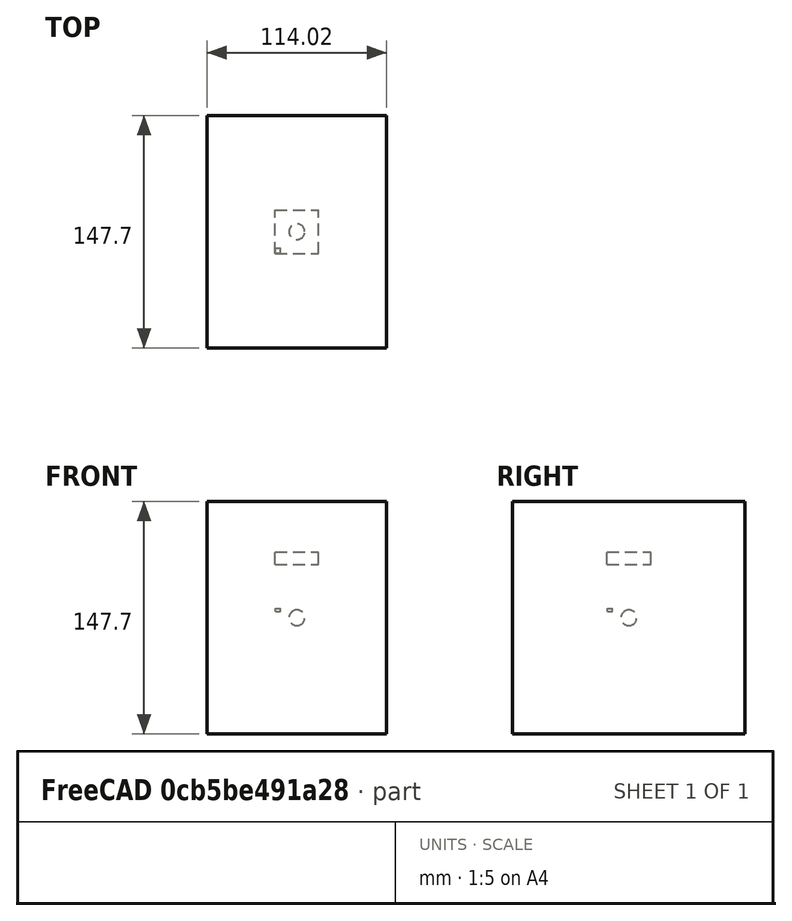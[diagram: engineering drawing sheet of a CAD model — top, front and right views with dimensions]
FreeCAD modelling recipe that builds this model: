
FCSTD DOCUMENT  (FreeCAD 1.0R39109 (Git))
Label: NoArray-borderTest-1
License: All rights reserved
objects: App::DocumentObjectGroupPython×1272, App::Link×77, App::Part×7, Part::FeaturePython×4, App::FeaturePython×1
note: 4 computed .brp shape members not serialized (recipe doc carries the construction recipe); baked Part::Feature solids carry a one-line shape summary decoded from their .brp

FEATURE [App::DocumentObjectGroupPython] HALFPI  # scripted group (container) (typed FeaturePython)
  name = HALFPI
  value = pi/2.
FEATURE [App::DocumentObjectGroupPython] PI  # scripted group (container) (typed FeaturePython)
  name = PI
  value = 1.*pi
FEATURE [App::DocumentObjectGroupPython] TWOPI  # scripted group (container) (typed FeaturePython)
  name = TWOPI
  value = 2.*pi
FEATURE [App::DocumentObjectGroupPython] Constants  # scripted group (container) (typed FeaturePython)
  Group = -> [HALFPI,PI,TWOPI]
FEATURE [App::DocumentObjectGroupPython] Variables  # scripted group (container) (typed FeaturePython)
FEATURE [App::DocumentObjectGroupPython] Quantities  # scripted group (container) (typed FeaturePython)
FEATURE [App::DocumentObjectGroupPython] Isotopes  # scripted group (container) (typed FeaturePython)
FEATURE [App::DocumentObjectGroupPython] Elements  # scripted group (container) (typed FeaturePython)
FEATURE [App::DocumentObjectGroupPython] G4_AIR  label="G4_AIR : 1.000"  # scripted group (container) (typed FeaturePython)
  n = 1
FEATURE [App::DocumentObjectGroupPython] Air  # scripted group (container) (typed FeaturePython)
  Dunit = mg/cm3
  Dvalue = 1.29
  Group = -> [G4_AIR]
  RINDEX = AirRINDEX
  conduct = 2
  density = 1
  expand = 3
  name = Air
  specific = 4
FEATURE [App::DocumentObjectGroupPython] SY  # scripted group (container) (typed FeaturePython)
  coldim = 1
  values = 100000/MeV
FEATURE [App::DocumentObjectGroupPython] RS  # scripted group (container) (typed FeaturePython)
  coldim = 1
  values = 1
FEATURE [App::DocumentObjectGroupPython] FTC  # scripted group (container) (typed FeaturePython)
  coldim = 1
  values = 21.5*ns
FEATURE [App::DocumentObjectGroupPython] STC  # scripted group (container) (typed FeaturePython)
  coldim = 1
  values = 43.8*ns
FEATURE [App::DocumentObjectGroupPython] RY1  # scripted group (container) (typed FeaturePython)
  coldim = 1
  values = 95
FEATURE [App::DocumentObjectGroupPython] RY2  # scripted group (container) (typed FeaturePython)
  coldim = 1
  values = 5
FEATURE [App::DocumentObjectGroupPython] YR  # scripted group (container) (typed FeaturePython)
  coldim = 1
  values = 0.8
FEATURE [App::DocumentObjectGroupPython] SCINTLAR  # scripted group (container) (typed FeaturePython)
  coldim = 2
  values = <blob: 2358 chars omitted>
FEATURE [App::DocumentObjectGroupPython] RINDEXLAR  # scripted group (container) (typed FeaturePython)
  coldim = 2
  values = <blob: 9384 chars omitted>
FEATURE [App::DocumentObjectGroupPython] ABSLENGTHLAR  # scripted group (container) (typed FeaturePython)
  coldim = 2
  values = 7.74901*eV 10.0*m 7.77525*eV 10.0*m 7.80167*eV 10.0*m 7.82827*eV 10.0*m 7.85506*eV 10.0*m 7.88202*eV 10.0*m 7.90917*eV 10.0*m 7.93651*eV 10.0*m 7.96404*eV 10.0*m 7.99176*eV 10.0*m 8.01968*eV 10.0*m 8.04779*eV 10.0*m 8.07609*eV 10.0*m 8.1046*eV 10.0*m 8.13331*eV 10.0*m 8.16222*eV 10.0*m 8.19134*eV 10.0*m 8.22067*eV 10.0*m 8.25021*eV 10.0*m 8.27996*eV 10.0*m 8.30993*eV 10.0*m 8.34012*eV 10.0*m 8.37052*eV 10.0*m 8.40115*eV 10.0*m 8.432*eV 10.0*m 8.46308*eV 10.0*m 8.4944*eV 10.0*m 8.52594*eV 10.0*m 8.55772*eV 10.0*m 8.58973*eV 10.0*m 8.62199*eV 10.0*m 8.65449*eV 10.0*m 8.68723*eV 10.0*m 8.72023*eV 10.0*m 8.75347*eV 10.0*m 8.78697*eV 10.0*m 8.82073*eV 10.0*m 8.85475*eV 10.0*m 8.88903*eV 10.0*m 8.92358*eV 10.0*m 8.9584*eV 10.0*m 8.99349*eV 10.0*m 9.02885*eV 10.0*m 9.0645*eV 10.0*m 9.10043*eV 10.0*m 9.13664*eV 10.0*m 9.17314*eV 10.0*m 9.20994*eV 10.0*m 9.24703*eV 10.0*m 9.28442*eV 10.0*m 9.32212*eV 10.0*m 9.36012*eV 10.0*m 9.39844*eV 10.0*m 9.43707*eV 10.0*m 9.47602*eV 10.0*m 9.51529*eV 10.0*m 9.55489*eV 10.0*m 9.59481*eV 10.0*m 9.63508*eV 10.0*m 9.67568*eV 10.0*m 9.71663*eV 10.0*m 9.75792*eV 10.0*m 9.79957*eV 10.0*m 9.84158*eV 10.0*m 9.88394*eV 10.0*m 9.92668*eV 10.0*m 9.96978*eV 10.0*m 10.0133*eV 10.0*m 10.0571*eV 10.0*m 10.1014*eV 10.0*m 10.146*eV 10.0*m 10.191*eV 10.0*m 10.2365*eV 10.0*m 10.2823*eV 10.0*m 10.3286*eV 10.0*m 10.3752*eV 10.0*m 10.4223*eV 10.0*m 10.4699*eV 10.0*m 10.5178*eV 10.0*m 10.5662*eV 10.0*m 10.6151*eV 10.0*m 10.6644*eV 10.0*m 10.7142*eV 10.0*m 10.7644*eV 10.0*m 10.8151*eV 10.0*m 10.8663*eV 10.0*m 10.9179*eV 10.0*m 10.9701*eV 10.0*m 11.0228*eV 10.0*m 11.076*eV 10.0*m 11.1296*eV 10.0*m 11.1839*eV 10.0*m 11.2386*eV 10.0*m 11.2939*eV 10.0*m 11.3497*eV 10.0*m 11.4061*eV 10.0*m 11.463*eV 10.0*m 11.5206*eV 10.0*m 11.5787*eV 10.0*m 11.6373*eV 10.0*m
FEATURE [App::DocumentObjectGroupPython] RAYLEIGHLAR  # scripted group (container) (typed FeaturePython)
  coldim = 2
  values = 7.74901*eV 90.0*cm 7.77525*eV 90.0*cm 7.80167*eV 90.0*cm 7.82827*eV 90.0*cm 7.85506*eV 90.0*cm 7.88202*eV 90.0*cm 7.90917*eV 90.0*cm 7.93651*eV 90.0*cm 7.96404*eV 90.0*cm 7.99176*eV 90.0*cm 8.01968*eV 90.0*cm 8.04779*eV 90.0*cm 8.07609*eV 90.0*cm 8.1046*eV 90.0*cm 8.13331*eV 90.0*cm 8.16222*eV 90.0*cm 8.19134*eV 90.0*cm 8.22067*eV 90.0*cm 8.25021*eV 90.0*cm 8.27996*eV 90.0*cm 8.30993*eV 90.0*cm 8.34012*eV 90.0*cm 8.37052*eV 90.0*cm 8.40115*eV 90.0*cm 8.432*eV 90.0*cm 8.46308*eV 90.0*cm 8.4944*eV 90.0*cm 8.52594*eV 90.0*cm 8.55772*eV 90.0*cm 8.58973*eV 90.0*cm 8.62199*eV 90.0*cm 8.65449*eV 90.0*cm 8.68723*eV 90.0*cm 8.72023*eV 90.0*cm 8.75347*eV 90.0*cm 8.78697*eV 90.0*cm 8.82073*eV 90.0*cm 8.85475*eV 90.0*cm 8.88903*eV 90.0*cm 8.92358*eV 90.0*cm 8.9584*eV 90.0*cm 8.99349*eV 90.0*cm 9.02885*eV 90.0*cm 9.0645*eV 90.0*cm 9.10043*eV 90.0*cm 9.13664*eV 90.0*cm 9.17314*eV 90.0*cm 9.20994*eV 90.0*cm 9.24703*eV 90.0*cm 9.28442*eV 90.0*cm 9.32212*eV 90.0*cm 9.36012*eV 90.0*cm 9.39844*eV 90.0*cm 9.43707*eV 90.0*cm 9.47602*eV 90.0*cm 9.51529*eV 90.0*cm 9.55489*eV 90.0*cm 9.59481*eV 90.0*cm 9.63508*eV 90.0*cm 9.67568*eV 90.0*cm 9.71663*eV 90.0*cm 9.75792*eV 90.0*cm 9.79957*eV 90.0*cm 9.84158*eV 90.0*cm 9.88394*eV 90.0*cm 9.92668*eV 90.0*cm 9.96978*eV 90.0*cm 10.0133*eV 90.0*cm 10.0571*eV 90.0*cm 10.1014*eV 90.0*cm 10.146*eV 90.0*cm 10.191*eV 90.0*cm 10.2365*eV 90.0*cm 10.2823*eV 90.0*cm 10.3286*eV 90.0*cm 10.3752*eV 90.0*cm 10.4223*eV 90.0*cm 10.4699*eV 90.0*cm 10.5178*eV 90.0*cm 10.5662*eV 90.0*cm 10.6151*eV 90.0*cm 10.6644*eV 90.0*cm 10.7142*eV 90.0*cm 10.7644*eV 90.0*cm 10.8151*eV 90.0*cm 10.8663*eV 90.0*cm 10.9179*eV 90.0*cm 10.9701*eV 90.0*cm 11.0228*eV 90.0*cm 11.076*eV 90.0*cm 11.1296*eV 90.0*cm 11.1839*eV 90.0*cm 11.2386*eV 90.0*cm 11.2939*eV 90.0*cm 11.3497*eV 90.0*cm 11.4061*eV 90.0*cm 11.463*eV 90.0*cm 11.5206*eV 90.0*cm 11.5787*eV 90.0*cm 11.6373*eV 90.0*cm
FEATURE [App::DocumentObjectGroupPython] REFLECTIVITY  # scripted group (container) (typed FeaturePython)
  coldim = 2
  values = 2.034*eV 0.98 2.068*eV 0.98 2.103*eV 0.98 2.139*eV 0.98 2.177*eV 0.98 2.216*eV 0.98 2.256*eV 0.98 2.298*eV 0.98 2.341*eV 0.98 2.386*eV 0.98 2.433*eV 0.98 2.481*eV 0.98 2.532*eV 0.98 2.585*eV 0.98 2.64*eV 0.98 2.697*eV 0.98 2.757*eV 0.98 2.82*eV 0.98 2.885*eV 0.98 2.954*eV 0.98 3.026*eV 0.98 3.102*eV 0.98 3.181*eV 0.98 3.265*eV 0.98 3.353*eV 0.98 3.446*eV 0.98 3.545*eV 0.98 3.649*eV 0.98 3.76*eV 0.98 3.877*eV 0.98 4.002*eV 0.98 4.136*eV 0.98 5.0*eV 0.98 6.0*eV 0.98 7.0*eV 0.98 8.0*eV 0.98 9.0*eV 0.98 9.0*eV 0.98 10.0*eV 0.98 11.0*eV 0.98 11.6*eV 0.98
FEATURE [App::DocumentObjectGroupPython] EFFICIENCY  # scripted group (container) (typed FeaturePython)
  coldim = 2
  values = 2.034*eV 1 2.068*eV 1 2.103*eV 1 2.139*eV 1 2.177*eV 1 2.216*eV 1 2.256*eV 1 2.298*eV 1 2.341*eV 1 2.386*eV 1 2.433*eV 1 2.481*eV 1 2.532*eV 1 2.585*eV 1 2.64*eV 1 2.697*eV 1 2.757*eV 1 2.82*eV 1 2.885*eV 1 2.954*eV 1 3.026*eV 1 3.102*eV 1 3.181*eV  1 3.265*eV 1 3.353*eV 1 3.446*eV 1 3.545*eV 1 3.649*eV 1 3.76*eV 1 3.877*eV 1 4.002*eV 1 4.136*eV 1 5.0*eV 1 6.0*eV 1 7.0*eV 1 8.0*eV 1 9.0*eV 1 9.0*eV 1 10.0*eV 1 11.0*eV 1 11.6*eV 1
FEATURE [App::DocumentObjectGroupPython] AirRINDEX  # scripted group (container) (typed FeaturePython)
  coldim = 2
  values = 2.034*eV 1 2.068*eV 1 2.103*eV 1 2.139*eV 1 2.177*eV 1 2.216*eV 1 2.256*eV 1 2.298*eV 1 2.341*eV 1 2.386*eV 1 2.433*eV 1 2.481*eV 1 2.532*eV 1 2.585*eV 1 2.64*eV 1 2.697*eV 1 2.757*eV 1 2.82*eV 1 2.885*eV 1 2.954*eV 1 3.026*eV 1 3.102*eV 1 3.181*eV 1 3.265*eV 1 3.353*eV 1 3.446*eV 1 3.545*eV 1 3.649*eV 1 3.76*eV 1 3.877*eV 1 4.002*eV 1 4.136*eV 1 5.0*eV 1 6.0*eV 1 7.0*eV 1 8.0*eV 1 9.0*eV 1 10.0*eV 1 11.0*eV 1 11.6*eV 1
FEATURE [App::DocumentObjectGroupPython] Matrix  # scripted group (container) (typed FeaturePython)
  Group = -> [SY,RS,FTC,STC,RY1,RY2,YR,SCINTLAR,RINDEXLAR,ABSLENGTHLAR,RAYLEIGHLAR,REFLECTIVITY,EFFICIENCY,AirRINDEX]
FEATURE [App::DocumentObjectGroupPython] ScintWrap  # scripted group (container) (typed FeaturePython)
  EFFICIENCY = EFFICIENCY
  REFLECTIVITY = REFLECTIVITY
  finish = 39
  model = 0
  type = 2
  value = 1
FEATURE [App::DocumentObjectGroupPython] Surfaces  # scripted group (container) (typed FeaturePython)
  Group = -> [ScintWrap]
FEATURE [App::DocumentObjectGroupPython] Opticals  # scripted group (container) (typed FeaturePython)
  Group = -> [Matrix,Surfaces]
FEATURE [App::DocumentObjectGroupPython] G4Isotopes  # scripted group (container) (typed FeaturePython)
FEATURE [App::DocumentObjectGroupPython] H_element  # scripted group (container) (typed FeaturePython)
  Z = 1
  atom_value = 1.008
  formula = H
  name = H_element
FEATURE [App::DocumentObjectGroupPython] He_element  # scripted group (container) (typed FeaturePython)
  Z = 2
  atom_value = 4.0026
  formula = He
  name = He_element
FEATURE [App::DocumentObjectGroupPython] Li_element  # scripted group (container) (typed FeaturePython)
  Z = 3
  atom_value = 6.94
  formula = Li
  name = Li_element
FEATURE [App::DocumentObjectGroupPython] Be_element  # scripted group (container) (typed FeaturePython)
  Z = 4
  atom_value = 9.01218
  formula = Be
  name = Be_element
FEATURE [App::DocumentObjectGroupPython] B_element  # scripted group (container) (typed FeaturePython)
  Z = 5
  atom_value = 10.81
  formula = B
  name = B_element
FEATURE [App::DocumentObjectGroupPython] C_element  # scripted group (container) (typed FeaturePython)
  Z = 6
  atom_value = 12.011
  formula = C
  name = C_element
FEATURE [App::DocumentObjectGroupPython] N_element  # scripted group (container) (typed FeaturePython)
  Z = 7
  atom_value = 14.007
  formula = N
  name = N_element
FEATURE [App::DocumentObjectGroupPython] O_element  # scripted group (container) (typed FeaturePython)
  Z = 8
  atom_value = 15.999
  formula = O
  name = O_element
FEATURE [App::DocumentObjectGroupPython] F_element  # scripted group (container) (typed FeaturePython)
  Z = 9
  atom_value = 18.9984
  formula = F
  name = F_element
FEATURE [App::DocumentObjectGroupPython] Ne_element  # scripted group (container) (typed FeaturePython)
  Z = 10
  atom_value = 20.1797
  formula = Ne
  name = Ne_element
FEATURE [App::DocumentObjectGroupPython] Na_element  # scripted group (container) (typed FeaturePython)
  Z = 11
  atom_value = 22.9898
  formula = Na
  name = Na_element
FEATURE [App::DocumentObjectGroupPython] Mg_element  # scripted group (container) (typed FeaturePython)
  Z = 12
  atom_value = 24.305
  formula = Mg
  name = Mg_element
FEATURE [App::DocumentObjectGroupPython] Al_element  # scripted group (container) (typed FeaturePython)
  Z = 13
  atom_value = 26.9815
  formula = Al
  name = Al_element
FEATURE [App::DocumentObjectGroupPython] Si_element  # scripted group (container) (typed FeaturePython)
  Z = 14
  atom_value = 28.085
  formula = Si
  name = Si_element
FEATURE [App::DocumentObjectGroupPython] P_element  # scripted group (container) (typed FeaturePython)
  Z = 15
  atom_value = 30.9738
  formula = P
  name = P_element
FEATURE [App::DocumentObjectGroupPython] S_element  # scripted group (container) (typed FeaturePython)
  Z = 16
  atom_value = 32.06
  formula = S
  name = S_element
FEATURE [App::DocumentObjectGroupPython] Cl_element  # scripted group (container) (typed FeaturePython)
  Z = 17
  atom_value = 35.45
  formula = Cl
  name = Cl_element
FEATURE [App::DocumentObjectGroupPython] Ar_element  # scripted group (container) (typed FeaturePython)
  Z = 18
  atom_value = 39.95
  formula = Ar
  name = Ar_element
FEATURE [App::DocumentObjectGroupPython] K_element  # scripted group (container) (typed FeaturePython)
  Z = 19
  atom_value = 39.0983
  formula = K
  name = K_element
FEATURE [App::DocumentObjectGroupPython] Ca_element  # scripted group (container) (typed FeaturePython)
  Z = 20
  atom_value = 40.078
  formula = Ca
  name = Ca_element
FEATURE [App::DocumentObjectGroupPython] Sc_element  # scripted group (container) (typed FeaturePython)
  Z = 21
  atom_value = 44.9559
  formula = Sc
  name = Sc_element
FEATURE [App::DocumentObjectGroupPython] Ti_element  # scripted group (container) (typed FeaturePython)
  Z = 22
  atom_value = 47.867
  formula = Ti
  name = Ti_element
FEATURE [App::DocumentObjectGroupPython] V_element  # scripted group (container) (typed FeaturePython)
  Z = 23
  atom_value = 50.9415
  formula = V
  name = V_element
FEATURE [App::DocumentObjectGroupPython] Cr_element  # scripted group (container) (typed FeaturePython)
  Z = 24
  atom_value = 51.9961
  formula = Cr
  name = Cr_element
FEATURE [App::DocumentObjectGroupPython] Mn_element  # scripted group (container) (typed FeaturePython)
  Z = 25
  atom_value = 54.938
  formula = Mn
  name = Mn_element
FEATURE [App::DocumentObjectGroupPython] Fe_element  # scripted group (container) (typed FeaturePython)
  Z = 26
  atom_value = 55.845
  formula = Fe
  name = Fe_element
FEATURE [App::DocumentObjectGroupPython] Co_element  # scripted group (container) (typed FeaturePython)
  Z = 27
  atom_value = 58.9332
  formula = Co
  name = Co_element
FEATURE [App::DocumentObjectGroupPython] Ni_element  # scripted group (container) (typed FeaturePython)
  Z = 28
  atom_value = 58.6934
  formula = Ni
  name = Ni_element
FEATURE [App::DocumentObjectGroupPython] Cu_element  # scripted group (container) (typed FeaturePython)
  Z = 29
  atom_value = 63.546
  formula = Cu
  name = Cu_element
FEATURE [App::DocumentObjectGroupPython] Zn_element  # scripted group (container) (typed FeaturePython)
  Z = 30
  atom_value = 65.38
  formula = Zn
  name = Zn_element
FEATURE [App::DocumentObjectGroupPython] Ga_element  # scripted group (container) (typed FeaturePython)
  Z = 31
  atom_value = 69.723
  formula = Ga
  name = Ga_element
FEATURE [App::DocumentObjectGroupPython] Ge_element  # scripted group (container) (typed FeaturePython)
  Z = 32
  atom_value = 72.63
  formula = Ge
  name = Ge_element
FEATURE [App::DocumentObjectGroupPython] As_element  # scripted group (container) (typed FeaturePython)
  Z = 33
  atom_value = 74.9216
  formula = As
  name = As_element
FEATURE [App::DocumentObjectGroupPython] Se_element  # scripted group (container) (typed FeaturePython)
  Z = 34
  atom_value = 78.971
  formula = Se
  name = Se_element
FEATURE [App::DocumentObjectGroupPython] Br_element  # scripted group (container) (typed FeaturePython)
  Z = 35
  atom_value = 79.904
  formula = Br
  name = Br_element
FEATURE [App::DocumentObjectGroupPython] Kr_element  # scripted group (container) (typed FeaturePython)
  Z = 36
  atom_value = 83.798
  formula = Kr
  name = Kr_element
FEATURE [App::DocumentObjectGroupPython] Rb_element  # scripted group (container) (typed FeaturePython)
  Z = 37
  atom_value = 85.4678
  formula = Rb
  name = Rb_element
FEATURE [App::DocumentObjectGroupPython] Sr_element  # scripted group (container) (typed FeaturePython)
  Z = 38
  atom_value = 87.62
  formula = Sr
  name = Sr_element
FEATURE [App::DocumentObjectGroupPython] Y_element  # scripted group (container) (typed FeaturePython)
  Z = 39
  atom_value = 88.9058
  formula = Y
  name = Y_element
FEATURE [App::DocumentObjectGroupPython] Zr_element  # scripted group (container) (typed FeaturePython)
  Z = 40
  atom_value = 91.224
  formula = Zr
  name = Zr_element
FEATURE [App::DocumentObjectGroupPython] Nb_element  # scripted group (container) (typed FeaturePython)
  Z = 41
  atom_value = 92.9064
  formula = Nb
  name = Nb_element
FEATURE [App::DocumentObjectGroupPython] Mo_element  # scripted group (container) (typed FeaturePython)
  Z = 42
  atom_value = 95.95
  formula = Mo
  name = Mo_element
FEATURE [App::DocumentObjectGroupPython] Tc_element  # scripted group (container) (typed FeaturePython)
  Z = 43
  atom_value = 97
  formula = Tc
  name = Tc_element
FEATURE [App::DocumentObjectGroupPython] Ru_element  # scripted group (container) (typed FeaturePython)
  Z = 44
  atom_value = 101.07
  formula = Ru
  name = Ru_element
FEATURE [App::DocumentObjectGroupPython] Rh_element  # scripted group (container) (typed FeaturePython)
  Z = 45
  atom_value = 102.905
  formula = Rh
  name = Rh_element
FEATURE [App::DocumentObjectGroupPython] Pd_element  # scripted group (container) (typed FeaturePython)
  Z = 46
  atom_value = 106.42
  formula = Pd
  name = Pd_element
FEATURE [App::DocumentObjectGroupPython] Ag_element  # scripted group (container) (typed FeaturePython)
  Z = 47
  atom_value = 107.868
  formula = Ag
  name = Ag_element
FEATURE [App::DocumentObjectGroupPython] Cd_element  # scripted group (container) (typed FeaturePython)
  Z = 48
  atom_value = 112.414
  formula = Cd
  name = Cd_element
FEATURE [App::DocumentObjectGroupPython] In_element  # scripted group (container) (typed FeaturePython)
  Z = 49
  atom_value = 114.818
  formula = In
  name = In_element
FEATURE [App::DocumentObjectGroupPython] Sn_element  # scripted group (container) (typed FeaturePython)
  Z = 50
  atom_value = 118.71
  formula = Sn
  name = Sn_element
FEATURE [App::DocumentObjectGroupPython] Sb_element  # scripted group (container) (typed FeaturePython)
  Z = 51
  atom_value = 121.76
  formula = Sb
  name = Sb_element
FEATURE [App::DocumentObjectGroupPython] Te_element  # scripted group (container) (typed FeaturePython)
  Z = 52
  atom_value = 127.6
  formula = Te
  name = Te_element
FEATURE [App::DocumentObjectGroupPython] I_element  # scripted group (container) (typed FeaturePython)
  Z = 53
  atom_value = 126.904
  formula = I
  name = I_element
FEATURE [App::DocumentObjectGroupPython] Xe_element  # scripted group (container) (typed FeaturePython)
  Z = 54
  atom_value = 131.293
  formula = Xe
  name = Xe_element
FEATURE [App::DocumentObjectGroupPython] Cs_element  # scripted group (container) (typed FeaturePython)
  Z = 55
  atom_value = 132.905
  formula = Cs
  name = Cs_element
FEATURE [App::DocumentObjectGroupPython] Ba_element  # scripted group (container) (typed FeaturePython)
  Z = 56
  atom_value = 137.327
  formula = Ba
  name = Ba_element
FEATURE [App::DocumentObjectGroupPython] La_element  # scripted group (container) (typed FeaturePython)
  Z = 57
  atom_value = 138.905
  formula = La
  name = La_element
FEATURE [App::DocumentObjectGroupPython] Ce_element  # scripted group (container) (typed FeaturePython)
  Z = 58
  atom_value = 140.116
  formula = Ce
  name = Ce_element
FEATURE [App::DocumentObjectGroupPython] Pr_element  # scripted group (container) (typed FeaturePython)
  Z = 59
  atom_value = 140.908
  formula = Pr
  name = Pr_element
FEATURE [App::DocumentObjectGroupPython] Nd_element  # scripted group (container) (typed FeaturePython)
  Z = 60
  atom_value = 144.242
  formula = Nd
  name = Nd_element
FEATURE [App::DocumentObjectGroupPython] Pm_element  # scripted group (container) (typed FeaturePython)
  Z = 61
  atom_value = 145
  formula = Pm
  name = Pm_element
FEATURE [App::DocumentObjectGroupPython] Sm_element  # scripted group (container) (typed FeaturePython)
  Z = 62
  atom_value = 150.36
  formula = Sm
  name = Sm_element
FEATURE [App::DocumentObjectGroupPython] Eu_element  # scripted group (container) (typed FeaturePython)
  Z = 63
  atom_value = 151.964
  formula = Eu
  name = Eu_element
FEATURE [App::DocumentObjectGroupPython] Gd_element  # scripted group (container) (typed FeaturePython)
  Z = 64
  atom_value = 157.25
  formula = Gd
  name = Gd_element
FEATURE [App::DocumentObjectGroupPython] Tb_element  # scripted group (container) (typed FeaturePython)
  Z = 65
  atom_value = 158.925
  formula = Tb
  name = Tb_element
FEATURE [App::DocumentObjectGroupPython] Dy_element  # scripted group (container) (typed FeaturePython)
  Z = 66
  atom_value = 162.5
  formula = Dy
  name = Dy_element
FEATURE [App::DocumentObjectGroupPython] Ho_element  # scripted group (container) (typed FeaturePython)
  Z = 67
  atom_value = 164.93
  formula = Ho
  name = Ho_element
FEATURE [App::DocumentObjectGroupPython] Er_element  # scripted group (container) (typed FeaturePython)
  Z = 68
  atom_value = 167.259
  formula = Er
  name = Er_element
FEATURE [App::DocumentObjectGroupPython] Tm_element  # scripted group (container) (typed FeaturePython)
  Z = 69
  atom_value = 168.934
  formula = Tm
  name = Tm_element
FEATURE [App::DocumentObjectGroupPython] Yb_element  # scripted group (container) (typed FeaturePython)
  Z = 70
  atom_value = 173.045
  formula = Yb
  name = Yb_element
FEATURE [App::DocumentObjectGroupPython] Lu_element  # scripted group (container) (typed FeaturePython)
  Z = 71
  atom_value = 174.967
  formula = Lu
  name = Lu_element
FEATURE [App::DocumentObjectGroupPython] Hf_element  # scripted group (container) (typed FeaturePython)
  Z = 72
  atom_value = 178.49
  formula = Hf
  name = Hf_element
FEATURE [App::DocumentObjectGroupPython] Ta_element  # scripted group (container) (typed FeaturePython)
  Z = 73
  atom_value = 180.948
  formula = Ta
  name = Ta_element
FEATURE [App::DocumentObjectGroupPython] W_element  # scripted group (container) (typed FeaturePython)
  Z = 74
  atom_value = 183.84
  formula = W
  name = W_element
FEATURE [App::DocumentObjectGroupPython] Re_element  # scripted group (container) (typed FeaturePython)
  Z = 75
  atom_value = 186.207
  formula = Re
  name = Re_element
FEATURE [App::DocumentObjectGroupPython] Os_element  # scripted group (container) (typed FeaturePython)
  Z = 76
  atom_value = 190.23
  formula = Os
  name = Os_element
FEATURE [App::DocumentObjectGroupPython] Ir_element  # scripted group (container) (typed FeaturePython)
  Z = 77
  atom_value = 192.217
  formula = Ir
  name = Ir_element
FEATURE [App::DocumentObjectGroupPython] Pt_element  # scripted group (container) (typed FeaturePython)
  Z = 78
  atom_value = 195.084
  formula = Pt
  name = Pt_element
FEATURE [App::DocumentObjectGroupPython] Au_element  # scripted group (container) (typed FeaturePython)
  Z = 79
  atom_value = 196.967
  formula = Au
  name = Au_element
FEATURE [App::DocumentObjectGroupPython] Hg_element  # scripted group (container) (typed FeaturePython)
  Z = 80
  atom_value = 200.592
  formula = Hg
  name = Hg_element
FEATURE [App::DocumentObjectGroupPython] Tl_element  # scripted group (container) (typed FeaturePython)
  Z = 81
  atom_value = 204.38
  formula = Tl
  name = Tl_element
FEATURE [App::DocumentObjectGroupPython] Pb_element  # scripted group (container) (typed FeaturePython)
  Z = 82
  atom_value = 207.2
  formula = Pb
  name = Pb_element
FEATURE [App::DocumentObjectGroupPython] Bi_element  # scripted group (container) (typed FeaturePython)
  Z = 83
  atom_value = 208.98
  formula = Bi
  name = Bi_element
FEATURE [App::DocumentObjectGroupPython] Po_element  # scripted group (container) (typed FeaturePython)
  Z = 84
  atom_value = 209
  formula = Po
  name = Po_element
FEATURE [App::DocumentObjectGroupPython] At_element  # scripted group (container) (typed FeaturePython)
  Z = 85
  atom_value = 210
  formula = At
  name = At_element
FEATURE [App::DocumentObjectGroupPython] Rn_element  # scripted group (container) (typed FeaturePython)
  Z = 86
  atom_value = 222
  formula = Rn
  name = Rn_element
FEATURE [App::DocumentObjectGroupPython] Fr_element  # scripted group (container) (typed FeaturePython)
  Z = 87
  atom_value = 223
  formula = Fr
  name = Fr_element
FEATURE [App::DocumentObjectGroupPython] Ra_element  # scripted group (container) (typed FeaturePython)
  Z = 88
  atom_value = 226
  formula = Ra
  name = Ra_element
FEATURE [App::DocumentObjectGroupPython] Ac_element  # scripted group (container) (typed FeaturePython)
  Z = 89
  atom_value = 227
  formula = Ac
  name = Ac_element
FEATURE [App::DocumentObjectGroupPython] Th_element  # scripted group (container) (typed FeaturePython)
  Z = 90
  atom_value = 232.038
  formula = Th
  name = Th_element
FEATURE [App::DocumentObjectGroupPython] Pa_element  # scripted group (container) (typed FeaturePython)
  Z = 91
  atom_value = 231.036
  formula = Pa
  name = Pa_element
FEATURE [App::DocumentObjectGroupPython] U_element  # scripted group (container) (typed FeaturePython)
  Z = 92
  atom_value = 238.029
  formula = U
  name = U_element
FEATURE [App::DocumentObjectGroupPython] Np_element  # scripted group (container) (typed FeaturePython)
  Z = 93
  atom_value = 237
  formula = Np
  name = Np_element
FEATURE [App::DocumentObjectGroupPython] Pu_element  # scripted group (container) (typed FeaturePython)
  Z = 94
  atom_value = 244
  formula = Pu
  name = Pu_element
FEATURE [App::DocumentObjectGroupPython] Am_element  # scripted group (container) (typed FeaturePython)
  Z = 95
  atom_value = 243
  formula = Am
  name = Am_element
FEATURE [App::DocumentObjectGroupPython] Cm_element  # scripted group (container) (typed FeaturePython)
  Z = 96
  atom_value = 247
  formula = Cm
  name = Cm_element
FEATURE [App::DocumentObjectGroupPython] Bk_element  # scripted group (container) (typed FeaturePython)
  Z = 97
  atom_value = 247
  formula = Bk
  name = Bk_element
FEATURE [App::DocumentObjectGroupPython] Cf_element  # scripted group (container) (typed FeaturePython)
  Z = 98
  atom_value = 251
  formula = Cf
  name = Cf_element
FEATURE [App::DocumentObjectGroupPython] G4Elements  # scripted group (container) (typed FeaturePython)
  Group = -> [H_element,He_element,Li_element,Be_element,B_element,C_element,N_element,O_element,F_element,Ne_element,Na_element,Mg_element,Al_element,Si_element,P_element,S_element,Cl_element,Ar_element,K_element,Ca_element,Sc_element,Ti_element,V_element,Cr_element,Mn_element,Fe_element,Co_element,Ni_element,Cu_element,Zn_element,Ga_element,Ge_element,As_element,Se_element,Br_element,Kr_element,Rb_element,+61 more]
FEATURE [App::DocumentObjectGroupPython] H_element001  label="H_element : 0.101"  # scripted group (container) (typed FeaturePython)
  n = 0.101327
FEATURE [App::DocumentObjectGroupPython] C_element001  label="C_element : 0.775"  # scripted group (container) (typed FeaturePython)
  n = 0.7755
FEATURE [App::DocumentObjectGroupPython] N_element001  label="N_element : 0.035"  # scripted group (container) (typed FeaturePython)
  n = 0.035057
FEATURE [App::DocumentObjectGroupPython] O_element001  label="O_element : 0.052"  # scripted group (container) (typed FeaturePython)
  n = 0.0523159
FEATURE [App::DocumentObjectGroupPython] F_element001  label="F_element : 0.017"  # scripted group (container) (typed FeaturePython)
  n = 0.017422
FEATURE [App::DocumentObjectGroupPython] Ca_element001  label="Ca_element : 0.018"  # scripted group (container) (typed FeaturePython)
  n = 0.018378
FEATURE [App::DocumentObjectGroupPython] G4_A_150_TISSUE  label="G4_A-150_TISSUE"  # scripted group (container) (typed FeaturePython)
  Dunit = g/cm3
  Dvalue = 1.127
  Group = -> [H_element001,C_element001,N_element001,O_element001,F_element001,Ca_element001]
  conduct = 2
  density = 1
  expand = 3
  formula = G4_A-150_TISSUE
  name = G4_A-150_TISSUE
  specific = 4
FEATURE [App::DocumentObjectGroupPython] C_element002  label="C_element : 3"  # scripted group (container) (typed FeaturePython)
  n = 3
  ref = C_element
FEATURE [App::DocumentObjectGroupPython] H_element002  label="H_element : 6"  # scripted group (container) (typed FeaturePython)
  n = 6
  ref = H_element
FEATURE [App::DocumentObjectGroupPython] O_element002  label="O_element : 1"  # scripted group (container) (typed FeaturePython)
  n = 1
  ref = O_element
FEATURE [App::DocumentObjectGroupPython] G4_ACETONE  # scripted group (container) (typed FeaturePython)
  Dunit = g/cm3
  Dvalue = 0.7899
  Group = -> [C_element002,H_element002,O_element002]
  conduct = 2
  density = 1
  expand = 3
  formula = G4_ACETONE
  name = G4_ACETONE
  specific = 4
FEATURE [App::DocumentObjectGroupPython] C_element003  label="C_element : 2"  # scripted group (container) (typed FeaturePython)
  n = 2
  ref = C_element
FEATURE [App::DocumentObjectGroupPython] H_element003  label="H_element : 2"  # scripted group (container) (typed FeaturePython)
  n = 2
  ref = H_element
FEATURE [App::DocumentObjectGroupPython] G4_ACETYLENE  # scripted group (container) (typed FeaturePython)
  Dunit = g/cm3
  Dvalue = 0.0010967
  Group = -> [C_element003,H_element003]
  conduct = 2
  density = 1
  expand = 3
  formula = G4_ACETYLENE
  name = G4_ACETYLENE
  specific = 4
FEATURE [App::DocumentObjectGroupPython] C_element004  label="C_element : 5"  # scripted group (container) (typed FeaturePython)
  n = 5
  ref = C_element
FEATURE [App::DocumentObjectGroupPython] H_element004  label="H_element : 5"  # scripted group (container) (typed FeaturePython)
  n = 5
  ref = H_element
FEATURE [App::DocumentObjectGroupPython] N_element002  label="N_element : 5"  # scripted group (container) (typed FeaturePython)
  n = 5
  ref = N_element
FEATURE [App::DocumentObjectGroupPython] G4_ADENINE  # scripted group (container) (typed FeaturePython)
  Dunit = g/cm3
  Dvalue = 1.6
  Group = -> [C_element004,H_element004,N_element002]
  conduct = 2
  density = 1
  expand = 3
  formula = G4_ADENINE
  name = G4_ADENINE
  specific = 4
FEATURE [App::DocumentObjectGroupPython] H_element005  label="H_element : 0.114"  # scripted group (container) (typed FeaturePython)
  n = 0.114
FEATURE [App::DocumentObjectGroupPython] C_element005  label="C_element : 0.598"  # scripted group (container) (typed FeaturePython)
  n = 0.598
FEATURE [App::DocumentObjectGroupPython] N_element003  label="N_element : 0.007"  # scripted group (container) (typed FeaturePython)
  n = 0.007
FEATURE [App::DocumentObjectGroupPython] O_element003  label="O_element : 0.278"  # scripted group (container) (typed FeaturePython)
  n = 0.278
FEATURE [App::DocumentObjectGroupPython] Na_element001  label="Na_element : 0.001"  # scripted group (container) (typed FeaturePython)
  n = 0.001
FEATURE [App::DocumentObjectGroupPython] S_element001  label="S_element : 0.001"  # scripted group (container) (typed FeaturePython)
  n = 0.001
FEATURE [App::DocumentObjectGroupPython] Cl_element001  label="Cl_element : 0.001"  # scripted group (container) (typed FeaturePython)
  n = 0.001
FEATURE [App::DocumentObjectGroupPython] G4_ADIPOSE_TISSUE_ICRP  # scripted group (container) (typed FeaturePython)
  Dunit = g/cm3
  Dvalue = 0.95
  Group = -> [H_element005,C_element005,N_element003,O_element003,Na_element001,S_element001,Cl_element001]
  conduct = 2
  density = 1
  expand = 3
  formula = G4_ADIPOSE_TISSUE_ICRP
  name = G4_ADIPOSE_TISSUE_ICRP
  specific = 4
FEATURE [App::DocumentObjectGroupPython] C_element006  label="C_element : 0.000"  # scripted group (container) (typed FeaturePython)
  n = 0.000124
FEATURE [App::DocumentObjectGroupPython] N_element004  label="N_element : 0.755"  # scripted group (container) (typed FeaturePython)
  n = 0.755268
FEATURE [App::DocumentObjectGroupPython] O_element004  label="O_element : 0.232"  # scripted group (container) (typed FeaturePython)
  n = 0.231781
FEATURE [App::DocumentObjectGroupPython] Ar_element001  label="Ar_element : 0.013"  # scripted group (container) (typed FeaturePython)
  n = 0.012827
FEATURE [App::DocumentObjectGroupPython] G4_AIR001  label="G4_AIR"  # scripted group (container) (typed FeaturePython)
  Dunit = g/cm3
  Dvalue = 0.00120479
  Group = -> [C_element006,N_element004,O_element004,Ar_element001]
  conduct = 2
  density = 1
  expand = 3
  formula = G4_AIR
  name = G4_AIR
  specific = 4
FEATURE [App::DocumentObjectGroupPython] C_element007  label="C_element : 006"  # scripted group (container) (typed FeaturePython)
  n = 3
  ref = C_element
FEATURE [App::DocumentObjectGroupPython] H_element006  label="H_element : 7"  # scripted group (container) (typed FeaturePython)
  n = 7
  ref = H_element
FEATURE [App::DocumentObjectGroupPython] N_element005  label="N_element : 1"  # scripted group (container) (typed FeaturePython)
  n = 1
  ref = N_element
FEATURE [App::DocumentObjectGroupPython] O_element005  label="O_element : 2"  # scripted group (container) (typed FeaturePython)
  n = 2
  ref = O_element
FEATURE [App::DocumentObjectGroupPython] G4_ALANINE  # scripted group (container) (typed FeaturePython)
  Dunit = g/cm3
  Dvalue = 1.42
  Group = -> [C_element007,H_element006,N_element005,O_element005]
  conduct = 2
  density = 1
  expand = 3
  formula = G4_ALANINE
  name = G4_ALANINE
  specific = 4
FEATURE [App::DocumentObjectGroupPython] Al_element001  label="Al_element : 2"  # scripted group (container) (typed FeaturePython)
  n = 2
  ref = Al_element
FEATURE [App::DocumentObjectGroupPython] O_element006  label="O_element : 3"  # scripted group (container) (typed FeaturePython)
  n = 3
  ref = O_element
FEATURE [App::DocumentObjectGroupPython] G4_ALUMINUM_OXIDE  # scripted group (container) (typed FeaturePython)
  Dunit = g/cm3
  Dvalue = 3.97
  Group = -> [Al_element001,O_element006]
  conduct = 2
  density = 1
  expand = 3
  formula = G4_ALUMINUM_OXIDE
  name = G4_ALUMINUM_OXIDE
  specific = 4
FEATURE [App::DocumentObjectGroupPython] H_element007  label="H_element : 0.106"  # scripted group (container) (typed FeaturePython)
  n = 0.10593
FEATURE [App::DocumentObjectGroupPython] C_element008  label="C_element : 0.789"  # scripted group (container) (typed FeaturePython)
  n = 0.788974
FEATURE [App::DocumentObjectGroupPython] O_element007  label="O_element : 0.105"  # scripted group (container) (typed FeaturePython)
  n = 0.105096
FEATURE [App::DocumentObjectGroupPython] G4_AMBER  # scripted group (container) (typed FeaturePython)
  Dunit = g/cm3
  Dvalue = 1.1
  Group = -> [H_element007,C_element008,O_element007]
  conduct = 2
  density = 1
  expand = 3
  formula = G4_AMBER
  name = G4_AMBER
  specific = 4
FEATURE [App::DocumentObjectGroupPython] N_element006  label="N_element : 006"  # scripted group (container) (typed FeaturePython)
  n = 1
  ref = N_element
FEATURE [App::DocumentObjectGroupPython] H_element008  label="H_element : 3"  # scripted group (container) (typed FeaturePython)
  n = 3
  ref = H_element
FEATURE [App::DocumentObjectGroupPython] G4_AMMONIA  # scripted group (container) (typed FeaturePython)
  Dunit = g/cm3
  Dvalue = 0.000826019
  Group = -> [N_element006,H_element008]
  conduct = 2
  density = 1
  expand = 3
  formula = G4_AMMONIA
  name = G4_AMMONIA
  specific = 4
FEATURE [App::DocumentObjectGroupPython] C_element009  label="C_element : 6"  # scripted group (container) (typed FeaturePython)
  n = 6
  ref = C_element
FEATURE [App::DocumentObjectGroupPython] H_element009  label="H_element : 008"  # scripted group (container) (typed FeaturePython)
  n = 7
  ref = H_element
FEATURE [App::DocumentObjectGroupPython] N_element007  label="N_element : 007"  # scripted group (container) (typed FeaturePython)
  n = 1
  ref = N_element
FEATURE [App::DocumentObjectGroupPython] G4_ANILINE  # scripted group (container) (typed FeaturePython)
  Dunit = g/cm3
  Dvalue = 1.0235
  Group = -> [C_element009,H_element009,N_element007]
  conduct = 2
  density = 1
  expand = 3
  formula = G4_ANILINE
  name = G4_ANILINE
  specific = 4
FEATURE [App::DocumentObjectGroupPython] C_element010  label="C_element : 14"  # scripted group (container) (typed FeaturePython)
  n = 14
  ref = C_element
FEATURE [App::DocumentObjectGroupPython] H_element010  label="H_element : 10"  # scripted group (container) (typed FeaturePython)
  n = 10
  ref = H_element
FEATURE [App::DocumentObjectGroupPython] G4_ANTHRACENE  # scripted group (container) (typed FeaturePython)
  Dunit = g/cm3
  Dvalue = 1.283
  Group = -> [C_element010,H_element010]
  conduct = 2
  density = 1
  expand = 3
  formula = G4_ANTHRACENE
  name = G4_ANTHRACENE
  specific = 4
FEATURE [App::DocumentObjectGroupPython] H_element011  label="H_element : 0.065"  # scripted group (container) (typed FeaturePython)
  n = 0.0654709
FEATURE [App::DocumentObjectGroupPython] C_element011  label="C_element : 0.537"  # scripted group (container) (typed FeaturePython)
  n = 0.536944
FEATURE [App::DocumentObjectGroupPython] N_element008  label="N_element : 0.021"  # scripted group (container) (typed FeaturePython)
  n = 0.0215
FEATURE [App::DocumentObjectGroupPython] O_element008  label="O_element : 0.032"  # scripted group (container) (typed FeaturePython)
  n = 0.032085
FEATURE [App::DocumentObjectGroupPython] F_element002  label="F_element : 0.167"  # scripted group (container) (typed FeaturePython)
  n = 0.167411
FEATURE [App::DocumentObjectGroupPython] Ca_element002  label="Ca_element : 0.177"  # scripted group (container) (typed FeaturePython)
  n = 0.176589
FEATURE [App::DocumentObjectGroupPython] G4_B_100_BONE  label="G4_B-100_BONE"  # scripted group (container) (typed FeaturePython)
  Dunit = g/cm3
  Dvalue = 1.45
  Group = -> [H_element011,C_element011,N_element008,O_element008,F_element002,Ca_element002]
  conduct = 2
  density = 1
  expand = 3
  formula = G4_B-100_BONE
  name = G4_B-100_BONE
  specific = 4
FEATURE [App::DocumentObjectGroupPython] H_element012  label="H_element : 0.057"  # scripted group (container) (typed FeaturePython)
  n = 0.057441
FEATURE [App::DocumentObjectGroupPython] C_element012  label="C_element : 0.790"  # scripted group (container) (typed FeaturePython)
  n = 0.774591
FEATURE [App::DocumentObjectGroupPython] O_element009  label="O_element : 0.168"  # scripted group (container) (typed FeaturePython)
  n = 0.167968
FEATURE [App::DocumentObjectGroupPython] G4_BAKELITE  # scripted group (container) (typed FeaturePython)
  Dunit = g/cm3
  Dvalue = 1.25
  Group = -> [H_element012,C_element012,O_element009]
  conduct = 2
  density = 1
  expand = 3
  formula = G4_BAKELITE
  name = G4_BAKELITE
  specific = 4
FEATURE [App::DocumentObjectGroupPython] Ba_element001  label="Ba_element : 1"  # scripted group (container) (typed FeaturePython)
  n = 1
  ref = Ba_element
FEATURE [App::DocumentObjectGroupPython] F_element003  label="F_element : 2"  # scripted group (container) (typed FeaturePython)
  n = 2
  ref = F_element
FEATURE [App::DocumentObjectGroupPython] G4_BARIUM_FLUORIDE  # scripted group (container) (typed FeaturePython)
  Dunit = g/cm3
  Dvalue = 4.89
  Group = -> [Ba_element001,F_element003]
  conduct = 2
  density = 1
  expand = 3
  formula = G4_BARIUM_FLUORIDE
  name = G4_BARIUM_FLUORIDE
  specific = 4
FEATURE [App::DocumentObjectGroupPython] Ba_element002  label="Ba_element : 002"  # scripted group (container) (typed FeaturePython)
  n = 1
  ref = Ba_element
FEATURE [App::DocumentObjectGroupPython] S_element002  label="S_element : 1"  # scripted group (container) (typed FeaturePython)
  n = 1
  ref = S_element
FEATURE [App::DocumentObjectGroupPython] O_element010  label="O_element : 4"  # scripted group (container) (typed FeaturePython)
  n = 4
  ref = O_element
FEATURE [App::DocumentObjectGroupPython] G4_BARIUM_SULFATE  # scripted group (container) (typed FeaturePython)
  Dunit = g/cm3
  Dvalue = 4.5
  Group = -> [Ba_element002,S_element002,O_element010]
  conduct = 2
  density = 1
  expand = 3
  formula = G4_BARIUM_SULFATE
  name = G4_BARIUM_SULFATE
  specific = 4
FEATURE [App::DocumentObjectGroupPython] C_element013  label="C_element : 007"  # scripted group (container) (typed FeaturePython)
  n = 6
  ref = C_element
FEATURE [App::DocumentObjectGroupPython] H_element013  label="H_element : 009"  # scripted group (container) (typed FeaturePython)
  n = 6
  ref = H_element
FEATURE [App::DocumentObjectGroupPython] G4_BENZENE  # scripted group (container) (typed FeaturePython)
  Dunit = g/cm3
  Dvalue = 0.87865
  Group = -> [C_element013,H_element013]
  conduct = 2
  density = 1
  expand = 3
  formula = G4_BENZENE
  name = G4_BENZENE
  specific = 4
FEATURE [App::DocumentObjectGroupPython] Be_element001  label="Be_element : 1"  # scripted group (container) (typed FeaturePython)
  n = 1
  ref = Be_element
FEATURE [App::DocumentObjectGroupPython] O_element011  label="O_element : 005"  # scripted group (container) (typed FeaturePython)
  n = 1
  ref = O_element
FEATURE [App::DocumentObjectGroupPython] G4_BERYLLIUM_OXIDE  # scripted group (container) (typed FeaturePython)
  Dunit = g/cm3
  Dvalue = 3.01
  Group = -> [Be_element001,O_element011]
  conduct = 2
  density = 1
  expand = 3
  formula = G4_BERYLLIUM_OXIDE
  name = G4_BERYLLIUM_OXIDE
  specific = 4
FEATURE [App::DocumentObjectGroupPython] Bi_element001  label="Bi_element : 4"  # scripted group (container) (typed FeaturePython)
  n = 4
  ref = Bi_element
FEATURE [App::DocumentObjectGroupPython] Ge_element001  label="Ge_element : 3"  # scripted group (container) (typed FeaturePython)
  n = 3
  ref = Ge_element
FEATURE [App::DocumentObjectGroupPython] O_element012  label="O_element : 12"  # scripted group (container) (typed FeaturePython)
  n = 12
  ref = O_element
FEATURE [App::DocumentObjectGroupPython] G4_BGO  # scripted group (container) (typed FeaturePython)
  Dunit = g/cm3
  Dvalue = 7.13
  Group = -> [Bi_element001,Ge_element001,O_element012]
  conduct = 2
  density = 1
  expand = 3
  formula = G4_BGO
  name = G4_BGO
  specific = 4
FEATURE [App::DocumentObjectGroupPython] H_element014  label="H_element : 0.102"  # scripted group (container) (typed FeaturePython)
  n = 0.102
FEATURE [App::DocumentObjectGroupPython] C_element014  label="C_element : 0.110"  # scripted group (container) (typed FeaturePython)
  n = 0.11
FEATURE [App::DocumentObjectGroupPython] N_element009  label="N_element : 0.033"  # scripted group (container) (typed FeaturePython)
  n = 0.033
FEATURE [App::DocumentObjectGroupPython] O_element013  label="O_element : 0.745"  # scripted group (container) (typed FeaturePython)
  n = 0.745
FEATURE [App::DocumentObjectGroupPython] Na_element002  label="Na_element : 0.002"  # scripted group (container) (typed FeaturePython)
  n = 0.001
FEATURE [App::DocumentObjectGroupPython] P_element001  label="P_element : 0.001"  # scripted group (container) (typed FeaturePython)
  n = 0.001
FEATURE [App::DocumentObjectGroupPython] S_element003  label="S_element : 0.002"  # scripted group (container) (typed FeaturePython)
  n = 0.002
FEATURE [App::DocumentObjectGroupPython] Cl_element002  label="Cl_element : 0.003"  # scripted group (container) (typed FeaturePython)
  n = 0.003
FEATURE [App::DocumentObjectGroupPython] K_element001  label="K_element : 0.002"  # scripted group (container) (typed FeaturePython)
  n = 0.002
FEATURE [App::DocumentObjectGroupPython] Fe_element001  label="Fe_element : 0.001"  # scripted group (container) (typed FeaturePython)
  n = 0.001
FEATURE [App::DocumentObjectGroupPython] G4_BLOOD_ICRP  # scripted group (container) (typed FeaturePython)
  Dunit = g/cm3
  Dvalue = 1.06
  Group = -> [H_element014,C_element014,N_element009,O_element013,Na_element002,P_element001,S_element003,Cl_element002,K_element001,Fe_element001]
  conduct = 2
  density = 1
  expand = 3
  formula = G4_BLOOD_ICRP
  name = G4_BLOOD_ICRP
  specific = 4
FEATURE [App::DocumentObjectGroupPython] H_element015  label="H_element : 0.064"  # scripted group (container) (typed FeaturePython)
  n = 0.064
FEATURE [App::DocumentObjectGroupPython] C_element015  label="C_element : 0.278"  # scripted group (container) (typed FeaturePython)
  n = 0.278
FEATURE [App::DocumentObjectGroupPython] N_element010  label="N_element : 0.027"  # scripted group (container) (typed FeaturePython)
  n = 0.027
FEATURE [App::DocumentObjectGroupPython] O_element014  label="O_element : 0.410"  # scripted group (container) (typed FeaturePython)
  n = 0.41
FEATURE [App::DocumentObjectGroupPython] Mg_element001  label="Mg_element : 0.002"  # scripted group (container) (typed FeaturePython)
  n = 0.002
FEATURE [App::DocumentObjectGroupPython] P_element002  label="P_element : 0.070"  # scripted group (container) (typed FeaturePython)
  n = 0.07
FEATURE [App::DocumentObjectGroupPython] S_element004  label="S_element : 0.003"  # scripted group (container) (typed FeaturePython)
  n = 0.002
FEATURE [App::DocumentObjectGroupPython] Ca_element003  label="Ca_element : 0.147"  # scripted group (container) (typed FeaturePython)
  n = 0.147
FEATURE [App::DocumentObjectGroupPython] G4_BONE_COMPACT_ICRU  # scripted group (container) (typed FeaturePython)
  Dunit = g/cm3
  Dvalue = 1.85
  Group = -> [H_element015,C_element015,N_element010,O_element014,Mg_element001,P_element002,S_element004,Ca_element003]
  conduct = 2
  density = 1
  expand = 3
  formula = G4_BONE_COMPACT_ICRU
  name = G4_BONE_COMPACT_ICRU
  specific = 4
FEATURE [App::DocumentObjectGroupPython] H_element016  label="H_element : 0.034"  # scripted group (container) (typed FeaturePython)
  n = 0.034
FEATURE [App::DocumentObjectGroupPython] C_element016  label="C_element : 0.155"  # scripted group (container) (typed FeaturePython)
  n = 0.155
FEATURE [App::DocumentObjectGroupPython] N_element011  label="N_element : 0.042"  # scripted group (container) (typed FeaturePython)
  n = 0.042
FEATURE [App::DocumentObjectGroupPython] O_element015  label="O_element : 0.435"  # scripted group (container) (typed FeaturePython)
  n = 0.435
FEATURE [App::DocumentObjectGroupPython] Na_element003  label="Na_element : 0.003"  # scripted group (container) (typed FeaturePython)
  n = 0.001
FEATURE [App::DocumentObjectGroupPython] Mg_element002  label="Mg_element : 0.003"  # scripted group (container) (typed FeaturePython)
  n = 0.002
FEATURE [App::DocumentObjectGroupPython] P_element003  label="P_element : 0.103"  # scripted group (container) (typed FeaturePython)
  n = 0.103
FEATURE [App::DocumentObjectGroupPython] S_element005  label="S_element : 0.004"  # scripted group (container) (typed FeaturePython)
  n = 0.003
FEATURE [App::DocumentObjectGroupPython] Ca_element004  label="Ca_element : 0.225"  # scripted group (container) (typed FeaturePython)
  n = 0.225
FEATURE [App::DocumentObjectGroupPython] G4_BONE_CORTICAL_ICRP  # scripted group (container) (typed FeaturePython)
  Dunit = g/cm3
  Dvalue = 1.92
  Group = -> [H_element016,C_element016,N_element011,O_element015,Na_element003,Mg_element002,P_element003,S_element005,Ca_element004]
  conduct = 2
  density = 1
  expand = 3
  formula = G4_BONE_CORTICAL_ICRP
  name = G4_BONE_CORTICAL_ICRP
  specific = 4
FEATURE [App::DocumentObjectGroupPython] B_element001  label="B_element : 4"  # scripted group (container) (typed FeaturePython)
  n = 4
  ref = B_element
FEATURE [App::DocumentObjectGroupPython] C_element017  label="C_element : 1"  # scripted group (container) (typed FeaturePython)
  n = 1
  ref = C_element
FEATURE [App::DocumentObjectGroupPython] G4_BORON_CARBIDE  # scripted group (container) (typed FeaturePython)
  Dunit = g/cm3
  Dvalue = 2.52
  Group = -> [B_element001,C_element017]
  conduct = 2
  density = 1
  expand = 3
  formula = G4_BORON_CARBIDE
  name = G4_BORON_CARBIDE
  specific = 4
FEATURE [App::DocumentObjectGroupPython] B_element002  label="B_element : 2"  # scripted group (container) (typed FeaturePython)
  n = 2
  ref = B_element
FEATURE [App::DocumentObjectGroupPython] O_element016  label="O_element : 006"  # scripted group (container) (typed FeaturePython)
  n = 3
  ref = O_element
FEATURE [App::DocumentObjectGroupPython] G4_BORON_OXIDE  # scripted group (container) (typed FeaturePython)
  Dunit = g/cm3
  Dvalue = 1.812
  Group = -> [B_element002,O_element016]
  conduct = 2
  density = 1
  expand = 3
  formula = G4_BORON_OXIDE
  name = G4_BORON_OXIDE
  specific = 4
FEATURE [App::DocumentObjectGroupPython] H_element017  label="H_element : 0.107"  # scripted group (container) (typed FeaturePython)
  n = 0.107
FEATURE [App::DocumentObjectGroupPython] C_element018  label="C_element : 0.145"  # scripted group (container) (typed FeaturePython)
  n = 0.145
FEATURE [App::DocumentObjectGroupPython] N_element012  label="N_element : 0.022"  # scripted group (container) (typed FeaturePython)
  n = 0.022
FEATURE [App::DocumentObjectGroupPython] O_element017  label="O_element : 0.712"  # scripted group (container) (typed FeaturePython)
  n = 0.712
FEATURE [App::DocumentObjectGroupPython] Na_element004  label="Na_element : 0.004"  # scripted group (container) (typed FeaturePython)
  n = 0.002
FEATURE [App::DocumentObjectGroupPython] P_element004  label="P_element : 0.004"  # scripted group (container) (typed FeaturePython)
  n = 0.004
FEATURE [App::DocumentObjectGroupPython] S_element006  label="S_element : 0.005"  # scripted group (container) (typed FeaturePython)
  n = 0.002
FEATURE [App::DocumentObjectGroupPython] Cl_element003  label="Cl_element : 0.004"  # scripted group (container) (typed FeaturePython)
  n = 0.003
FEATURE [App::DocumentObjectGroupPython] K_element002  label="K_element : 0.003"  # scripted group (container) (typed FeaturePython)
  n = 0.003
FEATURE [App::DocumentObjectGroupPython] G4_BRAIN_ICRP  # scripted group (container) (typed FeaturePython)
  Dunit = g/cm3
  Dvalue = 1.04
  Group = -> [H_element017,C_element018,N_element012,O_element017,Na_element004,P_element004,S_element006,Cl_element003,K_element002]
  conduct = 2
  density = 1
  expand = 3
  formula = G4_BRAIN_ICRP
  name = G4_BRAIN_ICRP
  specific = 4
FEATURE [App::DocumentObjectGroupPython] C_element019  label="C_element : 4"  # scripted group (container) (typed FeaturePython)
  n = 4
  ref = C_element
FEATURE [App::DocumentObjectGroupPython] H_element018  label="H_element : 010"  # scripted group (container) (typed FeaturePython)
  n = 10
  ref = H_element
FEATURE [App::DocumentObjectGroupPython] G4_BUTANE  # scripted group (container) (typed FeaturePython)
  Dunit = g/cm3
  Dvalue = 0.00249343
  Group = -> [C_element019,H_element018]
  conduct = 2
  density = 1
  expand = 3
  formula = G4_BUTANE
  name = G4_BUTANE
  specific = 4
FEATURE [App::DocumentObjectGroupPython] C_element020  label="C_element : 008"  # scripted group (container) (typed FeaturePython)
  n = 4
  ref = C_element
FEATURE [App::DocumentObjectGroupPython] H_element019  label="H_element : 011"  # scripted group (container) (typed FeaturePython)
  n = 10
  ref = H_element
FEATURE [App::DocumentObjectGroupPython] O_element018  label="O_element : 007"  # scripted group (container) (typed FeaturePython)
  n = 1
  ref = O_element
FEATURE [App::DocumentObjectGroupPython] G4_N_BUTYL_ALCOHOL  label="G4_N-BUTYL_ALCOHOL"  # scripted group (container) (typed FeaturePython)
  Dunit = g/cm3
  Dvalue = 0.8098
  Group = -> [C_element020,H_element019,O_element018]
  conduct = 2
  density = 1
  expand = 3
  formula = G4_N-BUTYL_ALCOHOL
  name = G4_N-BUTYL_ALCOHOL
  specific = 4
FEATURE [App::DocumentObjectGroupPython] H_element020  label="H_element : 0.025"  # scripted group (container) (typed FeaturePython)
  n = 0.02468
FEATURE [App::DocumentObjectGroupPython] C_element021  label="C_element : 0.502"  # scripted group (container) (typed FeaturePython)
  n = 0.501611
FEATURE [App::DocumentObjectGroupPython] O_element019  label="O_element : 0.005"  # scripted group (container) (typed FeaturePython)
  n = 0.004527
FEATURE [App::DocumentObjectGroupPython] F_element004  label="F_element : 0.465"  # scripted group (container) (typed FeaturePython)
  n = 0.465209
FEATURE [App::DocumentObjectGroupPython] Si_element001  label="Si_element : 0.004"  # scripted group (container) (typed FeaturePython)
  n = 0.003973
FEATURE [App::DocumentObjectGroupPython] G4_C_552  label="G4_C-552"  # scripted group (container) (typed FeaturePython)
  Dunit = g/cm3
  Dvalue = 1.76
  Group = -> [H_element020,C_element021,O_element019,F_element004,Si_element001]
  conduct = 2
  density = 1
  expand = 3
  formula = G4_C-552
  name = G4_C-552
  specific = 4
FEATURE [App::DocumentObjectGroupPython] Cd_element001  label="Cd_element : 1"  # scripted group (container) (typed FeaturePython)
  n = 1
  ref = Cd_element
FEATURE [App::DocumentObjectGroupPython] Te_element001  label="Te_element : 1"  # scripted group (container) (typed FeaturePython)
  n = 1
  ref = Te_element
FEATURE [App::DocumentObjectGroupPython] G4_CADMIUM_TELLURIDE  # scripted group (container) (typed FeaturePython)
  Dunit = g/cm3
  Dvalue = 6.2
  Group = -> [Cd_element001,Te_element001]
  conduct = 2
  density = 1
  expand = 3
  formula = G4_CADMIUM_TELLURIDE
  name = G4_CADMIUM_TELLURIDE
  specific = 4
FEATURE [App::DocumentObjectGroupPython] Cd_element002  label="Cd_element : 002"  # scripted group (container) (typed FeaturePython)
  n = 1
  ref = Cd_element
FEATURE [App::DocumentObjectGroupPython] W_element001  label="W_element : 1"  # scripted group (container) (typed FeaturePython)
  n = 1
  ref = W_element
FEATURE [App::DocumentObjectGroupPython] O_element020  label="O_element : 008"  # scripted group (container) (typed FeaturePython)
  n = 4
  ref = O_element
FEATURE [App::DocumentObjectGroupPython] G4_CADMIUM_TUNGSTATE  # scripted group (container) (typed FeaturePython)
  Dunit = g/cm3
  Dvalue = 7.9
  Group = -> [Cd_element002,W_element001,O_element020]
  conduct = 2
  density = 1
  expand = 3
  formula = G4_CADMIUM_TUNGSTATE
  name = G4_CADMIUM_TUNGSTATE
  specific = 4
FEATURE [App::DocumentObjectGroupPython] Ca_element005  label="Ca_element : 1"  # scripted group (container) (typed FeaturePython)
  n = 1
  ref = Ca_element
FEATURE [App::DocumentObjectGroupPython] C_element022  label="C_element : 009"  # scripted group (container) (typed FeaturePython)
  n = 1
  ref = C_element
FEATURE [App::DocumentObjectGroupPython] O_element021  label="O_element : 009"  # scripted group (container) (typed FeaturePython)
  n = 3
  ref = O_element
FEATURE [App::DocumentObjectGroupPython] G4_CALCIUM_CARBONATE  # scripted group (container) (typed FeaturePython)
  Dunit = g/cm3
  Dvalue = 2.8
  Group = -> [Ca_element005,C_element022,O_element021]
  conduct = 2
  density = 1
  expand = 3
  formula = G4_CALCIUM_CARBONATE
  name = G4_CALCIUM_CARBONATE
  specific = 4
FEATURE [App::DocumentObjectGroupPython] Ca_element006  label="Ca_element : 002"  # scripted group (container) (typed FeaturePython)
  n = 1
  ref = Ca_element
FEATURE [App::DocumentObjectGroupPython] F_element005  label="F_element : 003"  # scripted group (container) (typed FeaturePython)
  n = 2
  ref = F_element
FEATURE [App::DocumentObjectGroupPython] G4_CALCIUM_FLUORIDE  # scripted group (container) (typed FeaturePython)
  Dunit = g/cm3
  Dvalue = 3.18
  Group = -> [Ca_element006,F_element005]
  conduct = 2
  density = 1
  expand = 3
  formula = G4_CALCIUM_FLUORIDE
  name = G4_CALCIUM_FLUORIDE
  specific = 4
FEATURE [App::DocumentObjectGroupPython] Ca_element007  label="Ca_element : 003"  # scripted group (container) (typed FeaturePython)
  n = 1
  ref = Ca_element
FEATURE [App::DocumentObjectGroupPython] O_element022  label="O_element : 010"  # scripted group (container) (typed FeaturePython)
  n = 1
  ref = O_element
FEATURE [App::DocumentObjectGroupPython] G4_CALCIUM_OXIDE  # scripted group (container) (typed FeaturePython)
  Dunit = g/cm3
  Dvalue = 3.3
  Group = -> [Ca_element007,O_element022]
  conduct = 2
  density = 1
  expand = 3
  formula = G4_CALCIUM_OXIDE
  name = G4_CALCIUM_OXIDE
  specific = 4
FEATURE [App::DocumentObjectGroupPython] Ca_element008  label="Ca_element : 004"  # scripted group (container) (typed FeaturePython)
  n = 1
  ref = Ca_element
FEATURE [App::DocumentObjectGroupPython] S_element007  label="S_element : 002"  # scripted group (container) (typed FeaturePython)
  n = 1
  ref = S_element
FEATURE [App::DocumentObjectGroupPython] O_element023  label="O_element : 011"  # scripted group (container) (typed FeaturePython)
  n = 4
  ref = O_element
FEATURE [App::DocumentObjectGroupPython] G4_CALCIUM_SULFATE  # scripted group (container) (typed FeaturePython)
  Dunit = g/cm3
  Dvalue = 2.96
  Group = -> [Ca_element008,S_element007,O_element023]
  conduct = 2
  density = 1
  expand = 3
  formula = G4_CALCIUM_SULFATE
  name = G4_CALCIUM_SULFATE
  specific = 4
FEATURE [App::DocumentObjectGroupPython] Ca_element009  label="Ca_element : 005"  # scripted group (container) (typed FeaturePython)
  n = 1
  ref = Ca_element
FEATURE [App::DocumentObjectGroupPython] W_element002  label="W_element : 002"  # scripted group (container) (typed FeaturePython)
  n = 1
  ref = W_element
FEATURE [App::DocumentObjectGroupPython] O_element024  label="O_element : 012"  # scripted group (container) (typed FeaturePython)
  n = 4
  ref = O_element
FEATURE [App::DocumentObjectGroupPython] G4_CALCIUM_TUNGSTATE  # scripted group (container) (typed FeaturePython)
  Dunit = g/cm3
  Dvalue = 6.062
  Group = -> [Ca_element009,W_element002,O_element024]
  conduct = 2
  density = 1
  expand = 3
  formula = G4_CALCIUM_TUNGSTATE
  name = G4_CALCIUM_TUNGSTATE
  specific = 4
FEATURE [App::DocumentObjectGroupPython] C_element023  label="C_element : 010"  # scripted group (container) (typed FeaturePython)
  n = 1
  ref = C_element
FEATURE [App::DocumentObjectGroupPython] O_element025  label="O_element : 013"  # scripted group (container) (typed FeaturePython)
  n = 2
  ref = O_element
FEATURE [App::DocumentObjectGroupPython] G4_CARBON_DIOXIDE  # scripted group (container) (typed FeaturePython)
  Dunit = g/cm3
  Dvalue = 0.00184212
  Group = -> [C_element023,O_element025]
  conduct = 2
  density = 1
  expand = 3
  formula = G4_CARBON_DIOXIDE
  name = G4_CARBON_DIOXIDE
  specific = 4
FEATURE [App::DocumentObjectGroupPython] C_element024  label="C_element : 011"  # scripted group (container) (typed FeaturePython)
  n = 1
  ref = C_element
FEATURE [App::DocumentObjectGroupPython] Cl_element004  label="Cl_element : 4"  # scripted group (container) (typed FeaturePython)
  n = 4
  ref = Cl_element
FEATURE [App::DocumentObjectGroupPython] G4_CARBON_TETRACHLORIDE  # scripted group (container) (typed FeaturePython)
  Dunit = g/cm3
  Dvalue = 1.594
  Group = -> [C_element024,Cl_element004]
  conduct = 2
  density = 1
  expand = 3
  formula = G4_CARBON_TETRACHLORIDE
  name = G4_CARBON_TETRACHLORIDE
  specific = 4
FEATURE [App::DocumentObjectGroupPython] C_element025  label="C_element : 012"  # scripted group (container) (typed FeaturePython)
  n = 6
  ref = C_element
FEATURE [App::DocumentObjectGroupPython] H_element021  label="H_element : 012"  # scripted group (container) (typed FeaturePython)
  n = 10
  ref = H_element
FEATURE [App::DocumentObjectGroupPython] O_element026  label="O_element : 5"  # scripted group (container) (typed FeaturePython)
  n = 5
  ref = O_element
FEATURE [App::DocumentObjectGroupPython] G4_CELLULOSE_CELLOPHANE  # scripted group (container) (typed FeaturePython)
  Dunit = g/cm3
  Dvalue = 1.42
  Group = -> [C_element025,H_element021,O_element026]
  conduct = 2
  density = 1
  expand = 3
  formula = G4_CELLULOSE_CELLOPHANE
  name = G4_CELLULOSE_CELLOPHANE
  specific = 4
FEATURE [App::DocumentObjectGroupPython] H_element022  label="H_element : 0.067"  # scripted group (container) (typed FeaturePython)
  n = 0.067125
FEATURE [App::DocumentObjectGroupPython] C_element026  label="C_element : 0.545"  # scripted group (container) (typed FeaturePython)
  n = 0.545403
FEATURE [App::DocumentObjectGroupPython] O_element027  label="O_element : 0.387"  # scripted group (container) (typed FeaturePython)
  n = 0.387472
FEATURE [App::DocumentObjectGroupPython] G4_CELLULOSE_BUTYRATE  # scripted group (container) (typed FeaturePython)
  Dunit = g/cm3
  Dvalue = 1.2
  Group = -> [H_element022,C_element026,O_element027]
  conduct = 2
  density = 1
  expand = 3
  formula = G4_CELLULOSE_BUTYRATE
  name = G4_CELLULOSE_BUTYRATE
  specific = 4
FEATURE [App::DocumentObjectGroupPython] H_element023  label="H_element : 0.029"  # scripted group (container) (typed FeaturePython)
  n = 0.029216
FEATURE [App::DocumentObjectGroupPython] C_element027  label="C_element : 0.271"  # scripted group (container) (typed FeaturePython)
  n = 0.271296
FEATURE [App::DocumentObjectGroupPython] N_element013  label="N_element : 0.121"  # scripted group (container) (typed FeaturePython)
  n = 0.121276
FEATURE [App::DocumentObjectGroupPython] O_element028  label="O_element : 0.578"  # scripted group (container) (typed FeaturePython)
  n = 0.578212
FEATURE [App::DocumentObjectGroupPython] G4_CELLULOSE_NITRATE  # scripted group (container) (typed FeaturePython)
  Dunit = g/cm3
  Dvalue = 1.49
  Group = -> [H_element023,C_element027,N_element013,O_element028]
  conduct = 2
  density = 1
  expand = 3
  formula = G4_CELLULOSE_NITRATE
  name = G4_CELLULOSE_NITRATE
  specific = 4
FEATURE [App::DocumentObjectGroupPython] H_element024  label="H_element : 0.108"  # scripted group (container) (typed FeaturePython)
  n = 0.107596
FEATURE [App::DocumentObjectGroupPython] N_element014  label="N_element : 0.001"  # scripted group (container) (typed FeaturePython)
  n = 0.0008
FEATURE [App::DocumentObjectGroupPython] O_element029  label="O_element : 0.875"  # scripted group (container) (typed FeaturePython)
  n = 0.874976
FEATURE [App::DocumentObjectGroupPython] S_element008  label="S_element : 0.015"  # scripted group (container) (typed FeaturePython)
  n = 0.014627
FEATURE [App::DocumentObjectGroupPython] Ce_element001  label="Ce_element : 0.002"  # scripted group (container) (typed FeaturePython)
  n = 0.002001
FEATURE [App::DocumentObjectGroupPython] G4_CERIC_SULFATE  # scripted group (container) (typed FeaturePython)
  Dunit = g/cm3
  Dvalue = 1.03
  Group = -> [H_element024,N_element014,O_element029,S_element008,Ce_element001]
  conduct = 2
  density = 1
  expand = 3
  formula = G4_CERIC_SULFATE
  name = G4_CERIC_SULFATE
  specific = 4
FEATURE [App::DocumentObjectGroupPython] Cs_element001  label="Cs_element : 1"  # scripted group (container) (typed FeaturePython)
  n = 1
  ref = Cs_element
FEATURE [App::DocumentObjectGroupPython] F_element006  label="F_element : 1"  # scripted group (container) (typed FeaturePython)
  n = 1
  ref = F_element
FEATURE [App::DocumentObjectGroupPython] G4_CESIUM_FLUORIDE  # scripted group (container) (typed FeaturePython)
  Dunit = g/cm3
  Dvalue = 4.115
  Group = -> [Cs_element001,F_element006]
  conduct = 2
  density = 1
  expand = 3
  formula = G4_CESIUM_FLUORIDE
  name = G4_CESIUM_FLUORIDE
  specific = 4
FEATURE [App::DocumentObjectGroupPython] Cs_element002  label="Cs_element : 002"  # scripted group (container) (typed FeaturePython)
  n = 1
  ref = Cs_element
FEATURE [App::DocumentObjectGroupPython] I_element001  label="I_element : 1"  # scripted group (container) (typed FeaturePython)
  n = 1
  ref = I_element
FEATURE [App::DocumentObjectGroupPython] G4_CESIUM_IODIDE001  label="G4_CESIUM_IODIDE"  # scripted group (container) (typed FeaturePython)
  Dunit = g/cm3
  Dvalue = 4.51
  Group = -> [Cs_element002,I_element001]
  conduct = 2
  density = 1
  expand = 3
  formula = G4_CESIUM_IODIDE
  name = G4_CESIUM_IODIDE
  specific = 4
FEATURE [App::DocumentObjectGroupPython] C_element028  label="C_element : 013"  # scripted group (container) (typed FeaturePython)
  n = 6
  ref = C_element
FEATURE [App::DocumentObjectGroupPython] H_element025  label="H_element : 013"  # scripted group (container) (typed FeaturePython)
  n = 5
  ref = H_element
FEATURE [App::DocumentObjectGroupPython] Cl_element005  label="Cl_element : 1"  # scripted group (container) (typed FeaturePython)
  n = 1
  ref = Cl_element
FEATURE [App::DocumentObjectGroupPython] G4_CHLOROBENZENE  # scripted group (container) (typed FeaturePython)
  Dunit = g/cm3
  Dvalue = 1.1058
  Group = -> [C_element028,H_element025,Cl_element005]
  conduct = 2
  density = 1
  expand = 3
  formula = G4_CHLOROBENZENE
  name = G4_CHLOROBENZENE
  specific = 4
FEATURE [App::DocumentObjectGroupPython] C_element029  label="C_element : 014"  # scripted group (container) (typed FeaturePython)
  n = 1
  ref = C_element
FEATURE [App::DocumentObjectGroupPython] H_element026  label="H_element : 1"  # scripted group (container) (typed FeaturePython)
  n = 1
  ref = H_element
FEATURE [App::DocumentObjectGroupPython] Cl_element006  label="Cl_element : 3"  # scripted group (container) (typed FeaturePython)
  n = 3
  ref = Cl_element
FEATURE [App::DocumentObjectGroupPython] G4_CHLOROFORM  # scripted group (container) (typed FeaturePython)
  Dunit = g/cm3
  Dvalue = 1.4832
  Group = -> [C_element029,H_element026,Cl_element006]
  conduct = 2
  density = 1
  expand = 3
  formula = G4_CHLOROFORM
  name = G4_CHLOROFORM
  specific = 4
FEATURE [App::DocumentObjectGroupPython] H_element027  label="H_element : 0.010"  # scripted group (container) (typed FeaturePython)
  n = 0.01
FEATURE [App::DocumentObjectGroupPython] C_element030  label="C_element : 0.001"  # scripted group (container) (typed FeaturePython)
  n = 0.001
FEATURE [App::DocumentObjectGroupPython] O_element030  label="O_element : 0.529"  # scripted group (container) (typed FeaturePython)
  n = 0.529107
FEATURE [App::DocumentObjectGroupPython] Na_element005  label="Na_element : 0.016"  # scripted group (container) (typed FeaturePython)
  n = 0.016
FEATURE [App::DocumentObjectGroupPython] Mg_element003  label="Mg_element : 0.004"  # scripted group (container) (typed FeaturePython)
  n = 0.002
FEATURE [App::DocumentObjectGroupPython] Al_element002  label="Al_element : 0.034"  # scripted group (container) (typed FeaturePython)
  n = 0.033872
FEATURE [App::DocumentObjectGroupPython] Si_element002  label="Si_element : 0.337"  # scripted group (container) (typed FeaturePython)
  n = 0.337021
FEATURE [App::DocumentObjectGroupPython] K_element003  label="K_element : 0.013"  # scripted group (container) (typed FeaturePython)
  n = 0.013
FEATURE [App::DocumentObjectGroupPython] Ca_element010  label="Ca_element : 0.044"  # scripted group (container) (typed FeaturePython)
  n = 0.044
FEATURE [App::DocumentObjectGroupPython] Fe_element002  label="Fe_element : 0.014"  # scripted group (container) (typed FeaturePython)
  n = 0.014
FEATURE [App::DocumentObjectGroupPython] G4_CONCRETE  # scripted group (container) (typed FeaturePython)
  Dunit = g/cm3
  Dvalue = 2.3
  Group = -> [H_element027,C_element030,O_element030,Na_element005,Mg_element003,Al_element002,Si_element002,K_element003,Ca_element010,Fe_element002]
  conduct = 2
  density = 1
  expand = 3
  formula = G4_CONCRETE
  name = G4_CONCRETE
  specific = 4
FEATURE [App::DocumentObjectGroupPython] C_element031  label="C_element : 015"  # scripted group (container) (typed FeaturePython)
  n = 6
  ref = C_element
FEATURE [App::DocumentObjectGroupPython] H_element028  label="H_element : 12"  # scripted group (container) (typed FeaturePython)
  n = 12
  ref = H_element
FEATURE [App::DocumentObjectGroupPython] G4_CYCLOHEXANE  # scripted group (container) (typed FeaturePython)
  Dunit = g/cm3
  Dvalue = 0.779
  Group = -> [C_element031,H_element028]
  conduct = 2
  density = 1
  expand = 3
  formula = G4_CYCLOHEXANE
  name = G4_CYCLOHEXANE
  specific = 4
FEATURE [App::DocumentObjectGroupPython] C_element032  label="C_element : 016"  # scripted group (container) (typed FeaturePython)
  n = 6
  ref = C_element
FEATURE [App::DocumentObjectGroupPython] H_element029  label="H_element : 4"  # scripted group (container) (typed FeaturePython)
  n = 4
  ref = H_element
FEATURE [App::DocumentObjectGroupPython] Cl_element007  label="Cl_element : 2"  # scripted group (container) (typed FeaturePython)
  n = 2
  ref = Cl_element
FEATURE [App::DocumentObjectGroupPython] G4_1_2_DICHLOROBENZENE  label="G4_1.2-DICHLOROBENZENE"  # scripted group (container) (typed FeaturePython)
  Dunit = g/cm3
  Dvalue = 1.3048
  Group = -> [C_element032,H_element029,Cl_element007]
  conduct = 2
  density = 1
  expand = 3
  formula = G4_1.2-DICHLOROBENZENE
  name = G4_1.2-DICHLOROBENZENE
  specific = 4
FEATURE [App::DocumentObjectGroupPython] C_element033  label="C_element : 017"  # scripted group (container) (typed FeaturePython)
  n = 4
  ref = C_element
FEATURE [App::DocumentObjectGroupPython] H_element030  label="H_element : 8"  # scripted group (container) (typed FeaturePython)
  n = 8
  ref = H_element
FEATURE [App::DocumentObjectGroupPython] O_element031  label="O_element : 014"  # scripted group (container) (typed FeaturePython)
  n = 1
  ref = O_element
FEATURE [App::DocumentObjectGroupPython] Cl_element008  label="Cl_element : 005"  # scripted group (container) (typed FeaturePython)
  n = 2
  ref = Cl_element
FEATURE [App::DocumentObjectGroupPython] G4_DICHLORODIETHYL_ETHER  # scripted group (container) (typed FeaturePython)
  Dunit = g/cm3
  Dvalue = 1.2199
  Group = -> [C_element033,H_element030,O_element031,Cl_element008]
  conduct = 2
  density = 1
  expand = 3
  formula = G4_DICHLORODIETHYL_ETHER
  name = G4_DICHLORODIETHYL_ETHER
  specific = 4
FEATURE [App::DocumentObjectGroupPython] C_element034  label="C_element : 018"  # scripted group (container) (typed FeaturePython)
  n = 2
  ref = C_element
FEATURE [App::DocumentObjectGroupPython] H_element031  label="H_element : 014"  # scripted group (container) (typed FeaturePython)
  n = 4
  ref = H_element
FEATURE [App::DocumentObjectGroupPython] Cl_element009  label="Cl_element : 006"  # scripted group (container) (typed FeaturePython)
  n = 2
  ref = Cl_element
FEATURE [App::DocumentObjectGroupPython] G4_1_2_DICHLOROETHANE  label="G4_1.2-DICHLOROETHANE"  # scripted group (container) (typed FeaturePython)
  Dunit = g/cm3
  Dvalue = 1.2351
  Group = -> [C_element034,H_element031,Cl_element009]
  conduct = 2
  density = 1
  expand = 3
  formula = G4_1.2-DICHLOROETHANE
  name = G4_1.2-DICHLOROETHANE
  specific = 4
FEATURE [App::DocumentObjectGroupPython] C_element035  label="C_element : 019"  # scripted group (container) (typed FeaturePython)
  n = 4
  ref = C_element
FEATURE [App::DocumentObjectGroupPython] H_element032  label="H_element : 015"  # scripted group (container) (typed FeaturePython)
  n = 10
  ref = H_element
FEATURE [App::DocumentObjectGroupPython] O_element032  label="O_element : 015"  # scripted group (container) (typed FeaturePython)
  n = 1
  ref = O_element
FEATURE [App::DocumentObjectGroupPython] G4_DIETHYL_ETHER  # scripted group (container) (typed FeaturePython)
  Dunit = g/cm3
  Dvalue = 0.71378
  Group = -> [C_element035,H_element032,O_element032]
  conduct = 2
  density = 1
  expand = 3
  formula = G4_DIETHYL_ETHER
  name = G4_DIETHYL_ETHER
  specific = 4
FEATURE [App::DocumentObjectGroupPython] C_element036  label="C_element : 020"  # scripted group (container) (typed FeaturePython)
  n = 3
  ref = C_element
FEATURE [App::DocumentObjectGroupPython] H_element033  label="H_element : 016"  # scripted group (container) (typed FeaturePython)
  n = 7
  ref = H_element
FEATURE [App::DocumentObjectGroupPython] N_element015  label="N_element : 008"  # scripted group (container) (typed FeaturePython)
  n = 1
  ref = N_element
FEATURE [App::DocumentObjectGroupPython] O_element033  label="O_element : 016"  # scripted group (container) (typed FeaturePython)
  n = 1
  ref = O_element
FEATURE [App::DocumentObjectGroupPython] G4_N_N_DIMETHYL_FORMAMIDE  label="G4_N.N-DIMETHYL_FORMAMIDE"  # scripted group (container) (typed FeaturePython)
  Dunit = g/cm3
  Dvalue = 0.9487
  Group = -> [C_element036,H_element033,N_element015,O_element033]
  conduct = 2
  density = 1
  expand = 3
  formula = G4_N.N-DIMETHYL_FORMAMIDE
  name = G4_N.N-DIMETHYL_FORMAMIDE
  specific = 4
FEATURE [App::DocumentObjectGroupPython] C_element037  label="C_element : 021"  # scripted group (container) (typed FeaturePython)
  n = 2
  ref = C_element
FEATURE [App::DocumentObjectGroupPython] H_element034  label="H_element : 017"  # scripted group (container) (typed FeaturePython)
  n = 6
  ref = H_element
FEATURE [App::DocumentObjectGroupPython] O_element034  label="O_element : 017"  # scripted group (container) (typed FeaturePython)
  n = 1
  ref = O_element
FEATURE [App::DocumentObjectGroupPython] S_element009  label="S_element : 003"  # scripted group (container) (typed FeaturePython)
  n = 1
  ref = S_element
FEATURE [App::DocumentObjectGroupPython] G4_DIMETHYL_SULFOXIDE  # scripted group (container) (typed FeaturePython)
  Dunit = g/cm3
  Dvalue = 1.1014
  Group = -> [C_element037,H_element034,O_element034,S_element009]
  conduct = 2
  density = 1
  expand = 3
  formula = G4_DIMETHYL_SULFOXIDE
  name = G4_DIMETHYL_SULFOXIDE
  specific = 4
FEATURE [App::DocumentObjectGroupPython] C_element038  label="C_element : 022"  # scripted group (container) (typed FeaturePython)
  n = 2
  ref = C_element
FEATURE [App::DocumentObjectGroupPython] H_element035  label="H_element : 018"  # scripted group (container) (typed FeaturePython)
  n = 6
  ref = H_element
FEATURE [App::DocumentObjectGroupPython] G4_ETHANE  # scripted group (container) (typed FeaturePython)
  Dunit = g/cm3
  Dvalue = 0.00125324
  Group = -> [C_element038,H_element035]
  conduct = 2
  density = 1
  expand = 3
  formula = G4_ETHANE
  name = G4_ETHANE
  specific = 4
FEATURE [App::DocumentObjectGroupPython] C_element039  label="C_element : 023"  # scripted group (container) (typed FeaturePython)
  n = 2
  ref = C_element
FEATURE [App::DocumentObjectGroupPython] H_element036  label="H_element : 019"  # scripted group (container) (typed FeaturePython)
  n = 6
  ref = H_element
FEATURE [App::DocumentObjectGroupPython] O_element035  label="O_element : 018"  # scripted group (container) (typed FeaturePython)
  n = 1
  ref = O_element
FEATURE [App::DocumentObjectGroupPython] G4_ETHYL_ALCOHOL  # scripted group (container) (typed FeaturePython)
  Dunit = g/cm3
  Dvalue = 0.7893
  Group = -> [C_element039,H_element036,O_element035]
  conduct = 2
  density = 1
  expand = 3
  formula = G4_ETHYL_ALCOHOL
  name = G4_ETHYL_ALCOHOL
  specific = 4
FEATURE [App::DocumentObjectGroupPython] H_element037  label="H_element : 0.090"  # scripted group (container) (typed FeaturePython)
  n = 0.090027
FEATURE [App::DocumentObjectGroupPython] C_element040  label="C_element : 0.585"  # scripted group (container) (typed FeaturePython)
  n = 0.585182
FEATURE [App::DocumentObjectGroupPython] O_element036  label="O_element : 0.325"  # scripted group (container) (typed FeaturePython)
  n = 0.324791
FEATURE [App::DocumentObjectGroupPython] G4_ETHYL_CELLULOSE  # scripted group (container) (typed FeaturePython)
  Dunit = g/cm3
  Dvalue = 1.13
  Group = -> [H_element037,C_element040,O_element036]
  conduct = 2
  density = 1
  expand = 3
  formula = G4_ETHYL_CELLULOSE
  name = G4_ETHYL_CELLULOSE
  specific = 4
FEATURE [App::DocumentObjectGroupPython] C_element041  label="C_element : 024"  # scripted group (container) (typed FeaturePython)
  n = 2
  ref = C_element
FEATURE [App::DocumentObjectGroupPython] H_element038  label="H_element : 020"  # scripted group (container) (typed FeaturePython)
  n = 4
  ref = H_element
FEATURE [App::DocumentObjectGroupPython] G4_ETHYLENE  # scripted group (container) (typed FeaturePython)
  Dunit = g/cm3
  Dvalue = 0.00117497
  Group = -> [C_element041,H_element038]
  conduct = 2
  density = 1
  expand = 3
  formula = G4_ETHYLENE
  name = G4_ETHYLENE
  specific = 4
FEATURE [App::DocumentObjectGroupPython] H_element039  label="H_element : 0.096"  # scripted group (container) (typed FeaturePython)
  n = 0.096
FEATURE [App::DocumentObjectGroupPython] C_element042  label="C_element : 0.195"  # scripted group (container) (typed FeaturePython)
  n = 0.195
FEATURE [App::DocumentObjectGroupPython] N_element016  label="N_element : 0.057"  # scripted group (container) (typed FeaturePython)
  n = 0.057
FEATURE [App::DocumentObjectGroupPython] O_element037  label="O_element : 0.646"  # scripted group (container) (typed FeaturePython)
  n = 0.646
FEATURE [App::DocumentObjectGroupPython] Na_element006  label="Na_element : 0.017"  # scripted group (container) (typed FeaturePython)
  n = 0.001
FEATURE [App::DocumentObjectGroupPython] P_element005  label="P_element : 0.104"  # scripted group (container) (typed FeaturePython)
  n = 0.001
FEATURE [App::DocumentObjectGroupPython] S_element010  label="S_element : 0.016"  # scripted group (container) (typed FeaturePython)
  n = 0.003
FEATURE [App::DocumentObjectGroupPython] Cl_element010  label="Cl_element : 0.005"  # scripted group (container) (typed FeaturePython)
  n = 0.001
FEATURE [App::DocumentObjectGroupPython] G4_EYE_LENS_ICRP  # scripted group (container) (typed FeaturePython)
  Dunit = g/cm3
  Dvalue = 1.07
  Group = -> [H_element039,C_element042,N_element016,O_element037,Na_element006,P_element005,S_element010,Cl_element010]
  conduct = 2
  density = 1
  expand = 3
  formula = G4_EYE_LENS_ICRP
  name = G4_EYE_LENS_ICRP
  specific = 4
FEATURE [App::DocumentObjectGroupPython] Fe_element003  label="Fe_element : 2"  # scripted group (container) (typed FeaturePython)
  n = 2
  ref = Fe_element
FEATURE [App::DocumentObjectGroupPython] O_element038  label="O_element : 019"  # scripted group (container) (typed FeaturePython)
  n = 3
  ref = O_element
FEATURE [App::DocumentObjectGroupPython] G4_FERRIC_OXIDE  # scripted group (container) (typed FeaturePython)
  Dunit = g/cm3
  Dvalue = 5.2
  Group = -> [Fe_element003,O_element038]
  conduct = 2
  density = 1
  expand = 3
  formula = G4_FERRIC_OXIDE
  name = G4_FERRIC_OXIDE
  specific = 4
FEATURE [App::DocumentObjectGroupPython] Fe_element004  label="Fe_element : 1"  # scripted group (container) (typed FeaturePython)
  n = 1
  ref = Fe_element
FEATURE [App::DocumentObjectGroupPython] B_element003  label="B_element : 1"  # scripted group (container) (typed FeaturePython)
  n = 1
  ref = B_element
FEATURE [App::DocumentObjectGroupPython] G4_FERROBORIDE  # scripted group (container) (typed FeaturePython)
  Dunit = g/cm3
  Dvalue = 7.15
  Group = -> [Fe_element004,B_element003]
  conduct = 2
  density = 1
  expand = 3
  formula = G4_FERROBORIDE
  name = G4_FERROBORIDE
  specific = 4
FEATURE [App::DocumentObjectGroupPython] Fe_element005  label="Fe_element : 003"  # scripted group (container) (typed FeaturePython)
  n = 1
  ref = Fe_element
FEATURE [App::DocumentObjectGroupPython] O_element039  label="O_element : 020"  # scripted group (container) (typed FeaturePython)
  n = 1
  ref = O_element
FEATURE [App::DocumentObjectGroupPython] G4_FERROUS_OXIDE  # scripted group (container) (typed FeaturePython)
  Dunit = g/cm3
  Dvalue = 5.7
  Group = -> [Fe_element005,O_element039]
  conduct = 2
  density = 1
  expand = 3
  formula = G4_FERROUS_OXIDE
  name = G4_FERROUS_OXIDE
  specific = 4
FEATURE [App::DocumentObjectGroupPython] H_element040  label="H_element : 0.115"  # scripted group (container) (typed FeaturePython)
  n = 0.108259
FEATURE [App::DocumentObjectGroupPython] N_element017  label="N_element : 0.000"  # scripted group (container) (typed FeaturePython)
  n = 2.7e-05
FEATURE [App::DocumentObjectGroupPython] O_element040  label="O_element : 0.879"  # scripted group (container) (typed FeaturePython)
  n = 0.878636
FEATURE [App::DocumentObjectGroupPython] Na_element007  label="Na_element : 0.000"  # scripted group (container) (typed FeaturePython)
  n = 2.2e-05
FEATURE [App::DocumentObjectGroupPython] S_element011  label="S_element : 0.013"  # scripted group (container) (typed FeaturePython)
  n = 0.012968
FEATURE [App::DocumentObjectGroupPython] Cl_element011  label="Cl_element : 0.000"  # scripted group (container) (typed FeaturePython)
  n = 3.4e-05
FEATURE [App::DocumentObjectGroupPython] Fe_element006  label="Fe_element : 0.000"  # scripted group (container) (typed FeaturePython)
  n = 5.4e-05
FEATURE [App::DocumentObjectGroupPython] G4_FERROUS_SULFATE  # scripted group (container) (typed FeaturePython)
  Dunit = g/cm3
  Dvalue = 1.024
  Group = -> [H_element040,N_element017,O_element040,Na_element007,S_element011,Cl_element011,Fe_element006]
  conduct = 2
  density = 1
  expand = 3
  formula = G4_FERROUS_SULFATE
  name = G4_FERROUS_SULFATE
  specific = 4
FEATURE [App::DocumentObjectGroupPython] C_element043  label="C_element : 0.099"  # scripted group (container) (typed FeaturePython)
  n = 0.099335
FEATURE [App::DocumentObjectGroupPython] F_element007  label="F_element : 0.314"  # scripted group (container) (typed FeaturePython)
  n = 0.314247
FEATURE [App::DocumentObjectGroupPython] Cl_element012  label="Cl_element : 0.586"  # scripted group (container) (typed FeaturePython)
  n = 0.586418
FEATURE [App::DocumentObjectGroupPython] G4_FREON_12  label="G4_FREON-12"  # scripted group (container) (typed FeaturePython)
  Dunit = g/cm3
  Dvalue = 1.12
  Group = -> [C_element043,F_element007,Cl_element012]
  conduct = 2
  density = 1
  expand = 3
  formula = G4_FREON-12
  name = G4_FREON-12
  specific = 4
FEATURE [App::DocumentObjectGroupPython] C_element044  label="C_element : 0.057"  # scripted group (container) (typed FeaturePython)
  n = 0.057245
FEATURE [App::DocumentObjectGroupPython] F_element008  label="F_element : 0.181"  # scripted group (container) (typed FeaturePython)
  n = 0.181096
FEATURE [App::DocumentObjectGroupPython] Br_element001  label="Br_element : 0.762"  # scripted group (container) (typed FeaturePython)
  n = 0.761659
FEATURE [App::DocumentObjectGroupPython] G4_FREON_12B2  label="G4_FREON-12B2"  # scripted group (container) (typed FeaturePython)
  Dunit = g/cm3
  Dvalue = 1.8
  Group = -> [C_element044,F_element008,Br_element001]
  conduct = 2
  density = 1
  expand = 3
  formula = G4_FREON-12B2
  name = G4_FREON-12B2
  specific = 4
FEATURE [App::DocumentObjectGroupPython] C_element045  label="C_element : 0.115"  # scripted group (container) (typed FeaturePython)
  n = 0.114983
FEATURE [App::DocumentObjectGroupPython] F_element009  label="F_element : 0.546"  # scripted group (container) (typed FeaturePython)
  n = 0.545621
FEATURE [App::DocumentObjectGroupPython] Cl_element013  label="Cl_element : 0.339"  # scripted group (container) (typed FeaturePython)
  n = 0.339396
FEATURE [App::DocumentObjectGroupPython] G4_FREON_13  label="G4_FREON-13"  # scripted group (container) (typed FeaturePython)
  Dunit = g/cm3
  Dvalue = 0.95
  Group = -> [C_element045,F_element009,Cl_element013]
  conduct = 2
  density = 1
  expand = 3
  formula = G4_FREON-13
  name = G4_FREON-13
  specific = 4
FEATURE [App::DocumentObjectGroupPython] C_element046  label="C_element : 025"  # scripted group (container) (typed FeaturePython)
  n = 1
  ref = C_element
FEATURE [App::DocumentObjectGroupPython] F_element010  label="F_element : 3"  # scripted group (container) (typed FeaturePython)
  n = 3
  ref = F_element
FEATURE [App::DocumentObjectGroupPython] Br_element002  label="Br_element : 1"  # scripted group (container) (typed FeaturePython)
  n = 1
  ref = Br_element
FEATURE [App::DocumentObjectGroupPython] G4_FREON_13B1  label="G4_FREON-13B1"  # scripted group (container) (typed FeaturePython)
  Dunit = g/cm3
  Dvalue = 1.5
  Group = -> [C_element046,F_element010,Br_element002]
  conduct = 2
  density = 1
  expand = 3
  formula = G4_FREON-13B1
  name = G4_FREON-13B1
  specific = 4
FEATURE [App::DocumentObjectGroupPython] C_element047  label="C_element : 0.061"  # scripted group (container) (typed FeaturePython)
  n = 0.061309
FEATURE [App::DocumentObjectGroupPython] F_element011  label="F_element : 0.291"  # scripted group (container) (typed FeaturePython)
  n = 0.290924
FEATURE [App::DocumentObjectGroupPython] I_element002  label="I_element : 0.648"  # scripted group (container) (typed FeaturePython)
  n = 0.647767
FEATURE [App::DocumentObjectGroupPython] G4_FREON_13I1  label="G4_FREON-13I1"  # scripted group (container) (typed FeaturePython)
  Dunit = g/cm3
  Dvalue = 1.8
  Group = -> [C_element047,F_element011,I_element002]
  conduct = 2
  density = 1
  expand = 3
  formula = G4_FREON-13I1
  name = G4_FREON-13I1
  specific = 4
FEATURE [App::DocumentObjectGroupPython] Gd_element001  label="Gd_element : 2"  # scripted group (container) (typed FeaturePython)
  n = 2
  ref = Gd_element
FEATURE [App::DocumentObjectGroupPython] O_element041  label="O_element : 021"  # scripted group (container) (typed FeaturePython)
  n = 2
  ref = O_element
FEATURE [App::DocumentObjectGroupPython] S_element012  label="S_element : 004"  # scripted group (container) (typed FeaturePython)
  n = 1
  ref = S_element
FEATURE [App::DocumentObjectGroupPython] G4_GADOLINIUM_OXYSULFIDE  # scripted group (container) (typed FeaturePython)
  Dunit = g/cm3
  Dvalue = 7.44
  Group = -> [Gd_element001,O_element041,S_element012]
  conduct = 2
  density = 1
  expand = 3
  formula = G4_GADOLINIUM_OXYSULFIDE
  name = G4_GADOLINIUM_OXYSULFIDE
  specific = 4
FEATURE [App::DocumentObjectGroupPython] Ga_element001  label="Ga_element : 1"  # scripted group (container) (typed FeaturePython)
  n = 1
  ref = Ga_element
FEATURE [App::DocumentObjectGroupPython] As_element001  label="As_element : 1"  # scripted group (container) (typed FeaturePython)
  n = 1
  ref = As_element
FEATURE [App::DocumentObjectGroupPython] G4_GALLIUM_ARSENIDE  # scripted group (container) (typed FeaturePython)
  Dunit = g/cm3
  Dvalue = 5.31
  Group = -> [Ga_element001,As_element001]
  conduct = 2
  density = 1
  expand = 3
  formula = G4_GALLIUM_ARSENIDE
  name = G4_GALLIUM_ARSENIDE
  specific = 4
FEATURE [App::DocumentObjectGroupPython] H_element041  label="H_element : 0.081"  # scripted group (container) (typed FeaturePython)
  n = 0.08118
FEATURE [App::DocumentObjectGroupPython] C_element048  label="C_element : 0.416"  # scripted group (container) (typed FeaturePython)
  n = 0.41606
FEATURE [App::DocumentObjectGroupPython] N_element018  label="N_element : 0.111"  # scripted group (container) (typed FeaturePython)
  n = 0.11124
FEATURE [App::DocumentObjectGroupPython] O_element042  label="O_element : 0.381"  # scripted group (container) (typed FeaturePython)
  n = 0.38064
FEATURE [App::DocumentObjectGroupPython] S_element013  label="S_element : 0.011"  # scripted group (container) (typed FeaturePython)
  n = 0.01088
FEATURE [App::DocumentObjectGroupPython] G4_GEL_PHOTO_EMULSION  # scripted group (container) (typed FeaturePython)
  Dunit = g/cm3
  Dvalue = 1.2914
  Group = -> [H_element041,C_element048,N_element018,O_element042,S_element013]
  conduct = 2
  density = 1
  expand = 3
  formula = G4_GEL_PHOTO_EMULSION
  name = G4_GEL_PHOTO_EMULSION
  specific = 4
FEATURE [App::DocumentObjectGroupPython] B_element004  label="B_element : 0.040"  # scripted group (container) (typed FeaturePython)
  n = 0.0400639
FEATURE [App::DocumentObjectGroupPython] O_element043  label="O_element : 0.540"  # scripted group (container) (typed FeaturePython)
  n = 0.539561
FEATURE [App::DocumentObjectGroupPython] Na_element008  label="Na_element : 0.028"  # scripted group (container) (typed FeaturePython)
  n = 0.0281909
FEATURE [App::DocumentObjectGroupPython] Al_element003  label="Al_element : 0.012"  # scripted group (container) (typed FeaturePython)
  n = 0.011644
FEATURE [App::DocumentObjectGroupPython] Si_element003  label="Si_element : 0.377"  # scripted group (container) (typed FeaturePython)
  n = 0.377219
FEATURE [App::DocumentObjectGroupPython] K_element004  label="K_element : 0.014"  # scripted group (container) (typed FeaturePython)
  n = 0.00332099
FEATURE [App::DocumentObjectGroupPython] G4_Pyrex_Glass  # scripted group (container) (typed FeaturePython)
  Dunit = g/cm3
  Dvalue = 2.23
  Group = -> [B_element004,O_element043,Na_element008,Al_element003,Si_element003,K_element004]
  conduct = 2
  density = 1
  expand = 3
  formula = G4_Pyrex_Glass
  name = G4_Pyrex_Glass
  specific = 4
FEATURE [App::DocumentObjectGroupPython] O_element044  label="O_element : 0.156"  # scripted group (container) (typed FeaturePython)
  n = 0.156453
FEATURE [App::DocumentObjectGroupPython] Si_element004  label="Si_element : 0.081"  # scripted group (container) (typed FeaturePython)
  n = 0.080866
FEATURE [App::DocumentObjectGroupPython] Ti_element001  label="Ti_element : 0.008"  # scripted group (container) (typed FeaturePython)
  n = 0.008092
FEATURE [App::DocumentObjectGroupPython] As_element002  label="As_element : 0.003"  # scripted group (container) (typed FeaturePython)
  n = 0.002651
FEATURE [App::DocumentObjectGroupPython] Pb_element001  label="Pb_element : 0.752"  # scripted group (container) (typed FeaturePython)
  n = 0.751938
FEATURE [App::DocumentObjectGroupPython] G4_GLASS_LEAD  # scripted group (container) (typed FeaturePython)
  Dunit = g/cm3
  Dvalue = 6.22
  Group = -> [O_element044,Si_element004,Ti_element001,As_element002,Pb_element001]
  conduct = 2
  density = 1
  expand = 3
  formula = G4_GLASS_LEAD
  name = G4_GLASS_LEAD
  specific = 4
FEATURE [App::DocumentObjectGroupPython] O_element045  label="O_element : 0.460"  # scripted group (container) (typed FeaturePython)
  n = 0.4598
FEATURE [App::DocumentObjectGroupPython] Na_element009  label="Na_element : 0.096"  # scripted group (container) (typed FeaturePython)
  n = 0.0964411
FEATURE [App::DocumentObjectGroupPython] Si_element005  label="Si_element : 0.378"  # scripted group (container) (typed FeaturePython)
  n = 0.336553
FEATURE [App::DocumentObjectGroupPython] Ca_element011  label="Ca_element : 0.107"  # scripted group (container) (typed FeaturePython)
  n = 0.107205
FEATURE [App::DocumentObjectGroupPython] G4_GLASS_PLATE  # scripted group (container) (typed FeaturePython)
  Dunit = g/cm3
  Dvalue = 2.4
  Group = -> [O_element045,Na_element009,Si_element005,Ca_element011]
  conduct = 2
  density = 1
  expand = 3
  formula = G4_GLASS_PLATE
  name = G4_GLASS_PLATE
  specific = 4
FEATURE [App::DocumentObjectGroupPython] C_element049  label="C_element : 026"  # scripted group (container) (typed FeaturePython)
  n = 5
  ref = C_element
FEATURE [App::DocumentObjectGroupPython] H_element042  label="H_element : 021"  # scripted group (container) (typed FeaturePython)
  n = 10
  ref = H_element
FEATURE [App::DocumentObjectGroupPython] N_element019  label="N_element : 2"  # scripted group (container) (typed FeaturePython)
  n = 2
  ref = N_element
FEATURE [App::DocumentObjectGroupPython] O_element046  label="O_element : 022"  # scripted group (container) (typed FeaturePython)
  n = 3
  ref = O_element
FEATURE [App::DocumentObjectGroupPython] G4_GLUTAMINE  # scripted group (container) (typed FeaturePython)
  Dunit = g/cm3
  Dvalue = 1.46
  Group = -> [C_element049,H_element042,N_element019,O_element046]
  conduct = 2
  density = 1
  expand = 3
  formula = G4_GLUTAMINE
  name = G4_GLUTAMINE
  specific = 4
FEATURE [App::DocumentObjectGroupPython] C_element050  label="C_element : 027"  # scripted group (container) (typed FeaturePython)
  n = 3
  ref = C_element
FEATURE [App::DocumentObjectGroupPython] H_element043  label="H_element : 022"  # scripted group (container) (typed FeaturePython)
  n = 8
  ref = H_element
FEATURE [App::DocumentObjectGroupPython] O_element047  label="O_element : 023"  # scripted group (container) (typed FeaturePython)
  n = 3
  ref = O_element
FEATURE [App::DocumentObjectGroupPython] G4_GLYCEROL  # scripted group (container) (typed FeaturePython)
  Dunit = g/cm3
  Dvalue = 1.2613
  Group = -> [C_element050,H_element043,O_element047]
  conduct = 2
  density = 1
  expand = 3
  formula = G4_GLYCEROL
  name = G4_GLYCEROL
  specific = 4
FEATURE [App::DocumentObjectGroupPython] C_element051  label="C_element : 028"  # scripted group (container) (typed FeaturePython)
  n = 5
  ref = C_element
FEATURE [App::DocumentObjectGroupPython] H_element044  label="H_element : 023"  # scripted group (container) (typed FeaturePython)
  n = 5
  ref = H_element
FEATURE [App::DocumentObjectGroupPython] N_element020  label="N_element : 009"  # scripted group (container) (typed FeaturePython)
  n = 5
  ref = N_element
FEATURE [App::DocumentObjectGroupPython] O_element048  label="O_element : 024"  # scripted group (container) (typed FeaturePython)
  n = 1
  ref = O_element
FEATURE [App::DocumentObjectGroupPython] G4_GUANINE  # scripted group (container) (typed FeaturePython)
  Dunit = g/cm3
  Dvalue = 2.2
  Group = -> [C_element051,H_element044,N_element020,O_element048]
  conduct = 2
  density = 1
  expand = 3
  formula = G4_GUANINE
  name = G4_GUANINE
  specific = 4
FEATURE [App::DocumentObjectGroupPython] Ca_element012  label="Ca_element : 006"  # scripted group (container) (typed FeaturePython)
  n = 1
  ref = Ca_element
FEATURE [App::DocumentObjectGroupPython] S_element014  label="S_element : 005"  # scripted group (container) (typed FeaturePython)
  n = 1
  ref = S_element
FEATURE [App::DocumentObjectGroupPython] O_element049  label="O_element : 6"  # scripted group (container) (typed FeaturePython)
  n = 6
  ref = O_element
FEATURE [App::DocumentObjectGroupPython] H_element045  label="H_element : 024"  # scripted group (container) (typed FeaturePython)
  n = 4
  ref = H_element
FEATURE [App::DocumentObjectGroupPython] G4_GYPSUM  # scripted group (container) (typed FeaturePython)
  Dunit = g/cm3
  Dvalue = 2.32
  Group = -> [Ca_element012,S_element014,O_element049,H_element045]
  conduct = 2
  density = 1
  expand = 3
  formula = G4_GYPSUM
  name = G4_GYPSUM
  specific = 4
FEATURE [App::DocumentObjectGroupPython] C_element052  label="C_element : 7"  # scripted group (container) (typed FeaturePython)
  n = 7
  ref = C_element
FEATURE [App::DocumentObjectGroupPython] H_element046  label="H_element : 16"  # scripted group (container) (typed FeaturePython)
  n = 16
  ref = H_element
FEATURE [App::DocumentObjectGroupPython] G4_N_HEPTANE  label="G4_N-HEPTANE"  # scripted group (container) (typed FeaturePython)
  Dunit = g/cm3
  Dvalue = 0.68376
  Group = -> [C_element052,H_element046]
  conduct = 2
  density = 1
  expand = 3
  formula = G4_N-HEPTANE
  name = G4_N-HEPTANE
  specific = 4
FEATURE [App::DocumentObjectGroupPython] C_element053  label="C_element : 029"  # scripted group (container) (typed FeaturePython)
  n = 6
  ref = C_element
FEATURE [App::DocumentObjectGroupPython] H_element047  label="H_element : 14"  # scripted group (container) (typed FeaturePython)
  n = 14
  ref = H_element
FEATURE [App::DocumentObjectGroupPython] G4_N_HEXANE  label="G4_N-HEXANE"  # scripted group (container) (typed FeaturePython)
  Dunit = g/cm3
  Dvalue = 0.6603
  Group = -> [C_element053,H_element047]
  conduct = 2
  density = 1
  expand = 3
  formula = G4_N-HEXANE
  name = G4_N-HEXANE
  specific = 4
FEATURE [App::DocumentObjectGroupPython] C_element054  label="C_element : 22"  # scripted group (container) (typed FeaturePython)
  n = 22
  ref = C_element
FEATURE [App::DocumentObjectGroupPython] H_element048  label="H_element : 025"  # scripted group (container) (typed FeaturePython)
  n = 10
  ref = H_element
FEATURE [App::DocumentObjectGroupPython] N_element021  label="N_element : 010"  # scripted group (container) (typed FeaturePython)
  n = 2
  ref = N_element
FEATURE [App::DocumentObjectGroupPython] O_element050  label="O_element : 025"  # scripted group (container) (typed FeaturePython)
  n = 5
  ref = O_element
FEATURE [App::DocumentObjectGroupPython] G4_KAPTON  # scripted group (container) (typed FeaturePython)
  Dunit = g/cm3
  Dvalue = 1.42
  Group = -> [C_element054,H_element048,N_element021,O_element050]
  conduct = 2
  density = 1
  expand = 3
  formula = G4_KAPTON
  name = G4_KAPTON
  specific = 4
FEATURE [App::DocumentObjectGroupPython] La_element001  label="La_element : 1"  # scripted group (container) (typed FeaturePython)
  n = 1
  ref = La_element
FEATURE [App::DocumentObjectGroupPython] Br_element003  label="Br_element : 002"  # scripted group (container) (typed FeaturePython)
  n = 1
  ref = Br_element
FEATURE [App::DocumentObjectGroupPython] O_element051  label="O_element : 026"  # scripted group (container) (typed FeaturePython)
  n = 1
  ref = O_element
FEATURE [App::DocumentObjectGroupPython] G4_LANTHANUM_OXYBROMIDE  # scripted group (container) (typed FeaturePython)
  Dunit = g/cm3
  Dvalue = 6.28
  Group = -> [La_element001,Br_element003,O_element051]
  conduct = 2
  density = 1
  expand = 3
  formula = G4_LANTHANUM_OXYBROMIDE
  name = G4_LANTHANUM_OXYBROMIDE
  specific = 4
FEATURE [App::DocumentObjectGroupPython] La_element002  label="La_element : 2"  # scripted group (container) (typed FeaturePython)
  n = 2
  ref = La_element
FEATURE [App::DocumentObjectGroupPython] O_element052  label="O_element : 027"  # scripted group (container) (typed FeaturePython)
  n = 2
  ref = O_element
FEATURE [App::DocumentObjectGroupPython] S_element015  label="S_element : 006"  # scripted group (container) (typed FeaturePython)
  n = 1
  ref = S_element
FEATURE [App::DocumentObjectGroupPython] G4_LANTHANUM_OXYSULFIDE  # scripted group (container) (typed FeaturePython)
  Dunit = g/cm3
  Dvalue = 5.86
  Group = -> [La_element002,O_element052,S_element015]
  conduct = 2
  density = 1
  expand = 3
  formula = G4_LANTHANUM_OXYSULFIDE
  name = G4_LANTHANUM_OXYSULFIDE
  specific = 4
FEATURE [App::DocumentObjectGroupPython] O_element053  label="O_element : 0.072"  # scripted group (container) (typed FeaturePython)
  n = 0.071682
FEATURE [App::DocumentObjectGroupPython] Pb_element002  label="Pb_element : 0.928"  # scripted group (container) (typed FeaturePython)
  n = 0.928318
FEATURE [App::DocumentObjectGroupPython] G4_LEAD_OXIDE  # scripted group (container) (typed FeaturePython)
  Dunit = g/cm3
  Dvalue = 9.53
  Group = -> [O_element053,Pb_element002]
  conduct = 2
  density = 1
  expand = 3
  formula = G4_LEAD_OXIDE
  name = G4_LEAD_OXIDE
  specific = 4
FEATURE [App::DocumentObjectGroupPython] Li_element001  label="Li_element : 1"  # scripted group (container) (typed FeaturePython)
  n = 1
  ref = Li_element
FEATURE [App::DocumentObjectGroupPython] N_element022  label="N_element : 011"  # scripted group (container) (typed FeaturePython)
  n = 1
  ref = N_element
FEATURE [App::DocumentObjectGroupPython] H_element049  label="H_element : 026"  # scripted group (container) (typed FeaturePython)
  n = 2
  ref = H_element
FEATURE [App::DocumentObjectGroupPython] G4_LITHIUM_AMIDE  # scripted group (container) (typed FeaturePython)
  Dunit = g/cm3
  Dvalue = 1.178
  Group = -> [Li_element001,N_element022,H_element049]
  conduct = 2
  density = 1
  expand = 3
  formula = G4_LITHIUM_AMIDE
  name = G4_LITHIUM_AMIDE
  specific = 4
FEATURE [App::DocumentObjectGroupPython] Li_element002  label="Li_element : 2"  # scripted group (container) (typed FeaturePython)
  n = 2
  ref = Li_element
FEATURE [App::DocumentObjectGroupPython] C_element055  label="C_element : 030"  # scripted group (container) (typed FeaturePython)
  n = 1
  ref = C_element
FEATURE [App::DocumentObjectGroupPython] O_element054  label="O_element : 028"  # scripted group (container) (typed FeaturePython)
  n = 3
  ref = O_element
FEATURE [App::DocumentObjectGroupPython] G4_LITHIUM_CARBONATE  # scripted group (container) (typed FeaturePython)
  Dunit = g/cm3
  Dvalue = 2.11
  Group = -> [Li_element002,C_element055,O_element054]
  conduct = 2
  density = 1
  expand = 3
  formula = G4_LITHIUM_CARBONATE
  name = G4_LITHIUM_CARBONATE
  specific = 4
FEATURE [App::DocumentObjectGroupPython] Li_element003  label="Li_element : 003"  # scripted group (container) (typed FeaturePython)
  n = 1
  ref = Li_element
FEATURE [App::DocumentObjectGroupPython] F_element012  label="F_element : 004"  # scripted group (container) (typed FeaturePython)
  n = 1
  ref = F_element
FEATURE [App::DocumentObjectGroupPython] G4_LITHIUM_FLUORIDE  # scripted group (container) (typed FeaturePython)
  Dunit = g/cm3
  Dvalue = 2.635
  Group = -> [Li_element003,F_element012]
  conduct = 2
  density = 1
  expand = 3
  formula = G4_LITHIUM_FLUORIDE
  name = G4_LITHIUM_FLUORIDE
  specific = 4
FEATURE [App::DocumentObjectGroupPython] Li_element004  label="Li_element : 004"  # scripted group (container) (typed FeaturePython)
  n = 1
  ref = Li_element
FEATURE [App::DocumentObjectGroupPython] H_element050  label="H_element : 027"  # scripted group (container) (typed FeaturePython)
  n = 1
  ref = H_element
FEATURE [App::DocumentObjectGroupPython] G4_LITHIUM_HYDRIDE  # scripted group (container) (typed FeaturePython)
  Dunit = g/cm3
  Dvalue = 0.82
  Group = -> [Li_element004,H_element050]
  conduct = 2
  density = 1
  expand = 3
  formula = G4_LITHIUM_HYDRIDE
  name = G4_LITHIUM_HYDRIDE
  specific = 4
FEATURE [App::DocumentObjectGroupPython] Li_element005  label="Li_element : 005"  # scripted group (container) (typed FeaturePython)
  n = 1
  ref = Li_element
FEATURE [App::DocumentObjectGroupPython] I_element003  label="I_element : 002"  # scripted group (container) (typed FeaturePython)
  n = 1
  ref = I_element
FEATURE [App::DocumentObjectGroupPython] G4_LITHIUM_IODIDE  # scripted group (container) (typed FeaturePython)
  Dunit = g/cm3
  Dvalue = 3.494
  Group = -> [Li_element005,I_element003]
  conduct = 2
  density = 1
  expand = 3
  formula = G4_LITHIUM_IODIDE
  name = G4_LITHIUM_IODIDE
  specific = 4
FEATURE [App::DocumentObjectGroupPython] Li_element006  label="Li_element : 006"  # scripted group (container) (typed FeaturePython)
  n = 2
  ref = Li_element
FEATURE [App::DocumentObjectGroupPython] O_element055  label="O_element : 029"  # scripted group (container) (typed FeaturePython)
  n = 1
  ref = O_element
FEATURE [App::DocumentObjectGroupPython] G4_LITHIUM_OXIDE  # scripted group (container) (typed FeaturePython)
  Dunit = g/cm3
  Dvalue = 2.013
  Group = -> [Li_element006,O_element055]
  conduct = 2
  density = 1
  expand = 3
  formula = G4_LITHIUM_OXIDE
  name = G4_LITHIUM_OXIDE
  specific = 4
FEATURE [App::DocumentObjectGroupPython] Li_element007  label="Li_element : 007"  # scripted group (container) (typed FeaturePython)
  n = 2
  ref = Li_element
FEATURE [App::DocumentObjectGroupPython] B_element005  label="B_element : 005"  # scripted group (container) (typed FeaturePython)
  n = 4
  ref = B_element
FEATURE [App::DocumentObjectGroupPython] O_element056  label="O_element : 7"  # scripted group (container) (typed FeaturePython)
  n = 7
  ref = O_element
FEATURE [App::DocumentObjectGroupPython] G4_LITHIUM_TETRABORATE  # scripted group (container) (typed FeaturePython)
  Dunit = g/cm3
  Dvalue = 2.44
  Group = -> [Li_element007,B_element005,O_element056]
  conduct = 2
  density = 1
  expand = 3
  formula = G4_LITHIUM_TETRABORATE
  name = G4_LITHIUM_TETRABORATE
  specific = 4
FEATURE [App::DocumentObjectGroupPython] H_element051  label="H_element : 0.105"  # scripted group (container) (typed FeaturePython)
  n = 0.105
FEATURE [App::DocumentObjectGroupPython] C_element056  label="C_element : 0.083"  # scripted group (container) (typed FeaturePython)
  n = 0.083
FEATURE [App::DocumentObjectGroupPython] N_element023  label="N_element : 0.023"  # scripted group (container) (typed FeaturePython)
  n = 0.023
FEATURE [App::DocumentObjectGroupPython] O_element057  label="O_element : 0.779"  # scripted group (container) (typed FeaturePython)
  n = 0.779
FEATURE [App::DocumentObjectGroupPython] Na_element010  label="Na_element : 0.097"  # scripted group (container) (typed FeaturePython)
  n = 0.002
FEATURE [App::DocumentObjectGroupPython] P_element006  label="P_element : 0.105"  # scripted group (container) (typed FeaturePython)
  n = 0.001
FEATURE [App::DocumentObjectGroupPython] S_element016  label="S_element : 0.017"  # scripted group (container) (typed FeaturePython)
  n = 0.002
FEATURE [App::DocumentObjectGroupPython] Cl_element014  label="Cl_element : 0.587"  # scripted group (container) (typed FeaturePython)
  n = 0.003
FEATURE [App::DocumentObjectGroupPython] K_element005  label="K_element : 0.015"  # scripted group (container) (typed FeaturePython)
  n = 0.002
FEATURE [App::DocumentObjectGroupPython] G4_LUNG_ICRP  # scripted group (container) (typed FeaturePython)
  Dunit = g/cm3
  Dvalue = 1.04
  Group = -> [H_element051,C_element056,N_element023,O_element057,Na_element010,P_element006,S_element016,Cl_element014,K_element005]
  conduct = 2
  density = 1
  expand = 3
  formula = G4_LUNG_ICRP
  name = G4_LUNG_ICRP
  specific = 4
FEATURE [App::DocumentObjectGroupPython] H_element052  label="H_element : 0.116"  # scripted group (container) (typed FeaturePython)
  n = 0.114318
FEATURE [App::DocumentObjectGroupPython] C_element057  label="C_element : 0.656"  # scripted group (container) (typed FeaturePython)
  n = 0.655824
FEATURE [App::DocumentObjectGroupPython] O_element058  label="O_element : 0.092"  # scripted group (container) (typed FeaturePython)
  n = 0.0921831
FEATURE [App::DocumentObjectGroupPython] Mg_element004  label="Mg_element : 0.135"  # scripted group (container) (typed FeaturePython)
  n = 0.134792
FEATURE [App::DocumentObjectGroupPython] Ca_element013  label="Ca_element : 0.003"  # scripted group (container) (typed FeaturePython)
  n = 0.002883
FEATURE [App::DocumentObjectGroupPython] G4_M3_WAX  # scripted group (container) (typed FeaturePython)
  Dunit = g/cm3
  Dvalue = 1.05
  Group = -> [H_element052,C_element057,O_element058,Mg_element004,Ca_element013]
  conduct = 2
  density = 1
  expand = 3
  formula = G4_M3_WAX
  name = G4_M3_WAX
  specific = 4
FEATURE [App::DocumentObjectGroupPython] Mg_element005  label="Mg_element : 1"  # scripted group (container) (typed FeaturePython)
  n = 1
  ref = Mg_element
FEATURE [App::DocumentObjectGroupPython] C_element058  label="C_element : 031"  # scripted group (container) (typed FeaturePython)
  n = 1
  ref = C_element
FEATURE [App::DocumentObjectGroupPython] O_element059  label="O_element : 030"  # scripted group (container) (typed FeaturePython)
  n = 3
  ref = O_element
FEATURE [App::DocumentObjectGroupPython] G4_MAGNESIUM_CARBONATE  # scripted group (container) (typed FeaturePython)
  Dunit = g/cm3
  Dvalue = 2.958
  Group = -> [Mg_element005,C_element058,O_element059]
  conduct = 2
  density = 1
  expand = 3
  formula = G4_MAGNESIUM_CARBONATE
  name = G4_MAGNESIUM_CARBONATE
  specific = 4
FEATURE [App::DocumentObjectGroupPython] Mg_element006  label="Mg_element : 002"  # scripted group (container) (typed FeaturePython)
  n = 1
  ref = Mg_element
FEATURE [App::DocumentObjectGroupPython] F_element013  label="F_element : 005"  # scripted group (container) (typed FeaturePython)
  n = 2
  ref = F_element
FEATURE [App::DocumentObjectGroupPython] G4_MAGNESIUM_FLUORIDE  # scripted group (container) (typed FeaturePython)
  Dunit = g/cm3
  Dvalue = 3
  Group = -> [Mg_element006,F_element013]
  conduct = 2
  density = 1
  expand = 3
  formula = G4_MAGNESIUM_FLUORIDE
  name = G4_MAGNESIUM_FLUORIDE
  specific = 4
FEATURE [App::DocumentObjectGroupPython] Mg_element007  label="Mg_element : 003"  # scripted group (container) (typed FeaturePython)
  n = 1
  ref = Mg_element
FEATURE [App::DocumentObjectGroupPython] O_element060  label="O_element : 031"  # scripted group (container) (typed FeaturePython)
  n = 1
  ref = O_element
FEATURE [App::DocumentObjectGroupPython] G4_MAGNESIUM_OXIDE  # scripted group (container) (typed FeaturePython)
  Dunit = g/cm3
  Dvalue = 3.58
  Group = -> [Mg_element007,O_element060]
  conduct = 2
  density = 1
  expand = 3
  formula = G4_MAGNESIUM_OXIDE
  name = G4_MAGNESIUM_OXIDE
  specific = 4
FEATURE [App::DocumentObjectGroupPython] Mg_element008  label="Mg_element : 004"  # scripted group (container) (typed FeaturePython)
  n = 1
  ref = Mg_element
FEATURE [App::DocumentObjectGroupPython] B_element006  label="B_element : 006"  # scripted group (container) (typed FeaturePython)
  n = 4
  ref = B_element
FEATURE [App::DocumentObjectGroupPython] O_element061  label="O_element : 032"  # scripted group (container) (typed FeaturePython)
  n = 7
  ref = O_element
FEATURE [App::DocumentObjectGroupPython] G4_MAGNESIUM_TETRABORATE  # scripted group (container) (typed FeaturePython)
  Dunit = g/cm3
  Dvalue = 2.53
  Group = -> [Mg_element008,B_element006,O_element061]
  conduct = 2
  density = 1
  expand = 3
  formula = G4_MAGNESIUM_TETRABORATE
  name = G4_MAGNESIUM_TETRABORATE
  specific = 4
FEATURE [App::DocumentObjectGroupPython] Hg_element001  label="Hg_element : 1"  # scripted group (container) (typed FeaturePython)
  n = 1
  ref = Hg_element
FEATURE [App::DocumentObjectGroupPython] I_element004  label="I_element : 2"  # scripted group (container) (typed FeaturePython)
  n = 2
  ref = I_element
FEATURE [App::DocumentObjectGroupPython] G4_MERCURIC_IODIDE  # scripted group (container) (typed FeaturePython)
  Dunit = g/cm3
  Dvalue = 6.36
  Group = -> [Hg_element001,I_element004]
  conduct = 2
  density = 1
  expand = 3
  formula = G4_MERCURIC_IODIDE
  name = G4_MERCURIC_IODIDE
  specific = 4
FEATURE [App::DocumentObjectGroupPython] C_element059  label="C_element : 032"  # scripted group (container) (typed FeaturePython)
  n = 1
  ref = C_element
FEATURE [App::DocumentObjectGroupPython] H_element053  label="H_element : 028"  # scripted group (container) (typed FeaturePython)
  n = 4
  ref = H_element
FEATURE [App::DocumentObjectGroupPython] G4_METHANE  # scripted group (container) (typed FeaturePython)
  Dunit = g/cm3
  Dvalue = 0.000667151
  Group = -> [C_element059,H_element053]
  conduct = 2
  density = 1
  expand = 3
  formula = G4_METHANE
  name = G4_METHANE
  specific = 4
FEATURE [App::DocumentObjectGroupPython] C_element060  label="C_element : 033"  # scripted group (container) (typed FeaturePython)
  n = 1
  ref = C_element
FEATURE [App::DocumentObjectGroupPython] H_element054  label="H_element : 029"  # scripted group (container) (typed FeaturePython)
  n = 4
  ref = H_element
FEATURE [App::DocumentObjectGroupPython] O_element062  label="O_element : 033"  # scripted group (container) (typed FeaturePython)
  n = 1
  ref = O_element
FEATURE [App::DocumentObjectGroupPython] G4_METHANOL  # scripted group (container) (typed FeaturePython)
  Dunit = g/cm3
  Dvalue = 0.7914
  Group = -> [C_element060,H_element054,O_element062]
  conduct = 2
  density = 1
  expand = 3
  formula = G4_METHANOL
  name = G4_METHANOL
  specific = 4
FEATURE [App::DocumentObjectGroupPython] H_element055  label="H_element : 0.134"  # scripted group (container) (typed FeaturePython)
  n = 0.13404
FEATURE [App::DocumentObjectGroupPython] C_element061  label="C_element : 0.778"  # scripted group (container) (typed FeaturePython)
  n = 0.77796
FEATURE [App::DocumentObjectGroupPython] O_element063  label="O_element : 0.035"  # scripted group (container) (typed FeaturePython)
  n = 0.03502
FEATURE [App::DocumentObjectGroupPython] Mg_element009  label="Mg_element : 0.039"  # scripted group (container) (typed FeaturePython)
  n = 0.038594
FEATURE [App::DocumentObjectGroupPython] Ti_element002  label="Ti_element : 0.014"  # scripted group (container) (typed FeaturePython)
  n = 0.014386
FEATURE [App::DocumentObjectGroupPython] G4_MIX_D_WAX  # scripted group (container) (typed FeaturePython)
  Dunit = g/cm3
  Dvalue = 0.99
  Group = -> [H_element055,C_element061,O_element063,Mg_element009,Ti_element002]
  conduct = 2
  density = 1
  expand = 3
  formula = G4_MIX_D_WAX
  name = G4_MIX_D_WAX
  specific = 4
FEATURE [App::DocumentObjectGroupPython] H_element056  label="H_element : 0.135"  # scripted group (container) (typed FeaturePython)
  n = 0.081192
FEATURE [App::DocumentObjectGroupPython] C_element062  label="C_element : 0.583"  # scripted group (container) (typed FeaturePython)
  n = 0.583442
FEATURE [App::DocumentObjectGroupPython] N_element024  label="N_element : 0.018"  # scripted group (container) (typed FeaturePython)
  n = 0.017798
FEATURE [App::DocumentObjectGroupPython] O_element064  label="O_element : 0.186"  # scripted group (container) (typed FeaturePython)
  n = 0.186381
FEATURE [App::DocumentObjectGroupPython] Mg_element010  label="Mg_element : 0.130"  # scripted group (container) (typed FeaturePython)
  n = 0.130287
FEATURE [App::DocumentObjectGroupPython] Cl_element015  label="Cl_element : 0.588"  # scripted group (container) (typed FeaturePython)
  n = 0.0009
FEATURE [App::DocumentObjectGroupPython] G4_MS20_TISSUE  # scripted group (container) (typed FeaturePython)
  Dunit = g/cm3
  Dvalue = 1
  Group = -> [H_element056,C_element062,N_element024,O_element064,Mg_element010,Cl_element015]
  conduct = 2
  density = 1
  expand = 3
  formula = G4_MS20_TISSUE
  name = G4_MS20_TISSUE
  specific = 4
FEATURE [App::DocumentObjectGroupPython] H_element057  label="H_element : 0.136"  # scripted group (container) (typed FeaturePython)
  n = 0.102
FEATURE [App::DocumentObjectGroupPython] C_element063  label="C_element : 0.143"  # scripted group (container) (typed FeaturePython)
  n = 0.143
FEATURE [App::DocumentObjectGroupPython] N_element025  label="N_element : 0.034"  # scripted group (container) (typed FeaturePython)
  n = 0.034
FEATURE [App::DocumentObjectGroupPython] O_element065  label="O_element : 0.710"  # scripted group (container) (typed FeaturePython)
  n = 0.71
FEATURE [App::DocumentObjectGroupPython] Na_element011  label="Na_element : 0.098"  # scripted group (container) (typed FeaturePython)
  n = 0.001
FEATURE [App::DocumentObjectGroupPython] P_element007  label="P_element : 0.002"  # scripted group (container) (typed FeaturePython)
  n = 0.002
FEATURE [App::DocumentObjectGroupPython] S_element017  label="S_element : 0.018"  # scripted group (container) (typed FeaturePython)
  n = 0.003
FEATURE [App::DocumentObjectGroupPython] Cl_element016  label="Cl_element : 0.589"  # scripted group (container) (typed FeaturePython)
  n = 0.001
FEATURE [App::DocumentObjectGroupPython] K_element006  label="K_element : 0.004"  # scripted group (container) (typed FeaturePython)
  n = 0.004
FEATURE [App::DocumentObjectGroupPython] G4_MUSCLE_SKELETAL_ICRP  # scripted group (container) (typed FeaturePython)
  Dunit = g/cm3
  Dvalue = 1.05
  Group = -> [H_element057,C_element063,N_element025,O_element065,Na_element011,P_element007,S_element017,Cl_element016,K_element006]
  conduct = 2
  density = 1
  expand = 3
  formula = G4_MUSCLE_SKELETAL_ICRP
  name = G4_MUSCLE_SKELETAL_ICRP
  specific = 4
FEATURE [App::DocumentObjectGroupPython] H_element058  label="H_element : 0.137"  # scripted group (container) (typed FeaturePython)
  n = 0.102102
FEATURE [App::DocumentObjectGroupPython] C_element064  label="C_element : 0.123"  # scripted group (container) (typed FeaturePython)
  n = 0.123123
FEATURE [App::DocumentObjectGroupPython] N_element026  label="N_element : 0.756"  # scripted group (container) (typed FeaturePython)
  n = 0.035035
FEATURE [App::DocumentObjectGroupPython] O_element066  label="O_element : 0.730"  # scripted group (container) (typed FeaturePython)
  n = 0.72973
FEATURE [App::DocumentObjectGroupPython] Na_element012  label="Na_element : 0.099"  # scripted group (container) (typed FeaturePython)
  n = 0.001001
FEATURE [App::DocumentObjectGroupPython] P_element008  label="P_element : 0.106"  # scripted group (container) (typed FeaturePython)
  n = 0.002002
FEATURE [App::DocumentObjectGroupPython] S_element018  label="S_element : 0.019"  # scripted group (container) (typed FeaturePython)
  n = 0.004004
FEATURE [App::DocumentObjectGroupPython] K_element007  label="K_element : 0.016"  # scripted group (container) (typed FeaturePython)
  n = 0.003003
FEATURE [App::DocumentObjectGroupPython] G4_MUSCLE_STRIATED_ICRU  # scripted group (container) (typed FeaturePython)
  Dunit = g/cm3
  Dvalue = 1.04
  Group = -> [H_element058,C_element064,N_element026,O_element066,Na_element012,P_element008,S_element018,K_element007]
  conduct = 2
  density = 1
  expand = 3
  formula = G4_MUSCLE_STRIATED_ICRU
  name = G4_MUSCLE_STRIATED_ICRU
  specific = 4
FEATURE [App::DocumentObjectGroupPython] H_element059  label="H_element : 0.098"  # scripted group (container) (typed FeaturePython)
  n = 0.0982341
FEATURE [App::DocumentObjectGroupPython] C_element065  label="C_element : 0.156"  # scripted group (container) (typed FeaturePython)
  n = 0.156214
FEATURE [App::DocumentObjectGroupPython] N_element027  label="N_element : 0.757"  # scripted group (container) (typed FeaturePython)
  n = 0.035451
FEATURE [App::DocumentObjectGroupPython] O_element067  label="O_element : 0.880"  # scripted group (container) (typed FeaturePython)
  n = 0.710101
FEATURE [App::DocumentObjectGroupPython] G4_MUSCLE_WITH_SUCROSE  # scripted group (container) (typed FeaturePython)
  Dunit = g/cm3
  Dvalue = 1.11
  Group = -> [H_element059,C_element065,N_element027,O_element067]
  conduct = 2
  density = 1
  expand = 3
  formula = G4_MUSCLE_WITH_SUCROSE
  name = G4_MUSCLE_WITH_SUCROSE
  specific = 4
FEATURE [App::DocumentObjectGroupPython] H_element060  label="H_element : 0.138"  # scripted group (container) (typed FeaturePython)
  n = 0.101969
FEATURE [App::DocumentObjectGroupPython] C_element066  label="C_element : 0.120"  # scripted group (container) (typed FeaturePython)
  n = 0.120058
FEATURE [App::DocumentObjectGroupPython] N_element028  label="N_element : 0.758"  # scripted group (container) (typed FeaturePython)
  n = 0.035451
FEATURE [App::DocumentObjectGroupPython] O_element068  label="O_element : 0.743"  # scripted group (container) (typed FeaturePython)
  n = 0.742522
FEATURE [App::DocumentObjectGroupPython] G4_MUSCLE_WITHOUT_SUCROSE  # scripted group (container) (typed FeaturePython)
  Dunit = g/cm3
  Dvalue = 1.07
  Group = -> [H_element060,C_element066,N_element028,O_element068]
  conduct = 2
  density = 1
  expand = 3
  formula = G4_MUSCLE_WITHOUT_SUCROSE
  name = G4_MUSCLE_WITHOUT_SUCROSE
  specific = 4
FEATURE [App::DocumentObjectGroupPython] C_element067  label="C_element : 10"  # scripted group (container) (typed FeaturePython)
  n = 10
  ref = C_element
FEATURE [App::DocumentObjectGroupPython] H_element061  label="H_element : 030"  # scripted group (container) (typed FeaturePython)
  n = 8
  ref = H_element
FEATURE [App::DocumentObjectGroupPython] G4_NAPHTHALENE  # scripted group (container) (typed FeaturePython)
  Dunit = g/cm3
  Dvalue = 1.145
  Group = -> [C_element067,H_element061]
  conduct = 2
  density = 1
  expand = 3
  formula = G4_NAPHTHALENE
  name = G4_NAPHTHALENE
  specific = 4
FEATURE [App::DocumentObjectGroupPython] C_element068  label="C_element : 034"  # scripted group (container) (typed FeaturePython)
  n = 6
  ref = C_element
FEATURE [App::DocumentObjectGroupPython] H_element062  label="H_element : 031"  # scripted group (container) (typed FeaturePython)
  n = 5
  ref = H_element
FEATURE [App::DocumentObjectGroupPython] N_element029  label="N_element : 012"  # scripted group (container) (typed FeaturePython)
  n = 1
  ref = N_element
FEATURE [App::DocumentObjectGroupPython] O_element069  label="O_element : 034"  # scripted group (container) (typed FeaturePython)
  n = 2
  ref = O_element
FEATURE [App::DocumentObjectGroupPython] G4_NITROBENZENE  # scripted group (container) (typed FeaturePython)
  Dunit = g/cm3
  Dvalue = 1.19867
  Group = -> [C_element068,H_element062,N_element029,O_element069]
  conduct = 2
  density = 1
  expand = 3
  formula = G4_NITROBENZENE
  name = G4_NITROBENZENE
  specific = 4
FEATURE [App::DocumentObjectGroupPython] N_element030  label="N_element : 013"  # scripted group (container) (typed FeaturePython)
  n = 2
  ref = N_element
FEATURE [App::DocumentObjectGroupPython] O_element070  label="O_element : 035"  # scripted group (container) (typed FeaturePython)
  n = 1
  ref = O_element
FEATURE [App::DocumentObjectGroupPython] G4_NITROUS_OXIDE  # scripted group (container) (typed FeaturePython)
  Dunit = g/cm3
  Dvalue = 0.00183094
  Group = -> [N_element030,O_element070]
  conduct = 2
  density = 1
  expand = 3
  formula = G4_NITROUS_OXIDE
  name = G4_NITROUS_OXIDE
  specific = 4
FEATURE [App::DocumentObjectGroupPython] H_element063  label="H_element : 0.104"  # scripted group (container) (typed FeaturePython)
  n = 0.103509
FEATURE [App::DocumentObjectGroupPython] C_element069  label="C_element : 0.648"  # scripted group (container) (typed FeaturePython)
  n = 0.648416
FEATURE [App::DocumentObjectGroupPython] N_element031  label="N_element : 0.100"  # scripted group (container) (typed FeaturePython)
  n = 0.0995361
FEATURE [App::DocumentObjectGroupPython] O_element071  label="O_element : 0.149"  # scripted group (container) (typed FeaturePython)
  n = 0.148539
FEATURE [App::DocumentObjectGroupPython] G4_NYLON_8062  label="G4_NYLON-8062"  # scripted group (container) (typed FeaturePython)
  Dunit = g/cm3
  Dvalue = 1.08
  Group = -> [H_element063,C_element069,N_element031,O_element071]
  conduct = 2
  density = 1
  expand = 3
  formula = G4_NYLON-8062
  name = G4_NYLON-8062
  specific = 4
FEATURE [App::DocumentObjectGroupPython] C_element070  label="C_element : 035"  # scripted group (container) (typed FeaturePython)
  n = 6
  ref = C_element
FEATURE [App::DocumentObjectGroupPython] H_element064  label="H_element : 11"  # scripted group (container) (typed FeaturePython)
  n = 11
  ref = H_element
FEATURE [App::DocumentObjectGroupPython] N_element032  label="N_element : 014"  # scripted group (container) (typed FeaturePython)
  n = 1
  ref = N_element
FEATURE [App::DocumentObjectGroupPython] O_element072  label="O_element : 036"  # scripted group (container) (typed FeaturePython)
  n = 1
  ref = O_element
FEATURE [App::DocumentObjectGroupPython] G4_NYLON_6_6  label="G4_NYLON-6-6"  # scripted group (container) (typed FeaturePython)
  Dunit = g/cm3
  Dvalue = 1.14
  Group = -> [C_element070,H_element064,N_element032,O_element072]
  conduct = 2
  density = 1
  expand = 3
  formula = G4_NYLON-6-6
  name = G4_NYLON-6-6
  specific = 4
FEATURE [App::DocumentObjectGroupPython] H_element065  label="H_element : 0.139"  # scripted group (container) (typed FeaturePython)
  n = 0.107062
FEATURE [App::DocumentObjectGroupPython] C_element071  label="C_element : 0.680"  # scripted group (container) (typed FeaturePython)
  n = 0.680449
FEATURE [App::DocumentObjectGroupPython] N_element033  label="N_element : 0.099"  # scripted group (container) (typed FeaturePython)
  n = 0.099189
FEATURE [App::DocumentObjectGroupPython] O_element073  label="O_element : 0.113"  # scripted group (container) (typed FeaturePython)
  n = 0.1133
FEATURE [App::DocumentObjectGroupPython] G4_NYLON_6_10  label="G4_NYLON-6-10"  # scripted group (container) (typed FeaturePython)
  Dunit = g/cm3
  Dvalue = 1.14
  Group = -> [H_element065,C_element071,N_element033,O_element073]
  conduct = 2
  density = 1
  expand = 3
  formula = G4_NYLON-6-10
  name = G4_NYLON-6-10
  specific = 4
FEATURE [App::DocumentObjectGroupPython] H_element066  label="H_element : 0.140"  # scripted group (container) (typed FeaturePython)
  n = 0.115476
FEATURE [App::DocumentObjectGroupPython] C_element072  label="C_element : 0.721"  # scripted group (container) (typed FeaturePython)
  n = 0.720818
FEATURE [App::DocumentObjectGroupPython] N_element034  label="N_element : 0.076"  # scripted group (container) (typed FeaturePython)
  n = 0.0764169
FEATURE [App::DocumentObjectGroupPython] O_element074  label="O_element : 0.087"  # scripted group (container) (typed FeaturePython)
  n = 0.0872889
FEATURE [App::DocumentObjectGroupPython] G4_NYLON_11_RILSAN  label="G4_NYLON-11_RILSAN"  # scripted group (container) (typed FeaturePython)
  Dunit = g/cm3
  Dvalue = 1.425
  Group = -> [H_element066,C_element072,N_element034,O_element074]
  conduct = 2
  density = 1
  expand = 3
  formula = G4_NYLON-11_RILSAN
  name = G4_NYLON-11_RILSAN
  specific = 4
FEATURE [App::DocumentObjectGroupPython] C_element073  label="C_element : 8"  # scripted group (container) (typed FeaturePython)
  n = 8
  ref = C_element
FEATURE [App::DocumentObjectGroupPython] H_element067  label="H_element : 18"  # scripted group (container) (typed FeaturePython)
  n = 18
  ref = H_element
FEATURE [App::DocumentObjectGroupPython] G4_OCTANE  # scripted group (container) (typed FeaturePython)
  Dunit = g/cm3
  Dvalue = 0.7026
  Group = -> [C_element073,H_element067]
  conduct = 2
  density = 1
  expand = 3
  formula = G4_OCTANE
  name = G4_OCTANE
  specific = 4
FEATURE [App::DocumentObjectGroupPython] C_element074  label="C_element : 25"  # scripted group (container) (typed FeaturePython)
  n = 25
  ref = C_element
FEATURE [App::DocumentObjectGroupPython] H_element068  label="H_element : 52"  # scripted group (container) (typed FeaturePython)
  n = 52
  ref = H_element
FEATURE [App::DocumentObjectGroupPython] G4_PARAFFIN  # scripted group (container) (typed FeaturePython)
  Dunit = g/cm3
  Dvalue = 0.93
  Group = -> [C_element074,H_element068]
  conduct = 2
  density = 1
  expand = 3
  formula = G4_PARAFFIN
  name = G4_PARAFFIN
  specific = 4
FEATURE [App::DocumentObjectGroupPython] C_element075  label="C_element : 036"  # scripted group (container) (typed FeaturePython)
  n = 5
  ref = C_element
FEATURE [App::DocumentObjectGroupPython] H_element069  label="H_element : 032"  # scripted group (container) (typed FeaturePython)
  n = 12
  ref = H_element
FEATURE [App::DocumentObjectGroupPython] G4_N_PENTANE  label="G4_N-PENTANE"  # scripted group (container) (typed FeaturePython)
  Dunit = g/cm3
  Dvalue = 0.6262
  Group = -> [C_element075,H_element069]
  conduct = 2
  density = 1
  expand = 3
  formula = G4_N-PENTANE
  name = G4_N-PENTANE
  specific = 4
FEATURE [App::DocumentObjectGroupPython] H_element070  label="H_element : 0.014"  # scripted group (container) (typed FeaturePython)
  n = 0.0141
FEATURE [App::DocumentObjectGroupPython] C_element076  label="C_element : 0.072"  # scripted group (container) (typed FeaturePython)
  n = 0.072261
FEATURE [App::DocumentObjectGroupPython] N_element035  label="N_element : 0.019"  # scripted group (container) (typed FeaturePython)
  n = 0.01932
FEATURE [App::DocumentObjectGroupPython] O_element075  label="O_element : 0.066"  # scripted group (container) (typed FeaturePython)
  n = 0.066101
FEATURE [App::DocumentObjectGroupPython] S_element019  label="S_element : 0.020"  # scripted group (container) (typed FeaturePython)
  n = 0.00189
FEATURE [App::DocumentObjectGroupPython] Br_element004  label="Br_element : 0.349"  # scripted group (container) (typed FeaturePython)
  n = 0.349103
FEATURE [App::DocumentObjectGroupPython] Ag_element001  label="Ag_element : 0.474"  # scripted group (container) (typed FeaturePython)
  n = 0.474105
FEATURE [App::DocumentObjectGroupPython] I_element005  label="I_element : 0.003"  # scripted group (container) (typed FeaturePython)
  n = 0.00312
FEATURE [App::DocumentObjectGroupPython] G4_PHOTO_EMULSION  # scripted group (container) (typed FeaturePython)
  Dunit = g/cm3
  Dvalue = 3.815
  Group = -> [H_element070,C_element076,N_element035,O_element075,S_element019,Br_element004,Ag_element001,I_element005]
  conduct = 2
  density = 1
  expand = 3
  formula = G4_PHOTO_EMULSION
  name = G4_PHOTO_EMULSION
  specific = 4
FEATURE [App::DocumentObjectGroupPython] C_element077  label="C_element : 9"  # scripted group (container) (typed FeaturePython)
  n = 9
  ref = C_element
FEATURE [App::DocumentObjectGroupPython] H_element071  label="H_element : 033"  # scripted group (container) (typed FeaturePython)
  n = 10
  ref = H_element
FEATURE [App::DocumentObjectGroupPython] G4_PLASTIC_SC_VINYLTOLUENE  # scripted group (container) (typed FeaturePython)
  Dunit = g/cm3
  Dvalue = 1.032
  Group = -> [C_element077,H_element071]
  conduct = 2
  density = 1
  expand = 3
  formula = G4_PLASTIC_SC_VINYLTOLUENE
  name = G4_PLASTIC_SC_VINYLTOLUENE
  specific = 4
FEATURE [App::DocumentObjectGroupPython] Pu_element001  label="Pu_element : 1"  # scripted group (container) (typed FeaturePython)
  n = 1
  ref = Pu_element
FEATURE [App::DocumentObjectGroupPython] O_element076  label="O_element : 037"  # scripted group (container) (typed FeaturePython)
  n = 2
  ref = O_element
FEATURE [App::DocumentObjectGroupPython] G4_PLUTONIUM_DIOXIDE  # scripted group (container) (typed FeaturePython)
  Dunit = g/cm3
  Dvalue = 11.46
  Group = -> [Pu_element001,O_element076]
  conduct = 2
  density = 1
  expand = 3
  formula = G4_PLUTONIUM_DIOXIDE
  name = G4_PLUTONIUM_DIOXIDE
  specific = 4
FEATURE [App::DocumentObjectGroupPython] C_element078  label="C_element : 037"  # scripted group (container) (typed FeaturePython)
  n = 3
  ref = C_element
FEATURE [App::DocumentObjectGroupPython] H_element072  label="H_element : 034"  # scripted group (container) (typed FeaturePython)
  n = 3
  ref = H_element
FEATURE [App::DocumentObjectGroupPython] N_element036  label="N_element : 015"  # scripted group (container) (typed FeaturePython)
  n = 1
  ref = N_element
FEATURE [App::DocumentObjectGroupPython] G4_POLYACRYLONITRILE  # scripted group (container) (typed FeaturePython)
  Dunit = g/cm3
  Dvalue = 1.17
  Group = -> [C_element078,H_element072,N_element036]
  conduct = 2
  density = 1
  expand = 3
  formula = G4_POLYACRYLONITRILE
  name = G4_POLYACRYLONITRILE
  specific = 4
FEATURE [App::DocumentObjectGroupPython] C_element079  label="C_element : 16"  # scripted group (container) (typed FeaturePython)
  n = 16
  ref = C_element
FEATURE [App::DocumentObjectGroupPython] H_element073  label="H_element : 035"  # scripted group (container) (typed FeaturePython)
  n = 14
  ref = H_element
FEATURE [App::DocumentObjectGroupPython] O_element077  label="O_element : 038"  # scripted group (container) (typed FeaturePython)
  n = 3
  ref = O_element
FEATURE [App::DocumentObjectGroupPython] G4_POLYCARBONATE  # scripted group (container) (typed FeaturePython)
  Dunit = g/cm3
  Dvalue = 1.2
  Group = -> [C_element079,H_element073,O_element077]
  conduct = 2
  density = 1
  expand = 3
  formula = G4_POLYCARBONATE
  name = G4_POLYCARBONATE
  specific = 4
FEATURE [App::DocumentObjectGroupPython] C_element080  label="C_element : 038"  # scripted group (container) (typed FeaturePython)
  n = 8
  ref = C_element
FEATURE [App::DocumentObjectGroupPython] H_element074  label="H_element : 036"  # scripted group (container) (typed FeaturePython)
  n = 7
  ref = H_element
FEATURE [App::DocumentObjectGroupPython] Cl_element017  label="Cl_element : 007"  # scripted group (container) (typed FeaturePython)
  n = 1
  ref = Cl_element
FEATURE [App::DocumentObjectGroupPython] G4_POLYCHLOROSTYRENE  # scripted group (container) (typed FeaturePython)
  Dunit = g/cm3
  Dvalue = 1.3
  Group = -> [C_element080,H_element074,Cl_element017]
  conduct = 2
  density = 1
  expand = 3
  formula = G4_POLYCHLOROSTYRENE
  name = G4_POLYCHLOROSTYRENE
  specific = 4
FEATURE [App::DocumentObjectGroupPython] C_element081  label="C_element : 039"  # scripted group (container) (typed FeaturePython)
  n = 1
  ref = C_element
FEATURE [App::DocumentObjectGroupPython] H_element075  label="H_element : 037"  # scripted group (container) (typed FeaturePython)
  n = 2
  ref = H_element
FEATURE [App::DocumentObjectGroupPython] G4_POLYETHYLENE  # scripted group (container) (typed FeaturePython)
  Dunit = g/cm3
  Dvalue = 0.94
  Group = -> [C_element081,H_element075]
  conduct = 2
  density = 1
  expand = 3
  formula = G4_POLYETHYLENE
  name = G4_POLYETHYLENE
  specific = 4
FEATURE [App::DocumentObjectGroupPython] C_element082  label="C_element : 040"  # scripted group (container) (typed FeaturePython)
  n = 10
  ref = C_element
FEATURE [App::DocumentObjectGroupPython] H_element076  label="H_element : 038"  # scripted group (container) (typed FeaturePython)
  n = 8
  ref = H_element
FEATURE [App::DocumentObjectGroupPython] O_element078  label="O_element : 039"  # scripted group (container) (typed FeaturePython)
  n = 4
  ref = O_element
FEATURE [App::DocumentObjectGroupPython] G4_MYLAR  # scripted group (container) (typed FeaturePython)
  Dunit = g/cm3
  Dvalue = 1.4
  Group = -> [C_element082,H_element076,O_element078]
  conduct = 2
  density = 1
  expand = 3
  formula = G4_MYLAR
  name = G4_MYLAR
  specific = 4
FEATURE [App::DocumentObjectGroupPython] C_element083  label="C_element : 041"  # scripted group (container) (typed FeaturePython)
  n = 5
  ref = C_element
FEATURE [App::DocumentObjectGroupPython] H_element077  label="H_element : 039"  # scripted group (container) (typed FeaturePython)
  n = 8
  ref = H_element
FEATURE [App::DocumentObjectGroupPython] O_element079  label="O_element : 040"  # scripted group (container) (typed FeaturePython)
  n = 2
  ref = O_element
FEATURE [App::DocumentObjectGroupPython] G4_PLEXIGLASS  # scripted group (container) (typed FeaturePython)
  Dunit = g/cm3
  Dvalue = 1.19
  Group = -> [C_element083,H_element077,O_element079]
  conduct = 2
  density = 1
  expand = 3
  formula = G4_PLEXIGLASS
  name = G4_PLEXIGLASS
  specific = 4
FEATURE [App::DocumentObjectGroupPython] C_element084  label="C_element : 042"  # scripted group (container) (typed FeaturePython)
  n = 1
  ref = C_element
FEATURE [App::DocumentObjectGroupPython] H_element078  label="H_element : 040"  # scripted group (container) (typed FeaturePython)
  n = 2
  ref = H_element
FEATURE [App::DocumentObjectGroupPython] O_element080  label="O_element : 041"  # scripted group (container) (typed FeaturePython)
  n = 1
  ref = O_element
FEATURE [App::DocumentObjectGroupPython] G4_POLYOXYMETHYLENE  # scripted group (container) (typed FeaturePython)
  Dunit = g/cm3
  Dvalue = 1.425
  Group = -> [C_element084,H_element078,O_element080]
  conduct = 2
  density = 1
  expand = 3
  formula = G4_POLYOXYMETHYLENE
  name = G4_POLYOXYMETHYLENE
  specific = 4
FEATURE [App::DocumentObjectGroupPython] C_element085  label="C_element : 043"  # scripted group (container) (typed FeaturePython)
  n = 2
  ref = C_element
FEATURE [App::DocumentObjectGroupPython] H_element079  label="H_element : 041"  # scripted group (container) (typed FeaturePython)
  n = 4
  ref = H_element
FEATURE [App::DocumentObjectGroupPython] G4_POLYPROPYLENE  # scripted group (container) (typed FeaturePython)
  Dunit = g/cm3
  Dvalue = 0.9
  Group = -> [C_element085,H_element079]
  conduct = 2
  density = 1
  expand = 3
  formula = G4_POLYPROPYLENE
  name = G4_POLYPROPYLENE
  specific = 4
FEATURE [App::DocumentObjectGroupPython] C_element086  label="C_element : 044"  # scripted group (container) (typed FeaturePython)
  n = 8
  ref = C_element
FEATURE [App::DocumentObjectGroupPython] H_element080  label="H_element : 042"  # scripted group (container) (typed FeaturePython)
  n = 8
  ref = H_element
FEATURE [App::DocumentObjectGroupPython] G4_POLYSTYRENE  # scripted group (container) (typed FeaturePython)
  Dunit = g/cm3
  Dvalue = 1.06
  Group = -> [C_element086,H_element080]
  conduct = 2
  density = 1
  expand = 3
  formula = G4_POLYSTYRENE
  name = G4_POLYSTYRENE
  specific = 4
FEATURE [App::DocumentObjectGroupPython] C_element087  label="C_element : 045"  # scripted group (container) (typed FeaturePython)
  n = 2
  ref = C_element
FEATURE [App::DocumentObjectGroupPython] F_element014  label="F_element : 4"  # scripted group (container) (typed FeaturePython)
  n = 4
  ref = F_element
FEATURE [App::DocumentObjectGroupPython] G4_TEFLON  # scripted group (container) (typed FeaturePython)
  Dunit = g/cm3
  Dvalue = 2.2
  Group = -> [C_element087,F_element014]
  conduct = 2
  density = 1
  expand = 3
  formula = G4_TEFLON
  name = G4_TEFLON
  specific = 4
FEATURE [App::DocumentObjectGroupPython] C_element088  label="C_element : 046"  # scripted group (container) (typed FeaturePython)
  n = 2
  ref = C_element
FEATURE [App::DocumentObjectGroupPython] F_element015  label="F_element : 006"  # scripted group (container) (typed FeaturePython)
  n = 3
  ref = F_element
FEATURE [App::DocumentObjectGroupPython] Cl_element018  label="Cl_element : 008"  # scripted group (container) (typed FeaturePython)
  n = 1
  ref = Cl_element
FEATURE [App::DocumentObjectGroupPython] G4_POLYTRIFLUOROCHLOROETHYLENE  # scripted group (container) (typed FeaturePython)
  Dunit = g/cm3
  Dvalue = 2.1
  Group = -> [C_element088,F_element015,Cl_element018]
  conduct = 2
  density = 1
  expand = 3
  formula = G4_POLYTRIFLUOROCHLOROETHYLENE
  name = G4_POLYTRIFLUOROCHLOROETHYLENE
  specific = 4
FEATURE [App::DocumentObjectGroupPython] C_element089  label="C_element : 047"  # scripted group (container) (typed FeaturePython)
  n = 4
  ref = C_element
FEATURE [App::DocumentObjectGroupPython] H_element081  label="H_element : 043"  # scripted group (container) (typed FeaturePython)
  n = 6
  ref = H_element
FEATURE [App::DocumentObjectGroupPython] O_element081  label="O_element : 042"  # scripted group (container) (typed FeaturePython)
  n = 2
  ref = O_element
FEATURE [App::DocumentObjectGroupPython] G4_POLYVINYL_ACETATE  # scripted group (container) (typed FeaturePython)
  Dunit = g/cm3
  Dvalue = 1.19
  Group = -> [C_element089,H_element081,O_element081]
  conduct = 2
  density = 1
  expand = 3
  formula = G4_POLYVINYL_ACETATE
  name = G4_POLYVINYL_ACETATE
  specific = 4
FEATURE [App::DocumentObjectGroupPython] C_element090  label="C_element : 048"  # scripted group (container) (typed FeaturePython)
  n = 2
  ref = C_element
FEATURE [App::DocumentObjectGroupPython] H_element082  label="H_element : 044"  # scripted group (container) (typed FeaturePython)
  n = 4
  ref = H_element
FEATURE [App::DocumentObjectGroupPython] O_element082  label="O_element : 043"  # scripted group (container) (typed FeaturePython)
  n = 1
  ref = O_element
FEATURE [App::DocumentObjectGroupPython] G4_POLYVINYL_ALCOHOL  # scripted group (container) (typed FeaturePython)
  Dunit = g/cm3
  Dvalue = 1.3
  Group = -> [C_element090,H_element082,O_element082]
  conduct = 2
  density = 1
  expand = 3
  formula = G4_POLYVINYL_ALCOHOL
  name = G4_POLYVINYL_ALCOHOL
  specific = 4
FEATURE [App::DocumentObjectGroupPython] C_element091  label="C_element : 049"  # scripted group (container) (typed FeaturePython)
  n = 8
  ref = C_element
FEATURE [App::DocumentObjectGroupPython] H_element083  label="H_element : 045"  # scripted group (container) (typed FeaturePython)
  n = 14
  ref = H_element
FEATURE [App::DocumentObjectGroupPython] O_element083  label="O_element : 044"  # scripted group (container) (typed FeaturePython)
  n = 2
  ref = O_element
FEATURE [App::DocumentObjectGroupPython] G4_POLYVINYL_BUTYRAL  # scripted group (container) (typed FeaturePython)
  Dunit = g/cm3
  Dvalue = 1.12
  Group = -> [C_element091,H_element083,O_element083]
  conduct = 2
  density = 1
  expand = 3
  formula = G4_POLYVINYL_BUTYRAL
  name = G4_POLYVINYL_BUTYRAL
  specific = 4
FEATURE [App::DocumentObjectGroupPython] C_element092  label="C_element : 050"  # scripted group (container) (typed FeaturePython)
  n = 2
  ref = C_element
FEATURE [App::DocumentObjectGroupPython] H_element084  label="H_element : 046"  # scripted group (container) (typed FeaturePython)
  n = 3
  ref = H_element
FEATURE [App::DocumentObjectGroupPython] Cl_element019  label="Cl_element : 009"  # scripted group (container) (typed FeaturePython)
  n = 1
  ref = Cl_element
FEATURE [App::DocumentObjectGroupPython] G4_POLYVINYL_CHLORIDE  # scripted group (container) (typed FeaturePython)
  Dunit = g/cm3
  Dvalue = 1.3
  Group = -> [C_element092,H_element084,Cl_element019]
  conduct = 2
  density = 1
  expand = 3
  formula = G4_POLYVINYL_CHLORIDE
  name = G4_POLYVINYL_CHLORIDE
  specific = 4
FEATURE [App::DocumentObjectGroupPython] C_element093  label="C_element : 051"  # scripted group (container) (typed FeaturePython)
  n = 2
  ref = C_element
FEATURE [App::DocumentObjectGroupPython] H_element085  label="H_element : 047"  # scripted group (container) (typed FeaturePython)
  n = 2
  ref = H_element
FEATURE [App::DocumentObjectGroupPython] Cl_element020  label="Cl_element : 010"  # scripted group (container) (typed FeaturePython)
  n = 2
  ref = Cl_element
FEATURE [App::DocumentObjectGroupPython] G4_POLYVINYLIDENE_CHLORIDE  # scripted group (container) (typed FeaturePython)
  Dunit = g/cm3
  Dvalue = 1.7
  Group = -> [C_element093,H_element085,Cl_element020]
  conduct = 2
  density = 1
  expand = 3
  formula = G4_POLYVINYLIDENE_CHLORIDE
  name = G4_POLYVINYLIDENE_CHLORIDE
  specific = 4
FEATURE [App::DocumentObjectGroupPython] C_element094  label="C_element : 052"  # scripted group (container) (typed FeaturePython)
  n = 2
  ref = C_element
FEATURE [App::DocumentObjectGroupPython] H_element086  label="H_element : 048"  # scripted group (container) (typed FeaturePython)
  n = 2
  ref = H_element
FEATURE [App::DocumentObjectGroupPython] F_element016  label="F_element : 007"  # scripted group (container) (typed FeaturePython)
  n = 2
  ref = F_element
FEATURE [App::DocumentObjectGroupPython] G4_POLYVINYLIDENE_FLUORIDE  # scripted group (container) (typed FeaturePython)
  Dunit = g/cm3
  Dvalue = 1.76
  Group = -> [C_element094,H_element086,F_element016]
  conduct = 2
  density = 1
  expand = 3
  formula = G4_POLYVINYLIDENE_FLUORIDE
  name = G4_POLYVINYLIDENE_FLUORIDE
  specific = 4
FEATURE [App::DocumentObjectGroupPython] C_element095  label="C_element : 053"  # scripted group (container) (typed FeaturePython)
  n = 6
  ref = C_element
FEATURE [App::DocumentObjectGroupPython] H_element087  label="H_element : 9"  # scripted group (container) (typed FeaturePython)
  n = 9
  ref = H_element
FEATURE [App::DocumentObjectGroupPython] N_element037  label="N_element : 016"  # scripted group (container) (typed FeaturePython)
  n = 1
  ref = N_element
FEATURE [App::DocumentObjectGroupPython] O_element084  label="O_element : 045"  # scripted group (container) (typed FeaturePython)
  n = 1
  ref = O_element
FEATURE [App::DocumentObjectGroupPython] G4_POLYVINYL_PYRROLIDONE  # scripted group (container) (typed FeaturePython)
  Dunit = g/cm3
  Dvalue = 1.25
  Group = -> [C_element095,H_element087,N_element037,O_element084]
  conduct = 2
  density = 1
  expand = 3
  formula = G4_POLYVINYL_PYRROLIDONE
  name = G4_POLYVINYL_PYRROLIDONE
  specific = 4
FEATURE [App::DocumentObjectGroupPython] K_element008  label="K_element : 1"  # scripted group (container) (typed FeaturePython)
  n = 1
  ref = K_element
FEATURE [App::DocumentObjectGroupPython] I_element006  label="I_element : 003"  # scripted group (container) (typed FeaturePython)
  n = 1
  ref = I_element
FEATURE [App::DocumentObjectGroupPython] G4_POTASSIUM_IODIDE  # scripted group (container) (typed FeaturePython)
  Dunit = g/cm3
  Dvalue = 3.13
  Group = -> [K_element008,I_element006]
  conduct = 2
  density = 1
  expand = 3
  formula = G4_POTASSIUM_IODIDE
  name = G4_POTASSIUM_IODIDE
  specific = 4
FEATURE [App::DocumentObjectGroupPython] K_element009  label="K_element : 2"  # scripted group (container) (typed FeaturePython)
  n = 2
  ref = K_element
FEATURE [App::DocumentObjectGroupPython] O_element085  label="O_element : 046"  # scripted group (container) (typed FeaturePython)
  n = 1
  ref = O_element
FEATURE [App::DocumentObjectGroupPython] G4_POTASSIUM_OXIDE  # scripted group (container) (typed FeaturePython)
  Dunit = g/cm3
  Dvalue = 2.32
  Group = -> [K_element009,O_element085]
  conduct = 2
  density = 1
  expand = 3
  formula = G4_POTASSIUM_OXIDE
  name = G4_POTASSIUM_OXIDE
  specific = 4
FEATURE [App::DocumentObjectGroupPython] C_element096  label="C_element : 054"  # scripted group (container) (typed FeaturePython)
  n = 3
  ref = C_element
FEATURE [App::DocumentObjectGroupPython] H_element088  label="H_element : 049"  # scripted group (container) (typed FeaturePython)
  n = 8
  ref = H_element
FEATURE [App::DocumentObjectGroupPython] G4_PROPANE  # scripted group (container) (typed FeaturePython)
  Dunit = g/cm3
  Dvalue = 0.00187939
  Group = -> [C_element096,H_element088]
  conduct = 2
  density = 1
  expand = 3
  formula = G4_PROPANE
  name = G4_PROPANE
  specific = 4
FEATURE [App::DocumentObjectGroupPython] C_element097  label="C_element : 055"  # scripted group (container) (typed FeaturePython)
  n = 3
  ref = C_element
FEATURE [App::DocumentObjectGroupPython] H_element089  label="H_element : 050"  # scripted group (container) (typed FeaturePython)
  n = 8
  ref = H_element
FEATURE [App::DocumentObjectGroupPython] G4_lPROPANE  # scripted group (container) (typed FeaturePython)
  Dunit = g/cm3
  Dvalue = 0.43
  Group = -> [C_element097,H_element089]
  conduct = 2
  density = 1
  expand = 3
  formula = G4_lPROPANE
  name = G4_lPROPANE
  specific = 4
FEATURE [App::DocumentObjectGroupPython] C_element098  label="C_element : 056"  # scripted group (container) (typed FeaturePython)
  n = 3
  ref = C_element
FEATURE [App::DocumentObjectGroupPython] H_element090  label="H_element : 051"  # scripted group (container) (typed FeaturePython)
  n = 8
  ref = H_element
FEATURE [App::DocumentObjectGroupPython] O_element086  label="O_element : 047"  # scripted group (container) (typed FeaturePython)
  n = 1
  ref = O_element
FEATURE [App::DocumentObjectGroupPython] G4_N_PROPYL_ALCOHOL  label="G4_N-PROPYL_ALCOHOL"  # scripted group (container) (typed FeaturePython)
  Dunit = g/cm3
  Dvalue = 0.8035
  Group = -> [C_element098,H_element090,O_element086]
  conduct = 2
  density = 1
  expand = 3
  formula = G4_N-PROPYL_ALCOHOL
  name = G4_N-PROPYL_ALCOHOL
  specific = 4
FEATURE [App::DocumentObjectGroupPython] C_element099  label="C_element : 057"  # scripted group (container) (typed FeaturePython)
  n = 5
  ref = C_element
FEATURE [App::DocumentObjectGroupPython] H_element091  label="H_element : 052"  # scripted group (container) (typed FeaturePython)
  n = 5
  ref = H_element
FEATURE [App::DocumentObjectGroupPython] N_element038  label="N_element : 017"  # scripted group (container) (typed FeaturePython)
  n = 1
  ref = N_element
FEATURE [App::DocumentObjectGroupPython] G4_PYRIDINE  # scripted group (container) (typed FeaturePython)
  Dunit = g/cm3
  Dvalue = 0.9819
  Group = -> [C_element099,H_element091,N_element038]
  conduct = 2
  density = 1
  expand = 3
  formula = G4_PYRIDINE
  name = G4_PYRIDINE
  specific = 4
FEATURE [App::DocumentObjectGroupPython] H_element092  label="H_element : 0.144"  # scripted group (container) (typed FeaturePython)
  n = 0.143711
FEATURE [App::DocumentObjectGroupPython] C_element100  label="C_element : 0.856"  # scripted group (container) (typed FeaturePython)
  n = 0.856289
FEATURE [App::DocumentObjectGroupPython] G4_RUBBER_BUTYL  # scripted group (container) (typed FeaturePython)
  Dunit = g/cm3
  Dvalue = 0.92
  Group = -> [H_element092,C_element100]
  conduct = 2
  density = 1
  expand = 3
  formula = G4_RUBBER_BUTYL
  name = G4_RUBBER_BUTYL
  specific = 4
FEATURE [App::DocumentObjectGroupPython] H_element093  label="H_element : 0.118"  # scripted group (container) (typed FeaturePython)
  n = 0.118371
FEATURE [App::DocumentObjectGroupPython] C_element101  label="C_element : 0.882"  # scripted group (container) (typed FeaturePython)
  n = 0.881629
FEATURE [App::DocumentObjectGroupPython] G4_RUBBER_NATURAL  # scripted group (container) (typed FeaturePython)
  Dunit = g/cm3
  Dvalue = 0.92
  Group = -> [H_element093,C_element101]
  conduct = 2
  density = 1
  expand = 3
  formula = G4_RUBBER_NATURAL
  name = G4_RUBBER_NATURAL
  specific = 4
FEATURE [App::DocumentObjectGroupPython] H_element094  label="H_element : 0.145"  # scripted group (container) (typed FeaturePython)
  n = 0.05692
FEATURE [App::DocumentObjectGroupPython] C_element102  label="C_element : 0.543"  # scripted group (container) (typed FeaturePython)
  n = 0.542646
FEATURE [App::DocumentObjectGroupPython] Cl_element021  label="Cl_element : 0.400"  # scripted group (container) (typed FeaturePython)
  n = 0.400434
FEATURE [App::DocumentObjectGroupPython] G4_RUBBER_NEOPRENE  # scripted group (container) (typed FeaturePython)
  Dunit = g/cm3
  Dvalue = 1.23
  Group = -> [H_element094,C_element102,Cl_element021]
  conduct = 2
  density = 1
  expand = 3
  formula = G4_RUBBER_NEOPRENE
  name = G4_RUBBER_NEOPRENE
  specific = 4
FEATURE [App::DocumentObjectGroupPython] Si_element006  label="Si_element : 1"  # scripted group (container) (typed FeaturePython)
  n = 1
  ref = Si_element
FEATURE [App::DocumentObjectGroupPython] O_element087  label="O_element : 048"  # scripted group (container) (typed FeaturePython)
  n = 2
  ref = O_element
FEATURE [App::DocumentObjectGroupPython] G4_SILICON_DIOXIDE002  label="G4_SILICON_DIOXIDE"  # scripted group (container) (typed FeaturePython)
  Dunit = g/cm3
  Dvalue = 2.32
  Group = -> [Si_element006,O_element087]
  conduct = 2
  density = 1
  expand = 3
  formula = G4_SILICON_DIOXIDE
  name = G4_SILICON_DIOXIDE
  specific = 4
FEATURE [App::DocumentObjectGroupPython] Ag_element002  label="Ag_element : 1"  # scripted group (container) (typed FeaturePython)
  n = 1
  ref = Ag_element
FEATURE [App::DocumentObjectGroupPython] Br_element005  label="Br_element : 003"  # scripted group (container) (typed FeaturePython)
  n = 1
  ref = Br_element
FEATURE [App::DocumentObjectGroupPython] G4_SILVER_BROMIDE  # scripted group (container) (typed FeaturePython)
  Dunit = g/cm3
  Dvalue = 6.473
  Group = -> [Ag_element002,Br_element005]
  conduct = 2
  density = 1
  expand = 3
  formula = G4_SILVER_BROMIDE
  name = G4_SILVER_BROMIDE
  specific = 4
FEATURE [App::DocumentObjectGroupPython] Ag_element003  label="Ag_element : 002"  # scripted group (container) (typed FeaturePython)
  n = 1
  ref = Ag_element
FEATURE [App::DocumentObjectGroupPython] Cl_element022  label="Cl_element : 011"  # scripted group (container) (typed FeaturePython)
  n = 1
  ref = Cl_element
FEATURE [App::DocumentObjectGroupPython] G4_SILVER_CHLORIDE  # scripted group (container) (typed FeaturePython)
  Dunit = g/cm3
  Dvalue = 5.56
  Group = -> [Ag_element003,Cl_element022]
  conduct = 2
  density = 1
  expand = 3
  formula = G4_SILVER_CHLORIDE
  name = G4_SILVER_CHLORIDE
  specific = 4
FEATURE [App::DocumentObjectGroupPython] Br_element006  label="Br_element : 0.423"  # scripted group (container) (typed FeaturePython)
  n = 0.422895
FEATURE [App::DocumentObjectGroupPython] Ag_element004  label="Ag_element : 0.574"  # scripted group (container) (typed FeaturePython)
  n = 0.573748
FEATURE [App::DocumentObjectGroupPython] I_element007  label="I_element : 0.649"  # scripted group (container) (typed FeaturePython)
  n = 0.003357
FEATURE [App::DocumentObjectGroupPython] G4_SILVER_HALIDES  # scripted group (container) (typed FeaturePython)
  Dunit = g/cm3
  Dvalue = 6.47
  Group = -> [Br_element006,Ag_element004,I_element007]
  conduct = 2
  density = 1
  expand = 3
  formula = G4_SILVER_HALIDES
  name = G4_SILVER_HALIDES
  specific = 4
FEATURE [App::DocumentObjectGroupPython] Ag_element005  label="Ag_element : 003"  # scripted group (container) (typed FeaturePython)
  n = 1
  ref = Ag_element
FEATURE [App::DocumentObjectGroupPython] I_element008  label="I_element : 004"  # scripted group (container) (typed FeaturePython)
  n = 1
  ref = I_element
FEATURE [App::DocumentObjectGroupPython] G4_SILVER_IODIDE  # scripted group (container) (typed FeaturePython)
  Dunit = g/cm3
  Dvalue = 6.01
  Group = -> [Ag_element005,I_element008]
  conduct = 2
  density = 1
  expand = 3
  formula = G4_SILVER_IODIDE
  name = G4_SILVER_IODIDE
  specific = 4
FEATURE [App::DocumentObjectGroupPython] H_element095  label="H_element : 0.100"  # scripted group (container) (typed FeaturePython)
  n = 0.1
FEATURE [App::DocumentObjectGroupPython] C_element103  label="C_element : 0.204"  # scripted group (container) (typed FeaturePython)
  n = 0.204
FEATURE [App::DocumentObjectGroupPython] N_element039  label="N_element : 0.759"  # scripted group (container) (typed FeaturePython)
  n = 0.042
FEATURE [App::DocumentObjectGroupPython] O_element088  label="O_element : 0.645"  # scripted group (container) (typed FeaturePython)
  n = 0.645
FEATURE [App::DocumentObjectGroupPython] Na_element013  label="Na_element : 0.100"  # scripted group (container) (typed FeaturePython)
  n = 0.002
FEATURE [App::DocumentObjectGroupPython] P_element009  label="P_element : 0.107"  # scripted group (container) (typed FeaturePython)
  n = 0.001
FEATURE [App::DocumentObjectGroupPython] S_element020  label="S_element : 0.021"  # scripted group (container) (typed FeaturePython)
  n = 0.002
FEATURE [App::DocumentObjectGroupPython] Cl_element023  label="Cl_element : 0.590"  # scripted group (container) (typed FeaturePython)
  n = 0.003
FEATURE [App::DocumentObjectGroupPython] K_element010  label="K_element : 0.001"  # scripted group (container) (typed FeaturePython)
  n = 0.001
FEATURE [App::DocumentObjectGroupPython] G4_SKIN_ICRP  # scripted group (container) (typed FeaturePython)
  Dunit = g/cm3
  Dvalue = 1.09
  Group = -> [H_element095,C_element103,N_element039,O_element088,Na_element013,P_element009,S_element020,Cl_element023,K_element010]
  conduct = 2
  density = 1
  expand = 3
  formula = G4_SKIN_ICRP
  name = G4_SKIN_ICRP
  specific = 4
FEATURE [App::DocumentObjectGroupPython] Na_element014  label="Na_element : 2"  # scripted group (container) (typed FeaturePython)
  n = 2
  ref = Na_element
FEATURE [App::DocumentObjectGroupPython] C_element104  label="C_element : 058"  # scripted group (container) (typed FeaturePython)
  n = 1
  ref = C_element
FEATURE [App::DocumentObjectGroupPython] O_element089  label="O_element : 049"  # scripted group (container) (typed FeaturePython)
  n = 3
  ref = O_element
FEATURE [App::DocumentObjectGroupPython] G4_SODIUM_CARBONATE  # scripted group (container) (typed FeaturePython)
  Dunit = g/cm3
  Dvalue = 2.532
  Group = -> [Na_element014,C_element104,O_element089]
  conduct = 2
  density = 1
  expand = 3
  formula = G4_SODIUM_CARBONATE
  name = G4_SODIUM_CARBONATE
  specific = 4
FEATURE [App::DocumentObjectGroupPython] Na_element015  label="Na_element : 1"  # scripted group (container) (typed FeaturePython)
  n = 1
  ref = Na_element
FEATURE [App::DocumentObjectGroupPython] I_element009  label="I_element : 005"  # scripted group (container) (typed FeaturePython)
  n = 1
  ref = I_element
FEATURE [App::DocumentObjectGroupPython] G4_SODIUM_IODIDE  # scripted group (container) (typed FeaturePython)
  Dunit = g/cm3
  Dvalue = 3.667
  Group = -> [Na_element015,I_element009]
  conduct = 2
  density = 1
  expand = 3
  formula = G4_SODIUM_IODIDE
  name = G4_SODIUM_IODIDE
  specific = 4
FEATURE [App::DocumentObjectGroupPython] Na_element016  label="Na_element : 003"  # scripted group (container) (typed FeaturePython)
  n = 2
  ref = Na_element
FEATURE [App::DocumentObjectGroupPython] O_element090  label="O_element : 050"  # scripted group (container) (typed FeaturePython)
  n = 1
  ref = O_element
FEATURE [App::DocumentObjectGroupPython] G4_SODIUM_MONOXIDE  # scripted group (container) (typed FeaturePython)
  Dunit = g/cm3
  Dvalue = 2.27
  Group = -> [Na_element016,O_element090]
  conduct = 2
  density = 1
  expand = 3
  formula = G4_SODIUM_MONOXIDE
  name = G4_SODIUM_MONOXIDE
  specific = 4
FEATURE [App::DocumentObjectGroupPython] Na_element017  label="Na_element : 004"  # scripted group (container) (typed FeaturePython)
  n = 1
  ref = Na_element
FEATURE [App::DocumentObjectGroupPython] N_element040  label="N_element : 018"  # scripted group (container) (typed FeaturePython)
  n = 1
  ref = N_element
FEATURE [App::DocumentObjectGroupPython] O_element091  label="O_element : 051"  # scripted group (container) (typed FeaturePython)
  n = 3
  ref = O_element
FEATURE [App::DocumentObjectGroupPython] G4_SODIUM_NITRATE  # scripted group (container) (typed FeaturePython)
  Dunit = g/cm3
  Dvalue = 2.261
  Group = -> [Na_element017,N_element040,O_element091]
  conduct = 2
  density = 1
  expand = 3
  formula = G4_SODIUM_NITRATE
  name = G4_SODIUM_NITRATE
  specific = 4
FEATURE [App::DocumentObjectGroupPython] C_element105  label="C_element : 059"  # scripted group (container) (typed FeaturePython)
  n = 14
  ref = C_element
FEATURE [App::DocumentObjectGroupPython] H_element096  label="H_element : 053"  # scripted group (container) (typed FeaturePython)
  n = 12
  ref = H_element
FEATURE [App::DocumentObjectGroupPython] G4_STILBENE  # scripted group (container) (typed FeaturePython)
  Dunit = g/cm3
  Dvalue = 0.9707
  Group = -> [C_element105,H_element096]
  conduct = 2
  density = 1
  expand = 3
  formula = G4_STILBENE
  name = G4_STILBENE
  specific = 4
FEATURE [App::DocumentObjectGroupPython] C_element106  label="C_element : 12"  # scripted group (container) (typed FeaturePython)
  n = 12
  ref = C_element
FEATURE [App::DocumentObjectGroupPython] H_element097  label="H_element : 22"  # scripted group (container) (typed FeaturePython)
  n = 22
  ref = H_element
FEATURE [App::DocumentObjectGroupPython] O_element092  label="O_element : 11"  # scripted group (container) (typed FeaturePython)
  n = 11
  ref = O_element
FEATURE [App::DocumentObjectGroupPython] G4_SUCROSE  # scripted group (container) (typed FeaturePython)
  Dunit = g/cm3
  Dvalue = 1.5805
  Group = -> [C_element106,H_element097,O_element092]
  conduct = 2
  density = 1
  expand = 3
  formula = G4_SUCROSE
  name = G4_SUCROSE
  specific = 4
FEATURE [App::DocumentObjectGroupPython] C_element107  label="C_element : 18"  # scripted group (container) (typed FeaturePython)
  n = 18
  ref = C_element
FEATURE [App::DocumentObjectGroupPython] H_element098  label="H_element : 054"  # scripted group (container) (typed FeaturePython)
  n = 14
  ref = H_element
FEATURE [App::DocumentObjectGroupPython] G4_TERPHENYL  # scripted group (container) (typed FeaturePython)
  Dunit = g/cm3
  Dvalue = 1.24
  Group = -> [C_element107,H_element098]
  conduct = 2
  density = 1
  expand = 3
  formula = G4_TERPHENYL
  name = G4_TERPHENYL
  specific = 4
FEATURE [App::DocumentObjectGroupPython] H_element099  label="H_element : 0.146"  # scripted group (container) (typed FeaturePython)
  n = 0.106
FEATURE [App::DocumentObjectGroupPython] C_element108  label="C_element : 0.883"  # scripted group (container) (typed FeaturePython)
  n = 0.099
FEATURE [App::DocumentObjectGroupPython] N_element041  label="N_element : 0.020"  # scripted group (container) (typed FeaturePython)
  n = 0.02
FEATURE [App::DocumentObjectGroupPython] O_element093  label="O_element : 0.766"  # scripted group (container) (typed FeaturePython)
  n = 0.766
FEATURE [App::DocumentObjectGroupPython] Na_element018  label="Na_element : 0.101"  # scripted group (container) (typed FeaturePython)
  n = 0.002
FEATURE [App::DocumentObjectGroupPython] P_element010  label="P_element : 0.108"  # scripted group (container) (typed FeaturePython)
  n = 0.001
FEATURE [App::DocumentObjectGroupPython] S_element021  label="S_element : 0.022"  # scripted group (container) (typed FeaturePython)
  n = 0.002
FEATURE [App::DocumentObjectGroupPython] Cl_element024  label="Cl_element : 0.002"  # scripted group (container) (typed FeaturePython)
  n = 0.002
FEATURE [App::DocumentObjectGroupPython] K_element011  label="K_element : 0.017"  # scripted group (container) (typed FeaturePython)
  n = 0.002
FEATURE [App::DocumentObjectGroupPython] G4_TESTIS_ICRP  # scripted group (container) (typed FeaturePython)
  Dunit = g/cm3
  Dvalue = 1.04
  Group = -> [H_element099,C_element108,N_element041,O_element093,Na_element018,P_element010,S_element021,Cl_element024,K_element011]
  conduct = 2
  density = 1
  expand = 3
  formula = G4_TESTIS_ICRP
  name = G4_TESTIS_ICRP
  specific = 4
FEATURE [App::DocumentObjectGroupPython] C_element109  label="C_element : 060"  # scripted group (container) (typed FeaturePython)
  n = 2
  ref = C_element
FEATURE [App::DocumentObjectGroupPython] Cl_element025  label="Cl_element : 012"  # scripted group (container) (typed FeaturePython)
  n = 4
  ref = Cl_element
FEATURE [App::DocumentObjectGroupPython] G4_TETRACHLOROETHYLENE  # scripted group (container) (typed FeaturePython)
  Dunit = g/cm3
  Dvalue = 1.625
  Group = -> [C_element109,Cl_element025]
  conduct = 2
  density = 1
  expand = 3
  formula = G4_TETRACHLOROETHYLENE
  name = G4_TETRACHLOROETHYLENE
  specific = 4
FEATURE [App::DocumentObjectGroupPython] Tl_element001  label="Tl_element : 1"  # scripted group (container) (typed FeaturePython)
  n = 1
  ref = Tl_element
FEATURE [App::DocumentObjectGroupPython] Cl_element026  label="Cl_element : 013"  # scripted group (container) (typed FeaturePython)
  n = 1
  ref = Cl_element
FEATURE [App::DocumentObjectGroupPython] G4_THALLIUM_CHLORIDE  # scripted group (container) (typed FeaturePython)
  Dunit = g/cm3
  Dvalue = 7.004
  Group = -> [Tl_element001,Cl_element026]
  conduct = 2
  density = 1
  expand = 3
  formula = G4_THALLIUM_CHLORIDE
  name = G4_THALLIUM_CHLORIDE
  specific = 4
FEATURE [App::DocumentObjectGroupPython] H_element100  label="H_element : 0.147"  # scripted group (container) (typed FeaturePython)
  n = 0.105
FEATURE [App::DocumentObjectGroupPython] C_element110  label="C_element : 0.256"  # scripted group (container) (typed FeaturePython)
  n = 0.256
FEATURE [App::DocumentObjectGroupPython] N_element042  label="N_element : 0.760"  # scripted group (container) (typed FeaturePython)
  n = 0.027
FEATURE [App::DocumentObjectGroupPython] O_element094  label="O_element : 0.602"  # scripted group (container) (typed FeaturePython)
  n = 0.602
FEATURE [App::DocumentObjectGroupPython] Na_element019  label="Na_element : 0.102"  # scripted group (container) (typed FeaturePython)
  n = 0.001
FEATURE [App::DocumentObjectGroupPython] P_element011  label="P_element : 0.109"  # scripted group (container) (typed FeaturePython)
  n = 0.002
FEATURE [App::DocumentObjectGroupPython] S_element022  label="S_element : 0.023"  # scripted group (container) (typed FeaturePython)
  n = 0.003
FEATURE [App::DocumentObjectGroupPython] Cl_element027  label="Cl_element : 0.591"  # scripted group (container) (typed FeaturePython)
  n = 0.002
FEATURE [App::DocumentObjectGroupPython] K_element012  label="K_element : 0.018"  # scripted group (container) (typed FeaturePython)
  n = 0.002
FEATURE [App::DocumentObjectGroupPython] G4_TISSUE_SOFT_ICRP  # scripted group (container) (typed FeaturePython)
  Dunit = g/cm3
  Dvalue = 1.03
  Group = -> [H_element100,C_element110,N_element042,O_element094,Na_element019,P_element011,S_element022,Cl_element027,K_element012]
  conduct = 2
  density = 1
  expand = 3
  formula = G4_TISSUE_SOFT_ICRP
  name = G4_TISSUE_SOFT_ICRP
  specific = 4
FEATURE [App::DocumentObjectGroupPython] H_element101  label="H_element : 0.148"  # scripted group (container) (typed FeaturePython)
  n = 0.101
FEATURE [App::DocumentObjectGroupPython] C_element111  label="C_element : 0.111"  # scripted group (container) (typed FeaturePython)
  n = 0.111
FEATURE [App::DocumentObjectGroupPython] N_element043  label="N_element : 0.026"  # scripted group (container) (typed FeaturePython)
  n = 0.026
FEATURE [App::DocumentObjectGroupPython] O_element095  label="O_element : 0.762"  # scripted group (container) (typed FeaturePython)
  n = 0.762
FEATURE [App::DocumentObjectGroupPython] G4_TISSUE_SOFT_ICRU_4  label="G4_TISSUE_SOFT_ICRU-4"  # scripted group (container) (typed FeaturePython)
  Dunit = g/cm3
  Dvalue = 1
  Group = -> [H_element101,C_element111,N_element043,O_element095]
  conduct = 2
  density = 1
  expand = 3
  formula = G4_TISSUE_SOFT_ICRU-4
  name = G4_TISSUE_SOFT_ICRU-4
  specific = 4
FEATURE [App::DocumentObjectGroupPython] H_element102  label="H_element : 0.149"  # scripted group (container) (typed FeaturePython)
  n = 0.101869
FEATURE [App::DocumentObjectGroupPython] C_element112  label="C_element : 0.456"  # scripted group (container) (typed FeaturePython)
  n = 0.456179
FEATURE [App::DocumentObjectGroupPython] N_element044  label="N_element : 0.761"  # scripted group (container) (typed FeaturePython)
  n = 0.035172
FEATURE [App::DocumentObjectGroupPython] O_element096  label="O_element : 0.407"  # scripted group (container) (typed FeaturePython)
  n = 0.40678
FEATURE [App::DocumentObjectGroupPython] G4_TISSUE_METHANE  label="G4_TISSUE-METHANE"  # scripted group (container) (typed FeaturePython)
  Dunit = g/cm3
  Dvalue = 0.00106409
  Group = -> [H_element102,C_element112,N_element044,O_element096]
  conduct = 2
  density = 1
  expand = 3
  formula = G4_TISSUE-METHANE
  name = G4_TISSUE-METHANE
  specific = 4
FEATURE [App::DocumentObjectGroupPython] H_element103  label="H_element : 0.103"  # scripted group (container) (typed FeaturePython)
  n = 0.102672
FEATURE [App::DocumentObjectGroupPython] C_element113  label="C_element : 0.569"  # scripted group (container) (typed FeaturePython)
  n = 0.56894
FEATURE [App::DocumentObjectGroupPython] N_element045  label="N_element : 0.762"  # scripted group (container) (typed FeaturePython)
  n = 0.035022
FEATURE [App::DocumentObjectGroupPython] O_element097  label="O_element : 0.293"  # scripted group (container) (typed FeaturePython)
  n = 0.293366
FEATURE [App::DocumentObjectGroupPython] G4_TISSUE_PROPANE  label="G4_TISSUE-PROPANE"  # scripted group (container) (typed FeaturePython)
  Dunit = g/cm3
  Dvalue = 0.00182628
  Group = -> [H_element103,C_element113,N_element045,O_element097]
  conduct = 2
  density = 1
  expand = 3
  formula = G4_TISSUE-PROPANE
  name = G4_TISSUE-PROPANE
  specific = 4
FEATURE [App::DocumentObjectGroupPython] Ti_element003  label="Ti_element : 1"  # scripted group (container) (typed FeaturePython)
  n = 1
  ref = Ti_element
FEATURE [App::DocumentObjectGroupPython] O_element098  label="O_element : 052"  # scripted group (container) (typed FeaturePython)
  n = 2
  ref = O_element
FEATURE [App::DocumentObjectGroupPython] G4_TITANIUM_DIOXIDE  # scripted group (container) (typed FeaturePython)
  Dunit = g/cm3
  Dvalue = 4.26
  Group = -> [Ti_element003,O_element098]
  conduct = 2
  density = 1
  expand = 3
  formula = G4_TITANIUM_DIOXIDE
  name = G4_TITANIUM_DIOXIDE
  specific = 4
FEATURE [App::DocumentObjectGroupPython] C_element114  label="C_element : 061"  # scripted group (container) (typed FeaturePython)
  n = 7
  ref = C_element
FEATURE [App::DocumentObjectGroupPython] H_element104  label="H_element : 055"  # scripted group (container) (typed FeaturePython)
  n = 8
  ref = H_element
FEATURE [App::DocumentObjectGroupPython] G4_TOLUENE  # scripted group (container) (typed FeaturePython)
  Dunit = g/cm3
  Dvalue = 0.8669
  Group = -> [C_element114,H_element104]
  conduct = 2
  density = 1
  expand = 3
  formula = G4_TOLUENE
  name = G4_TOLUENE
  specific = 4
FEATURE [App::DocumentObjectGroupPython] C_element115  label="C_element : 062"  # scripted group (container) (typed FeaturePython)
  n = 2
  ref = C_element
FEATURE [App::DocumentObjectGroupPython] H_element105  label="H_element : 056"  # scripted group (container) (typed FeaturePython)
  n = 1
  ref = H_element
FEATURE [App::DocumentObjectGroupPython] Cl_element028  label="Cl_element : 014"  # scripted group (container) (typed FeaturePython)
  n = 3
  ref = Cl_element
FEATURE [App::DocumentObjectGroupPython] G4_TRICHLOROETHYLENE  # scripted group (container) (typed FeaturePython)
  Dunit = g/cm3
  Dvalue = 1.46
  Group = -> [C_element115,H_element105,Cl_element028]
  conduct = 2
  density = 1
  expand = 3
  formula = G4_TRICHLOROETHYLENE
  name = G4_TRICHLOROETHYLENE
  specific = 4
FEATURE [App::DocumentObjectGroupPython] C_element116  label="C_element : 063"  # scripted group (container) (typed FeaturePython)
  n = 6
  ref = C_element
FEATURE [App::DocumentObjectGroupPython] H_element106  label="H_element : 15"  # scripted group (container) (typed FeaturePython)
  n = 15
  ref = H_element
FEATURE [App::DocumentObjectGroupPython] O_element099  label="O_element : 053"  # scripted group (container) (typed FeaturePython)
  n = 4
  ref = O_element
FEATURE [App::DocumentObjectGroupPython] P_element012  label="P_element : 1"  # scripted group (container) (typed FeaturePython)
  n = 1
  ref = P_element
FEATURE [App::DocumentObjectGroupPython] G4_TRIETHYL_PHOSPHATE  # scripted group (container) (typed FeaturePython)
  Dunit = g/cm3
  Dvalue = 1.07
  Group = -> [C_element116,H_element106,O_element099,P_element012]
  conduct = 2
  density = 1
  expand = 3
  formula = G4_TRIETHYL_PHOSPHATE
  name = G4_TRIETHYL_PHOSPHATE
  specific = 4
FEATURE [App::DocumentObjectGroupPython] W_element003  label="W_element : 003"  # scripted group (container) (typed FeaturePython)
  n = 1
  ref = W_element
FEATURE [App::DocumentObjectGroupPython] F_element017  label="F_element : 6"  # scripted group (container) (typed FeaturePython)
  n = 6
  ref = F_element
FEATURE [App::DocumentObjectGroupPython] G4_TUNGSTEN_HEXAFLUORIDE  # scripted group (container) (typed FeaturePython)
  Dunit = g/cm3
  Dvalue = 2.4
  Group = -> [W_element003,F_element017]
  conduct = 2
  density = 1
  expand = 3
  formula = G4_TUNGSTEN_HEXAFLUORIDE
  name = G4_TUNGSTEN_HEXAFLUORIDE
  specific = 4
FEATURE [App::DocumentObjectGroupPython] U_element001  label="U_element : 1"  # scripted group (container) (typed FeaturePython)
  n = 1
  ref = U_element
FEATURE [App::DocumentObjectGroupPython] C_element117  label="C_element : 064"  # scripted group (container) (typed FeaturePython)
  n = 2
  ref = C_element
FEATURE [App::DocumentObjectGroupPython] G4_URANIUM_DICARBIDE  # scripted group (container) (typed FeaturePython)
  Dunit = g/cm3
  Dvalue = 11.28
  Group = -> [U_element001,C_element117]
  conduct = 2
  density = 1
  expand = 3
  formula = G4_URANIUM_DICARBIDE
  name = G4_URANIUM_DICARBIDE
  specific = 4
FEATURE [App::DocumentObjectGroupPython] U_element002  label="U_element : 002"  # scripted group (container) (typed FeaturePython)
  n = 1
  ref = U_element
FEATURE [App::DocumentObjectGroupPython] C_element118  label="C_element : 065"  # scripted group (container) (typed FeaturePython)
  n = 1
  ref = C_element
FEATURE [App::DocumentObjectGroupPython] G4_URANIUM_MONOCARBIDE  # scripted group (container) (typed FeaturePython)
  Dunit = g/cm3
  Dvalue = 13.63
  Group = -> [U_element002,C_element118]
  conduct = 2
  density = 1
  expand = 3
  formula = G4_URANIUM_MONOCARBIDE
  name = G4_URANIUM_MONOCARBIDE
  specific = 4
FEATURE [App::DocumentObjectGroupPython] U_element003  label="U_element : 003"  # scripted group (container) (typed FeaturePython)
  n = 1
  ref = U_element
FEATURE [App::DocumentObjectGroupPython] O_element100  label="O_element : 054"  # scripted group (container) (typed FeaturePython)
  n = 2
  ref = O_element
FEATURE [App::DocumentObjectGroupPython] G4_URANIUM_OXIDE  # scripted group (container) (typed FeaturePython)
  Dunit = g/cm3
  Dvalue = 10.96
  Group = -> [U_element003,O_element100]
  conduct = 2
  density = 1
  expand = 3
  formula = G4_URANIUM_OXIDE
  name = G4_URANIUM_OXIDE
  specific = 4
FEATURE [App::DocumentObjectGroupPython] C_element119  label="C_element : 066"  # scripted group (container) (typed FeaturePython)
  n = 1
  ref = C_element
FEATURE [App::DocumentObjectGroupPython] H_element107  label="H_element : 057"  # scripted group (container) (typed FeaturePython)
  n = 4
  ref = H_element
FEATURE [App::DocumentObjectGroupPython] N_element046  label="N_element : 019"  # scripted group (container) (typed FeaturePython)
  n = 2
  ref = N_element
FEATURE [App::DocumentObjectGroupPython] O_element101  label="O_element : 055"  # scripted group (container) (typed FeaturePython)
  n = 1
  ref = O_element
FEATURE [App::DocumentObjectGroupPython] G4_UREA  # scripted group (container) (typed FeaturePython)
  Dunit = g/cm3
  Dvalue = 1.323
  Group = -> [C_element119,H_element107,N_element046,O_element101]
  conduct = 2
  density = 1
  expand = 3
  formula = G4_UREA
  name = G4_UREA
  specific = 4
FEATURE [App::DocumentObjectGroupPython] C_element120  label="C_element : 067"  # scripted group (container) (typed FeaturePython)
  n = 5
  ref = C_element
FEATURE [App::DocumentObjectGroupPython] H_element108  label="H_element : 058"  # scripted group (container) (typed FeaturePython)
  n = 11
  ref = H_element
FEATURE [App::DocumentObjectGroupPython] N_element047  label="N_element : 020"  # scripted group (container) (typed FeaturePython)
  n = 1
  ref = N_element
FEATURE [App::DocumentObjectGroupPython] O_element102  label="O_element : 056"  # scripted group (container) (typed FeaturePython)
  n = 2
  ref = O_element
FEATURE [App::DocumentObjectGroupPython] G4_VALINE  # scripted group (container) (typed FeaturePython)
  Dunit = g/cm3
  Dvalue = 1.23
  Group = -> [C_element120,H_element108,N_element047,O_element102]
  conduct = 2
  density = 1
  expand = 3
  formula = G4_VALINE
  name = G4_VALINE
  specific = 4
FEATURE [App::DocumentObjectGroupPython] H_element109  label="H_element : 0.009"  # scripted group (container) (typed FeaturePython)
  n = 0.009417
FEATURE [App::DocumentObjectGroupPython] C_element121  label="C_element : 0.281"  # scripted group (container) (typed FeaturePython)
  n = 0.280555
FEATURE [App::DocumentObjectGroupPython] F_element018  label="F_element : 0.710"  # scripted group (container) (typed FeaturePython)
  n = 0.710028
FEATURE [App::DocumentObjectGroupPython] G4_VITON  # scripted group (container) (typed FeaturePython)
  Dunit = g/cm3
  Dvalue = 1.8
  Group = -> [H_element109,C_element121,F_element018]
  conduct = 2
  density = 1
  expand = 3
  formula = G4_VITON
  name = G4_VITON
  specific = 4
FEATURE [App::DocumentObjectGroupPython] H_element110  label="H_element : 059"  # scripted group (container) (typed FeaturePython)
  n = 2
  ref = H_element
FEATURE [App::DocumentObjectGroupPython] O_element103  label="O_element : 057"  # scripted group (container) (typed FeaturePython)
  n = 1
  ref = O_element
FEATURE [App::DocumentObjectGroupPython] G4_WATER  # scripted group (container) (typed FeaturePython)
  Dunit = g/cm3
  Dvalue = 1
  Group = -> [H_element110,O_element103]
  conduct = 2
  density = 1
  expand = 3
  formula = G4_WATER
  name = G4_WATER
  specific = 4
FEATURE [App::DocumentObjectGroupPython] H_element111  label="H_element : 060"  # scripted group (container) (typed FeaturePython)
  n = 2
  ref = H_element
FEATURE [App::DocumentObjectGroupPython] O_element104  label="O_element : 058"  # scripted group (container) (typed FeaturePython)
  n = 1
  ref = O_element
FEATURE [App::DocumentObjectGroupPython] G4_WATER_VAPOR  # scripted group (container) (typed FeaturePython)
  Dunit = g/cm3
  Dvalue = 0.000756182
  Group = -> [H_element111,O_element104]
  conduct = 2
  density = 1
  expand = 3
  formula = G4_WATER_VAPOR
  name = G4_WATER_VAPOR
  specific = 4
FEATURE [App::DocumentObjectGroupPython] C_element122  label="C_element : 068"  # scripted group (container) (typed FeaturePython)
  n = 8
  ref = C_element
FEATURE [App::DocumentObjectGroupPython] H_element112  label="H_element : 061"  # scripted group (container) (typed FeaturePython)
  n = 10
  ref = H_element
FEATURE [App::DocumentObjectGroupPython] G4_XYLENE  # scripted group (container) (typed FeaturePython)
  Dunit = g/cm3
  Dvalue = 0.87
  Group = -> [C_element122,H_element112]
  conduct = 2
  density = 1
  expand = 3
  formula = G4_XYLENE
  name = G4_XYLENE
  specific = 4
FEATURE [App::DocumentObjectGroupPython] C_element123  label="C_element : 069"  # scripted group (container) (typed FeaturePython)
  n = 1
  ref = C_element
FEATURE [App::DocumentObjectGroupPython] G4_GRAPHITE  # scripted group (container) (typed FeaturePython)
  Dunit = g/cm3
  Dvalue = 2.21
  Group = -> [C_element123]
  conduct = 2
  density = 1
  expand = 3
  formula = G4_GRAPHITE
  name = G4_GRAPHITE
  specific = 4
FEATURE [App::DocumentObjectGroupPython] NIST  # scripted group (container) (typed FeaturePython)
  Group = -> [G4_A_150_TISSUE,G4_ACETONE,G4_ACETYLENE,G4_ADENINE,G4_ADIPOSE_TISSUE_ICRP,G4_AIR001,G4_ALANINE,G4_ALUMINUM_OXIDE,G4_AMBER,G4_AMMONIA,G4_ANILINE,G4_ANTHRACENE,G4_B_100_BONE,G4_BAKELITE,G4_BARIUM_FLUORIDE,G4_BARIUM_SULFATE,G4_BENZENE,G4_BERYLLIUM_OXIDE,G4_BGO,G4_BLOOD_ICRP,G4_BONE_COMPACT_ICRU,G4_BONE_CORTICAL_ICRP,G4_BORON_CARBIDE,G4_BORON_OXIDE,G4_BRAIN_ICRP,G4_BUTANE,G4_N_BUTYL_ALCOHOL,G4_C_552,+152 more]
FEATURE [App::DocumentObjectGroupPython] H_element113  label="H_element : 062"  # scripted group (container) (typed FeaturePython)
  n = 1
  ref = H_element
FEATURE [App::DocumentObjectGroupPython] G4_H  # scripted group (container) (typed FeaturePython)
  Dunit = g/cm3
  Dvalue = 8.3748e-05
  Group = -> [H_element113]
  conduct = 2
  density = 1
  expand = 3
  formula = H
  name = G4_H
  specific = 4
FEATURE [App::DocumentObjectGroupPython] He_element001  label="He_element : 1"  # scripted group (container) (typed FeaturePython)
  n = 1
  ref = He_element
FEATURE [App::DocumentObjectGroupPython] G4_He  # scripted group (container) (typed FeaturePython)
  Dunit = g/cm3
  Dvalue = 0.000166322
  Group = -> [He_element001]
  conduct = 2
  density = 1
  expand = 3
  formula = He
  name = G4_He
  specific = 4
FEATURE [App::DocumentObjectGroupPython] Li_element008  label="Li_element : 008"  # scripted group (container) (typed FeaturePython)
  n = 1
  ref = Li_element
FEATURE [App::DocumentObjectGroupPython] G4_Li  # scripted group (container) (typed FeaturePython)
  Dunit = g/cm3
  Dvalue = 0.534
  Group = -> [Li_element008]
  conduct = 2
  density = 1
  expand = 3
  formula = Li
  name = G4_Li
  specific = 4
FEATURE [App::DocumentObjectGroupPython] Be_element002  label="Be_element : 002"  # scripted group (container) (typed FeaturePython)
  n = 1
  ref = Be_element
FEATURE [App::DocumentObjectGroupPython] G4_Be  # scripted group (container) (typed FeaturePython)
  Dunit = g/cm3
  Dvalue = 1.848
  Group = -> [Be_element002]
  conduct = 2
  density = 1
  expand = 3
  formula = Be
  name = G4_Be
  specific = 4
FEATURE [App::DocumentObjectGroupPython] B_element007  label="B_element : 007"  # scripted group (container) (typed FeaturePython)
  n = 1
  ref = B_element
FEATURE [App::DocumentObjectGroupPython] G4_B  # scripted group (container) (typed FeaturePython)
  Dunit = g/cm3
  Dvalue = 2.37
  Group = -> [B_element007]
  conduct = 2
  density = 1
  expand = 3
  formula = B
  name = G4_B
  specific = 4
FEATURE [App::DocumentObjectGroupPython] C_element124  label="C_element : 070"  # scripted group (container) (typed FeaturePython)
  n = 1
  ref = C_element
FEATURE [App::DocumentObjectGroupPython] G4_C  # scripted group (container) (typed FeaturePython)
  Dunit = g/cm3
  Dvalue = 2
  Group = -> [C_element124]
  conduct = 2
  density = 1
  expand = 3
  formula = C
  name = G4_C
  specific = 4
FEATURE [App::DocumentObjectGroupPython] N_element048  label="N_element : 021"  # scripted group (container) (typed FeaturePython)
  n = 1
  ref = N_element
FEATURE [App::DocumentObjectGroupPython] G4_N  # scripted group (container) (typed FeaturePython)
  Dunit = g/cm3
  Dvalue = 0.0011652
  Group = -> [N_element048]
  conduct = 2
  density = 1
  expand = 3
  formula = N
  name = G4_N
  specific = 4
FEATURE [App::DocumentObjectGroupPython] O_element105  label="O_element : 059"  # scripted group (container) (typed FeaturePython)
  n = 1
  ref = O_element
FEATURE [App::DocumentObjectGroupPython] G4_O  # scripted group (container) (typed FeaturePython)
  Dunit = g/cm3
  Dvalue = 0.00133151
  Group = -> [O_element105]
  conduct = 2
  density = 1
  expand = 3
  formula = O
  name = G4_O
  specific = 4
FEATURE [App::DocumentObjectGroupPython] F_element019  label="F_element : 008"  # scripted group (container) (typed FeaturePython)
  n = 1
  ref = F_element
FEATURE [App::DocumentObjectGroupPython] G4_F  # scripted group (container) (typed FeaturePython)
  Dunit = g/cm3
  Dvalue = 0.00158029
  Group = -> [F_element019]
  conduct = 2
  density = 1
  expand = 3
  formula = F
  name = G4_F
  specific = 4
FEATURE [App::DocumentObjectGroupPython] Ne_element001  label="Ne_element : 1"  # scripted group (container) (typed FeaturePython)
  n = 1
  ref = Ne_element
FEATURE [App::DocumentObjectGroupPython] G4_Ne  # scripted group (container) (typed FeaturePython)
  Dunit = g/cm3
  Dvalue = 0.000838505
  Group = -> [Ne_element001]
  conduct = 2
  density = 1
  expand = 3
  formula = Ne
  name = G4_Ne
  specific = 4
FEATURE [App::DocumentObjectGroupPython] Na_element020  label="Na_element : 005"  # scripted group (container) (typed FeaturePython)
  n = 1
  ref = Na_element
FEATURE [App::DocumentObjectGroupPython] G4_Na  # scripted group (container) (typed FeaturePython)
  Dunit = g/cm3
  Dvalue = 0.971
  Group = -> [Na_element020]
  conduct = 2
  density = 1
  expand = 3
  formula = Na
  name = G4_Na
  specific = 4
FEATURE [App::DocumentObjectGroupPython] Mg_element011  label="Mg_element : 005"  # scripted group (container) (typed FeaturePython)
  n = 1
  ref = Mg_element
FEATURE [App::DocumentObjectGroupPython] G4_Mg  # scripted group (container) (typed FeaturePython)
  Dunit = g/cm3
  Dvalue = 1.74
  Group = -> [Mg_element011]
  conduct = 2
  density = 1
  expand = 3
  formula = Mg
  name = G4_Mg
  specific = 4
FEATURE [App::DocumentObjectGroupPython] Al_element004  label="Al_element : 1"  # scripted group (container) (typed FeaturePython)
  n = 1
  ref = Al_element
FEATURE [App::DocumentObjectGroupPython] G4_Al  # scripted group (container) (typed FeaturePython)
  Dunit = g/cm3
  Dvalue = 2.699
  Group = -> [Al_element004]
  conduct = 2
  density = 1
  expand = 3
  formula = Al
  name = G4_Al
  specific = 4
FEATURE [App::DocumentObjectGroupPython] Si_element007  label="Si_element : 002"  # scripted group (container) (typed FeaturePython)
  n = 1
  ref = Si_element
FEATURE [App::DocumentObjectGroupPython] G4_Si  # scripted group (container) (typed FeaturePython)
  Dunit = g/cm3
  Dvalue = 2.33
  Group = -> [Si_element007]
  conduct = 2
  density = 1
  expand = 3
  formula = Si
  name = G4_Si
  specific = 4
FEATURE [App::DocumentObjectGroupPython] P_element013  label="P_element : 002"  # scripted group (container) (typed FeaturePython)
  n = 1
  ref = P_element
FEATURE [App::DocumentObjectGroupPython] G4_P  # scripted group (container) (typed FeaturePython)
  Dunit = g/cm3
  Dvalue = 2.2
  Group = -> [P_element013]
  conduct = 2
  density = 1
  expand = 3
  formula = P
  name = G4_P
  specific = 4
FEATURE [App::DocumentObjectGroupPython] S_element023  label="S_element : 007"  # scripted group (container) (typed FeaturePython)
  n = 1
  ref = S_element
FEATURE [App::DocumentObjectGroupPython] G4_S  # scripted group (container) (typed FeaturePython)
  Dunit = g/cm3
  Dvalue = 2
  Group = -> [S_element023]
  conduct = 2
  density = 1
  expand = 3
  formula = S
  name = G4_S
  specific = 4
FEATURE [App::DocumentObjectGroupPython] Cl_element029  label="Cl_element : 015"  # scripted group (container) (typed FeaturePython)
  n = 1
  ref = Cl_element
FEATURE [App::DocumentObjectGroupPython] G4_Cl  # scripted group (container) (typed FeaturePython)
  Dunit = g/cm3
  Dvalue = 0.00299473
  Group = -> [Cl_element029]
  conduct = 2
  density = 1
  expand = 3
  formula = Cl
  name = G4_Cl
  specific = 4
FEATURE [App::DocumentObjectGroupPython] Ar_element002  label="Ar_element : 1"  # scripted group (container) (typed FeaturePython)
  n = 1
  ref = Ar_element
FEATURE [App::DocumentObjectGroupPython] G4_Ar  # scripted group (container) (typed FeaturePython)
  Dunit = g/cm3
  Dvalue = 0.00166201
  Group = -> [Ar_element002]
  conduct = 2
  density = 1
  expand = 3
  formula = Ar
  name = G4_Ar
  specific = 4
FEATURE [App::DocumentObjectGroupPython] K_element013  label="K_element : 003"  # scripted group (container) (typed FeaturePython)
  n = 1
  ref = K_element
FEATURE [App::DocumentObjectGroupPython] G4_K  # scripted group (container) (typed FeaturePython)
  Dunit = g/cm3
  Dvalue = 0.862
  Group = -> [K_element013]
  conduct = 2
  density = 1
  expand = 3
  formula = K
  name = G4_K
  specific = 4
FEATURE [App::DocumentObjectGroupPython] Ca_element014  label="Ca_element : 007"  # scripted group (container) (typed FeaturePython)
  n = 1
  ref = Ca_element
FEATURE [App::DocumentObjectGroupPython] G4_Ca  # scripted group (container) (typed FeaturePython)
  Dunit = g/cm3
  Dvalue = 1.55
  Group = -> [Ca_element014]
  conduct = 2
  density = 1
  expand = 3
  formula = Ca
  name = G4_Ca
  specific = 4
FEATURE [App::DocumentObjectGroupPython] Sc_element001  label="Sc_element : 1"  # scripted group (container) (typed FeaturePython)
  n = 1
  ref = Sc_element
FEATURE [App::DocumentObjectGroupPython] G4_Sc  # scripted group (container) (typed FeaturePython)
  Dunit = g/cm3
  Dvalue = 2.989
  Group = -> [Sc_element001]
  conduct = 2
  density = 1
  expand = 3
  formula = Sc
  name = G4_Sc
  specific = 4
FEATURE [App::DocumentObjectGroupPython] Ti_element004  label="Ti_element : 002"  # scripted group (container) (typed FeaturePython)
  n = 1
  ref = Ti_element
FEATURE [App::DocumentObjectGroupPython] G4_Ti  # scripted group (container) (typed FeaturePython)
  Dunit = g/cm3
  Dvalue = 4.54
  Group = -> [Ti_element004]
  conduct = 2
  density = 1
  expand = 3
  formula = Ti
  name = G4_Ti
  specific = 4
FEATURE [App::DocumentObjectGroupPython] V_element001  label="V_element : 1"  # scripted group (container) (typed FeaturePython)
  n = 1
  ref = V_element
FEATURE [App::DocumentObjectGroupPython] G4_V  # scripted group (container) (typed FeaturePython)
  Dunit = g/cm3
  Dvalue = 6.11
  Group = -> [V_element001]
  conduct = 2
  density = 1
  expand = 3
  formula = V
  name = G4_V
  specific = 4
FEATURE [App::DocumentObjectGroupPython] Cr_element001  label="Cr_element : 1"  # scripted group (container) (typed FeaturePython)
  n = 1
  ref = Cr_element
FEATURE [App::DocumentObjectGroupPython] G4_Cr  # scripted group (container) (typed FeaturePython)
  Dunit = g/cm3
  Dvalue = 7.18
  Group = -> [Cr_element001]
  conduct = 2
  density = 1
  expand = 3
  formula = Cr
  name = G4_Cr
  specific = 4
FEATURE [App::DocumentObjectGroupPython] Mn_element001  label="Mn_element : 1"  # scripted group (container) (typed FeaturePython)
  n = 1
  ref = Mn_element
FEATURE [App::DocumentObjectGroupPython] G4_Mn  # scripted group (container) (typed FeaturePython)
  Dunit = g/cm3
  Dvalue = 7.44
  Group = -> [Mn_element001]
  conduct = 2
  density = 1
  expand = 3
  formula = Mn
  name = G4_Mn
  specific = 4
FEATURE [App::DocumentObjectGroupPython] Fe_element007  label="Fe_element : 004"  # scripted group (container) (typed FeaturePython)
  n = 1
  ref = Fe_element
FEATURE [App::DocumentObjectGroupPython] G4_Fe  # scripted group (container) (typed FeaturePython)
  Dunit = g/cm3
  Dvalue = 7.874
  Group = -> [Fe_element007]
  conduct = 2
  density = 1
  expand = 3
  formula = Fe
  name = G4_Fe
  specific = 4
FEATURE [App::DocumentObjectGroupPython] Co_element001  label="Co_element : 1"  # scripted group (container) (typed FeaturePython)
  n = 1
  ref = Co_element
FEATURE [App::DocumentObjectGroupPython] G4_Co  # scripted group (container) (typed FeaturePython)
  Dunit = g/cm3
  Dvalue = 8.9
  Group = -> [Co_element001]
  conduct = 2
  density = 1
  expand = 3
  formula = Co
  name = G4_Co
  specific = 4
FEATURE [App::DocumentObjectGroupPython] Ni_element001  label="Ni_element : 1"  # scripted group (container) (typed FeaturePython)
  n = 1
  ref = Ni_element
FEATURE [App::DocumentObjectGroupPython] G4_Ni  # scripted group (container) (typed FeaturePython)
  Dunit = g/cm3
  Dvalue = 8.902
  Group = -> [Ni_element001]
  conduct = 2
  density = 1
  expand = 3
  formula = Ni
  name = G4_Ni
  specific = 4
FEATURE [App::DocumentObjectGroupPython] Cu_element001  label="Cu_element : 1"  # scripted group (container) (typed FeaturePython)
  n = 1
  ref = Cu_element
FEATURE [App::DocumentObjectGroupPython] G4_Cu  # scripted group (container) (typed FeaturePython)
  Dunit = g/cm3
  Dvalue = 8.96
  Group = -> [Cu_element001]
  conduct = 2
  density = 1
  expand = 3
  formula = Cu
  name = G4_Cu
  specific = 4
FEATURE [App::DocumentObjectGroupPython] Zn_element001  label="Zn_element : 1"  # scripted group (container) (typed FeaturePython)
  n = 1
  ref = Zn_element
FEATURE [App::DocumentObjectGroupPython] G4_Zn  # scripted group (container) (typed FeaturePython)
  Dunit = g/cm3
  Dvalue = 7.133
  Group = -> [Zn_element001]
  conduct = 2
  density = 1
  expand = 3
  formula = Zn
  name = G4_Zn
  specific = 4
FEATURE [App::DocumentObjectGroupPython] Ga_element002  label="Ga_element : 002"  # scripted group (container) (typed FeaturePython)
  n = 1
  ref = Ga_element
FEATURE [App::DocumentObjectGroupPython] G4_Ga  # scripted group (container) (typed FeaturePython)
  Dunit = g/cm3
  Dvalue = 5.904
  Group = -> [Ga_element002]
  conduct = 2
  density = 1
  expand = 3
  formula = Ga
  name = G4_Ga
  specific = 4
FEATURE [App::DocumentObjectGroupPython] Ge_element002  label="Ge_element : 1"  # scripted group (container) (typed FeaturePython)
  n = 1
  ref = Ge_element
FEATURE [App::DocumentObjectGroupPython] G4_Ge  # scripted group (container) (typed FeaturePython)
  Dunit = g/cm3
  Dvalue = 5.323
  Group = -> [Ge_element002]
  conduct = 2
  density = 1
  expand = 3
  formula = Ge
  name = G4_Ge
  specific = 4
FEATURE [App::DocumentObjectGroupPython] As_element003  label="As_element : 002"  # scripted group (container) (typed FeaturePython)
  n = 1
  ref = As_element
FEATURE [App::DocumentObjectGroupPython] G4_As  # scripted group (container) (typed FeaturePython)
  Dunit = g/cm3
  Dvalue = 5.73
  Group = -> [As_element003]
  conduct = 2
  density = 1
  expand = 3
  formula = As
  name = G4_As
  specific = 4
FEATURE [App::DocumentObjectGroupPython] Se_element001  label="Se_element : 1"  # scripted group (container) (typed FeaturePython)
  n = 1
  ref = Se_element
FEATURE [App::DocumentObjectGroupPython] G4_Se  # scripted group (container) (typed FeaturePython)
  Dunit = g/cm3
  Dvalue = 4.5
  Group = -> [Se_element001]
  conduct = 2
  density = 1
  expand = 3
  formula = Se
  name = G4_Se
  specific = 4
FEATURE [App::DocumentObjectGroupPython] Br_element007  label="Br_element : 004"  # scripted group (container) (typed FeaturePython)
  n = 1
  ref = Br_element
FEATURE [App::DocumentObjectGroupPython] G4_Br  # scripted group (container) (typed FeaturePython)
  Dunit = g/cm3
  Dvalue = 0.0070721
  Group = -> [Br_element007]
  conduct = 2
  density = 1
  expand = 3
  formula = Br
  name = G4_Br
  specific = 4
FEATURE [App::DocumentObjectGroupPython] Kr_element001  label="Kr_element : 1"  # scripted group (container) (typed FeaturePython)
  n = 1
  ref = Kr_element
FEATURE [App::DocumentObjectGroupPython] G4_Kr  # scripted group (container) (typed FeaturePython)
  Dunit = g/cm3
  Dvalue = 0.00347832
  Group = -> [Kr_element001]
  conduct = 2
  density = 1
  expand = 3
  formula = Kr
  name = G4_Kr
  specific = 4
FEATURE [App::DocumentObjectGroupPython] Rb_element001  label="Rb_element : 1"  # scripted group (container) (typed FeaturePython)
  n = 1
  ref = Rb_element
FEATURE [App::DocumentObjectGroupPython] G4_Rb  # scripted group (container) (typed FeaturePython)
  Dunit = g/cm3
  Dvalue = 1.532
  Group = -> [Rb_element001]
  conduct = 2
  density = 1
  expand = 3
  formula = Rb
  name = G4_Rb
  specific = 4
FEATURE [App::DocumentObjectGroupPython] Sr_element001  label="Sr_element : 1"  # scripted group (container) (typed FeaturePython)
  n = 1
  ref = Sr_element
FEATURE [App::DocumentObjectGroupPython] G4_Sr  # scripted group (container) (typed FeaturePython)
  Dunit = g/cm3
  Dvalue = 2.54
  Group = -> [Sr_element001]
  conduct = 2
  density = 1
  expand = 3
  formula = Sr
  name = G4_Sr
  specific = 4
FEATURE [App::DocumentObjectGroupPython] Y_element001  label="Y_element : 1"  # scripted group (container) (typed FeaturePython)
  n = 1
  ref = Y_element
FEATURE [App::DocumentObjectGroupPython] G4_Y  # scripted group (container) (typed FeaturePython)
  Dunit = g/cm3
  Dvalue = 4.469
  Group = -> [Y_element001]
  conduct = 2
  density = 1
  expand = 3
  formula = Y
  name = G4_Y
  specific = 4
FEATURE [App::DocumentObjectGroupPython] Zr_element001  label="Zr_element : 1"  # scripted group (container) (typed FeaturePython)
  n = 1
  ref = Zr_element
FEATURE [App::DocumentObjectGroupPython] G4_Zr  # scripted group (container) (typed FeaturePython)
  Dunit = g/cm3
  Dvalue = 6.506
  Group = -> [Zr_element001]
  conduct = 2
  density = 1
  expand = 3
  formula = Zr
  name = G4_Zr
  specific = 4
FEATURE [App::DocumentObjectGroupPython] Nb_element001  label="Nb_element : 1"  # scripted group (container) (typed FeaturePython)
  n = 1
  ref = Nb_element
FEATURE [App::DocumentObjectGroupPython] G4_Nb  # scripted group (container) (typed FeaturePython)
  Dunit = g/cm3
  Dvalue = 8.57
  Group = -> [Nb_element001]
  conduct = 2
  density = 1
  expand = 3
  formula = Nb
  name = G4_Nb
  specific = 4
FEATURE [App::DocumentObjectGroupPython] Mo_element001  label="Mo_element : 1"  # scripted group (container) (typed FeaturePython)
  n = 1
  ref = Mo_element
FEATURE [App::DocumentObjectGroupPython] G4_Mo  # scripted group (container) (typed FeaturePython)
  Dunit = g/cm3
  Dvalue = 10.22
  Group = -> [Mo_element001]
  conduct = 2
  density = 1
  expand = 3
  formula = Mo
  name = G4_Mo
  specific = 4
FEATURE [App::DocumentObjectGroupPython] Tc_element001  label="Tc_element : 1"  # scripted group (container) (typed FeaturePython)
  n = 1
  ref = Tc_element
FEATURE [App::DocumentObjectGroupPython] G4_Tc  # scripted group (container) (typed FeaturePython)
  Dunit = g/cm3
  Dvalue = 11.5
  Group = -> [Tc_element001]
  conduct = 2
  density = 1
  expand = 3
  formula = Tc
  name = G4_Tc
  specific = 4
FEATURE [App::DocumentObjectGroupPython] Ru_element001  label="Ru_element : 1"  # scripted group (container) (typed FeaturePython)
  n = 1
  ref = Ru_element
FEATURE [App::DocumentObjectGroupPython] G4_Ru  # scripted group (container) (typed FeaturePython)
  Dunit = g/cm3
  Dvalue = 12.41
  Group = -> [Ru_element001]
  conduct = 2
  density = 1
  expand = 3
  formula = Ru
  name = G4_Ru
  specific = 4
FEATURE [App::DocumentObjectGroupPython] Rh_element001  label="Rh_element : 1"  # scripted group (container) (typed FeaturePython)
  n = 1
  ref = Rh_element
FEATURE [App::DocumentObjectGroupPython] G4_Rh  # scripted group (container) (typed FeaturePython)
  Dunit = g/cm3
  Dvalue = 12.41
  Group = -> [Rh_element001]
  conduct = 2
  density = 1
  expand = 3
  formula = Rh
  name = G4_Rh
  specific = 4
FEATURE [App::DocumentObjectGroupPython] Pd_element001  label="Pd_element : 1"  # scripted group (container) (typed FeaturePython)
  n = 1
  ref = Pd_element
FEATURE [App::DocumentObjectGroupPython] G4_Pd  # scripted group (container) (typed FeaturePython)
  Dunit = g/cm3
  Dvalue = 12.02
  Group = -> [Pd_element001]
  conduct = 2
  density = 1
  expand = 3
  formula = Pd
  name = G4_Pd
  specific = 4
FEATURE [App::DocumentObjectGroupPython] Ag_element006  label="Ag_element : 004"  # scripted group (container) (typed FeaturePython)
  n = 1
  ref = Ag_element
FEATURE [App::DocumentObjectGroupPython] G4_Ag  # scripted group (container) (typed FeaturePython)
  Dunit = g/cm3
  Dvalue = 10.5
  Group = -> [Ag_element006]
  conduct = 2
  density = 1
  expand = 3
  formula = Ag
  name = G4_Ag
  specific = 4
FEATURE [App::DocumentObjectGroupPython] Cd_element003  label="Cd_element : 003"  # scripted group (container) (typed FeaturePython)
  n = 1
  ref = Cd_element
FEATURE [App::DocumentObjectGroupPython] G4_Cd  # scripted group (container) (typed FeaturePython)
  Dunit = g/cm3
  Dvalue = 8.65
  Group = -> [Cd_element003]
  conduct = 2
  density = 1
  expand = 3
  formula = Cd
  name = G4_Cd
  specific = 4
FEATURE [App::DocumentObjectGroupPython] In_element001  label="In_element : 1"  # scripted group (container) (typed FeaturePython)
  n = 1
  ref = In_element
FEATURE [App::DocumentObjectGroupPython] G4_In  # scripted group (container) (typed FeaturePython)
  Dunit = g/cm3
  Dvalue = 7.31
  Group = -> [In_element001]
  conduct = 2
  density = 1
  expand = 3
  formula = In
  name = G4_In
  specific = 4
FEATURE [App::DocumentObjectGroupPython] Sn_element001  label="Sn_element : 1"  # scripted group (container) (typed FeaturePython)
  n = 1
  ref = Sn_element
FEATURE [App::DocumentObjectGroupPython] G4_Sn  # scripted group (container) (typed FeaturePython)
  Dunit = g/cm3
  Dvalue = 7.31
  Group = -> [Sn_element001]
  conduct = 2
  density = 1
  expand = 3
  formula = Sn
  name = G4_Sn
  specific = 4
FEATURE [App::DocumentObjectGroupPython] Sb_element001  label="Sb_element : 1"  # scripted group (container) (typed FeaturePython)
  n = 1
  ref = Sb_element
FEATURE [App::DocumentObjectGroupPython] G4_Sb  # scripted group (container) (typed FeaturePython)
  Dunit = g/cm3
  Dvalue = 6.691
  Group = -> [Sb_element001]
  conduct = 2
  density = 1
  expand = 3
  formula = Sb
  name = G4_Sb
  specific = 4
FEATURE [App::DocumentObjectGroupPython] Te_element002  label="Te_element : 002"  # scripted group (container) (typed FeaturePython)
  n = 1
  ref = Te_element
FEATURE [App::DocumentObjectGroupPython] G4_Te  # scripted group (container) (typed FeaturePython)
  Dunit = g/cm3
  Dvalue = 6.24
  Group = -> [Te_element002]
  conduct = 2
  density = 1
  expand = 3
  formula = Te
  name = G4_Te
  specific = 4
FEATURE [App::DocumentObjectGroupPython] I_element010  label="I_element : 006"  # scripted group (container) (typed FeaturePython)
  n = 1
  ref = I_element
FEATURE [App::DocumentObjectGroupPython] G4_I  # scripted group (container) (typed FeaturePython)
  Dunit = g/cm3
  Dvalue = 4.93
  Group = -> [I_element010]
  conduct = 2
  density = 1
  expand = 3
  formula = I
  name = G4_I
  specific = 4
FEATURE [App::DocumentObjectGroupPython] Xe_element001  label="Xe_element : 1"  # scripted group (container) (typed FeaturePython)
  n = 1
  ref = Xe_element
FEATURE [App::DocumentObjectGroupPython] G4_Xe  # scripted group (container) (typed FeaturePython)
  Dunit = g/cm3
  Dvalue = 0.00548536
  Group = -> [Xe_element001]
  conduct = 2
  density = 1
  expand = 3
  formula = Xe
  name = G4_Xe
  specific = 4
FEATURE [App::DocumentObjectGroupPython] Cs_element003  label="Cs_element : 003"  # scripted group (container) (typed FeaturePython)
  n = 1
  ref = Cs_element
FEATURE [App::DocumentObjectGroupPython] G4_Cs  # scripted group (container) (typed FeaturePython)
  Dunit = g/cm3
  Dvalue = 1.873
  Group = -> [Cs_element003]
  conduct = 2
  density = 1
  expand = 3
  formula = Cs
  name = G4_Cs
  specific = 4
FEATURE [App::DocumentObjectGroupPython] Ba_element003  label="Ba_element : 003"  # scripted group (container) (typed FeaturePython)
  n = 1
  ref = Ba_element
FEATURE [App::DocumentObjectGroupPython] G4_Ba  # scripted group (container) (typed FeaturePython)
  Dunit = g/cm3
  Dvalue = 3.5
  Group = -> [Ba_element003]
  conduct = 2
  density = 1
  expand = 3
  formula = Ba
  name = G4_Ba
  specific = 4
FEATURE [App::DocumentObjectGroupPython] La_element003  label="La_element : 003"  # scripted group (container) (typed FeaturePython)
  n = 1
  ref = La_element
FEATURE [App::DocumentObjectGroupPython] G4_La  # scripted group (container) (typed FeaturePython)
  Dunit = g/cm3
  Dvalue = 6.154
  Group = -> [La_element003]
  conduct = 2
  density = 1
  expand = 3
  formula = La
  name = G4_La
  specific = 4
FEATURE [App::DocumentObjectGroupPython] Ce_element002  label="Ce_element : 1"  # scripted group (container) (typed FeaturePython)
  n = 1
  ref = Ce_element
FEATURE [App::DocumentObjectGroupPython] G4_Ce  # scripted group (container) (typed FeaturePython)
  Dunit = g/cm3
  Dvalue = 6.657
  Group = -> [Ce_element002]
  conduct = 2
  density = 1
  expand = 3
  formula = Ce
  name = G4_Ce
  specific = 4
FEATURE [App::DocumentObjectGroupPython] Pr_element001  label="Pr_element : 1"  # scripted group (container) (typed FeaturePython)
  n = 1
  ref = Pr_element
FEATURE [App::DocumentObjectGroupPython] G4_Pr  # scripted group (container) (typed FeaturePython)
  Dunit = g/cm3
  Dvalue = 6.71
  Group = -> [Pr_element001]
  conduct = 2
  density = 1
  expand = 3
  formula = Pr
  name = G4_Pr
  specific = 4
FEATURE [App::DocumentObjectGroupPython] Nd_element001  label="Nd_element : 1"  # scripted group (container) (typed FeaturePython)
  n = 1
  ref = Nd_element
FEATURE [App::DocumentObjectGroupPython] G4_Nd  # scripted group (container) (typed FeaturePython)
  Dunit = g/cm3
  Dvalue = 6.9
  Group = -> [Nd_element001]
  conduct = 2
  density = 1
  expand = 3
  formula = Nd
  name = G4_Nd
  specific = 4
FEATURE [App::DocumentObjectGroupPython] Pm_element001  label="Pm_element : 1"  # scripted group (container) (typed FeaturePython)
  n = 1
  ref = Pm_element
FEATURE [App::DocumentObjectGroupPython] G4_Pm  # scripted group (container) (typed FeaturePython)
  Dunit = g/cm3
  Dvalue = 7.22
  Group = -> [Pm_element001]
  conduct = 2
  density = 1
  expand = 3
  formula = Pm
  name = G4_Pm
  specific = 4
FEATURE [App::DocumentObjectGroupPython] Sm_element001  label="Sm_element : 1"  # scripted group (container) (typed FeaturePython)
  n = 1
  ref = Sm_element
FEATURE [App::DocumentObjectGroupPython] G4_Sm  # scripted group (container) (typed FeaturePython)
  Dunit = g/cm3
  Dvalue = 7.46
  Group = -> [Sm_element001]
  conduct = 2
  density = 1
  expand = 3
  formula = Sm
  name = G4_Sm
  specific = 4
FEATURE [App::DocumentObjectGroupPython] Eu_element001  label="Eu_element : 1"  # scripted group (container) (typed FeaturePython)
  n = 1
  ref = Eu_element
FEATURE [App::DocumentObjectGroupPython] G4_Eu  # scripted group (container) (typed FeaturePython)
  Dunit = g/cm3
  Dvalue = 5.243
  Group = -> [Eu_element001]
  conduct = 2
  density = 1
  expand = 3
  formula = Eu
  name = G4_Eu
  specific = 4
FEATURE [App::DocumentObjectGroupPython] Gd_element002  label="Gd_element : 1"  # scripted group (container) (typed FeaturePython)
  n = 1
  ref = Gd_element
FEATURE [App::DocumentObjectGroupPython] G4_Gd  # scripted group (container) (typed FeaturePython)
  Dunit = g/cm3
  Dvalue = 7.9004
  Group = -> [Gd_element002]
  conduct = 2
  density = 1
  expand = 3
  formula = Gd
  name = G4_Gd
  specific = 4
FEATURE [App::DocumentObjectGroupPython] Tb_element001  label="Tb_element : 1"  # scripted group (container) (typed FeaturePython)
  n = 1
  ref = Tb_element
FEATURE [App::DocumentObjectGroupPython] G4_Tb  # scripted group (container) (typed FeaturePython)
  Dunit = g/cm3
  Dvalue = 8.229
  Group = -> [Tb_element001]
  conduct = 2
  density = 1
  expand = 3
  formula = Tb
  name = G4_Tb
  specific = 4
FEATURE [App::DocumentObjectGroupPython] Dy_element001  label="Dy_element : 1"  # scripted group (container) (typed FeaturePython)
  n = 1
  ref = Dy_element
FEATURE [App::DocumentObjectGroupPython] G4_Dy  # scripted group (container) (typed FeaturePython)
  Dunit = g/cm3
  Dvalue = 8.55
  Group = -> [Dy_element001]
  conduct = 2
  density = 1
  expand = 3
  formula = Dy
  name = G4_Dy
  specific = 4
FEATURE [App::DocumentObjectGroupPython] Ho_element001  label="Ho_element : 1"  # scripted group (container) (typed FeaturePython)
  n = 1
  ref = Ho_element
FEATURE [App::DocumentObjectGroupPython] G4_Ho  # scripted group (container) (typed FeaturePython)
  Dunit = g/cm3
  Dvalue = 8.795
  Group = -> [Ho_element001]
  conduct = 2
  density = 1
  expand = 3
  formula = Ho
  name = G4_Ho
  specific = 4
FEATURE [App::DocumentObjectGroupPython] Er_element001  label="Er_element : 1"  # scripted group (container) (typed FeaturePython)
  n = 1
  ref = Er_element
FEATURE [App::DocumentObjectGroupPython] G4_Er  # scripted group (container) (typed FeaturePython)
  Dunit = g/cm3
  Dvalue = 9.066
  Group = -> [Er_element001]
  conduct = 2
  density = 1
  expand = 3
  formula = Er
  name = G4_Er
  specific = 4
FEATURE [App::DocumentObjectGroupPython] Tm_element001  label="Tm_element : 1"  # scripted group (container) (typed FeaturePython)
  n = 1
  ref = Tm_element
FEATURE [App::DocumentObjectGroupPython] G4_Tm  # scripted group (container) (typed FeaturePython)
  Dunit = g/cm3
  Dvalue = 9.321
  Group = -> [Tm_element001]
  conduct = 2
  density = 1
  expand = 3
  formula = Tm
  name = G4_Tm
  specific = 4
FEATURE [App::DocumentObjectGroupPython] Yb_element001  label="Yb_element : 1"  # scripted group (container) (typed FeaturePython)
  n = 1
  ref = Yb_element
FEATURE [App::DocumentObjectGroupPython] G4_Yb  # scripted group (container) (typed FeaturePython)
  Dunit = g/cm3
  Dvalue = 6.73
  Group = -> [Yb_element001]
  conduct = 2
  density = 1
  expand = 3
  formula = Yb
  name = G4_Yb
  specific = 4
FEATURE [App::DocumentObjectGroupPython] Lu_element001  label="Lu_element : 1"  # scripted group (container) (typed FeaturePython)
  n = 1
  ref = Lu_element
FEATURE [App::DocumentObjectGroupPython] G4_Lu  # scripted group (container) (typed FeaturePython)
  Dunit = g/cm3
  Dvalue = 9.84
  Group = -> [Lu_element001]
  conduct = 2
  density = 1
  expand = 3
  formula = Lu
  name = G4_Lu
  specific = 4
FEATURE [App::DocumentObjectGroupPython] Hf_element001  label="Hf_element : 1"  # scripted group (container) (typed FeaturePython)
  n = 1
  ref = Hf_element
FEATURE [App::DocumentObjectGroupPython] G4_Hf  # scripted group (container) (typed FeaturePython)
  Dunit = g/cm3
  Dvalue = 13.31
  Group = -> [Hf_element001]
  conduct = 2
  density = 1
  expand = 3
  formula = Hf
  name = G4_Hf
  specific = 4
FEATURE [App::DocumentObjectGroupPython] Ta_element001  label="Ta_element : 1"  # scripted group (container) (typed FeaturePython)
  n = 1
  ref = Ta_element
FEATURE [App::DocumentObjectGroupPython] G4_Ta  # scripted group (container) (typed FeaturePython)
  Dunit = g/cm3
  Dvalue = 16.654
  Group = -> [Ta_element001]
  conduct = 2
  density = 1
  expand = 3
  formula = Ta
  name = G4_Ta
  specific = 4
FEATURE [App::DocumentObjectGroupPython] W_element004  label="W_element : 004"  # scripted group (container) (typed FeaturePython)
  n = 1
  ref = W_element
FEATURE [App::DocumentObjectGroupPython] G4_W  # scripted group (container) (typed FeaturePython)
  Dunit = g/cm3
  Dvalue = 19.3
  Group = -> [W_element004]
  conduct = 2
  density = 1
  expand = 3
  formula = W
  name = G4_W
  specific = 4
FEATURE [App::DocumentObjectGroupPython] Re_element001  label="Re_element : 1"  # scripted group (container) (typed FeaturePython)
  n = 1
  ref = Re_element
FEATURE [App::DocumentObjectGroupPython] G4_Re  # scripted group (container) (typed FeaturePython)
  Dunit = g/cm3
  Dvalue = 21.02
  Group = -> [Re_element001]
  conduct = 2
  density = 1
  expand = 3
  formula = Re
  name = G4_Re
  specific = 4
FEATURE [App::DocumentObjectGroupPython] Os_element001  label="Os_element : 1"  # scripted group (container) (typed FeaturePython)
  n = 1
  ref = Os_element
FEATURE [App::DocumentObjectGroupPython] G4_Os  # scripted group (container) (typed FeaturePython)
  Dunit = g/cm3
  Dvalue = 22.57
  Group = -> [Os_element001]
  conduct = 2
  density = 1
  expand = 3
  formula = Os
  name = G4_Os
  specific = 4
FEATURE [App::DocumentObjectGroupPython] Ir_element001  label="Ir_element : 1"  # scripted group (container) (typed FeaturePython)
  n = 1
  ref = Ir_element
FEATURE [App::DocumentObjectGroupPython] G4_Ir  # scripted group (container) (typed FeaturePython)
  Dunit = g/cm3
  Dvalue = 22.42
  Group = -> [Ir_element001]
  conduct = 2
  density = 1
  expand = 3
  formula = Ir
  name = G4_Ir
  specific = 4
FEATURE [App::DocumentObjectGroupPython] Pt_element001  label="Pt_element : 1"  # scripted group (container) (typed FeaturePython)
  n = 1
  ref = Pt_element
FEATURE [App::DocumentObjectGroupPython] G4_Pt  # scripted group (container) (typed FeaturePython)
  Dunit = g/cm3
  Dvalue = 21.45
  Group = -> [Pt_element001]
  conduct = 2
  density = 1
  expand = 3
  formula = Pt
  name = G4_Pt
  specific = 4
FEATURE [App::DocumentObjectGroupPython] Au_element001  label="Au_element : 1"  # scripted group (container) (typed FeaturePython)
  n = 1
  ref = Au_element
FEATURE [App::DocumentObjectGroupPython] G4_Au  # scripted group (container) (typed FeaturePython)
  Dunit = g/cm3
  Dvalue = 19.32
  Group = -> [Au_element001]
  conduct = 2
  density = 1
  expand = 3
  formula = Au
  name = G4_Au
  specific = 4
FEATURE [App::DocumentObjectGroupPython] Hg_element002  label="Hg_element : 002"  # scripted group (container) (typed FeaturePython)
  n = 1
  ref = Hg_element
FEATURE [App::DocumentObjectGroupPython] G4_Hg  # scripted group (container) (typed FeaturePython)
  Dunit = g/cm3
  Dvalue = 13.546
  Group = -> [Hg_element002]
  conduct = 2
  density = 1
  expand = 3
  formula = Hg
  name = G4_Hg
  specific = 4
FEATURE [App::DocumentObjectGroupPython] Tl_element002  label="Tl_element : 002"  # scripted group (container) (typed FeaturePython)
  n = 1
  ref = Tl_element
FEATURE [App::DocumentObjectGroupPython] G4_Tl  # scripted group (container) (typed FeaturePython)
  Dunit = g/cm3
  Dvalue = 11.72
  Group = -> [Tl_element002]
  conduct = 2
  density = 1
  expand = 3
  formula = Tl
  name = G4_Tl
  specific = 4
FEATURE [App::DocumentObjectGroupPython] Pb_element003  label="Pb_element : 1"  # scripted group (container) (typed FeaturePython)
  n = 1
  ref = Pb_element
FEATURE [App::DocumentObjectGroupPython] G4_Pb  # scripted group (container) (typed FeaturePython)
  Dunit = g/cm3
  Dvalue = 11.35
  Group = -> [Pb_element003]
  conduct = 2
  density = 1
  expand = 3
  formula = Pb
  name = G4_Pb
  specific = 4
FEATURE [App::DocumentObjectGroupPython] Bi_element002  label="Bi_element : 1"  # scripted group (container) (typed FeaturePython)
  n = 1
  ref = Bi_element
FEATURE [App::DocumentObjectGroupPython] G4_Bi  # scripted group (container) (typed FeaturePython)
  Dunit = g/cm3
  Dvalue = 9.747
  Group = -> [Bi_element002]
  conduct = 2
  density = 1
  expand = 3
  formula = Bi
  name = G4_Bi
  specific = 4
FEATURE [App::DocumentObjectGroupPython] Po_element001  label="Po_element : 1"  # scripted group (container) (typed FeaturePython)
  n = 1
  ref = Po_element
FEATURE [App::DocumentObjectGroupPython] G4_Po  # scripted group (container) (typed FeaturePython)
  Dunit = g/cm3
  Dvalue = 9.32
  Group = -> [Po_element001]
  conduct = 2
  density = 1
  expand = 3
  formula = Po
  name = G4_Po
  specific = 4
FEATURE [App::DocumentObjectGroupPython] At_element001  label="At_element : 1"  # scripted group (container) (typed FeaturePython)
  n = 1
  ref = At_element
FEATURE [App::DocumentObjectGroupPython] G4_At  # scripted group (container) (typed FeaturePython)
  Dunit = g/cm3
  Dvalue = 9.32
  Group = -> [At_element001]
  conduct = 2
  density = 1
  expand = 3
  formula = At
  name = G4_At
  specific = 4
FEATURE [App::DocumentObjectGroupPython] Rn_element001  label="Rn_element : 1"  # scripted group (container) (typed FeaturePython)
  n = 1
  ref = Rn_element
FEATURE [App::DocumentObjectGroupPython] G4_Rn  # scripted group (container) (typed FeaturePython)
  Dunit = g/cm3
  Dvalue = 0.00900662
  Group = -> [Rn_element001]
  conduct = 2
  density = 1
  expand = 3
  formula = Rn
  name = G4_Rn
  specific = 4
FEATURE [App::DocumentObjectGroupPython] Fr_element001  label="Fr_element : 1"  # scripted group (container) (typed FeaturePython)
  n = 1
  ref = Fr_element
FEATURE [App::DocumentObjectGroupPython] G4_Fr  # scripted group (container) (typed FeaturePython)
  Dunit = g/cm3
  Dvalue = 1
  Group = -> [Fr_element001]
  conduct = 2
  density = 1
  expand = 3
  formula = Fr
  name = G4_Fr
  specific = 4
FEATURE [App::DocumentObjectGroupPython] Ra_element001  label="Ra_element : 1"  # scripted group (container) (typed FeaturePython)
  n = 1
  ref = Ra_element
FEATURE [App::DocumentObjectGroupPython] G4_Ra  # scripted group (container) (typed FeaturePython)
  Dunit = g/cm3
  Dvalue = 5
  Group = -> [Ra_element001]
  conduct = 2
  density = 1
  expand = 3
  formula = Ra
  name = G4_Ra
  specific = 4
FEATURE [App::DocumentObjectGroupPython] Ac_element001  label="Ac_element : 1"  # scripted group (container) (typed FeaturePython)
  n = 1
  ref = Ac_element
FEATURE [App::DocumentObjectGroupPython] G4_Ac  # scripted group (container) (typed FeaturePython)
  Dunit = g/cm3
  Dvalue = 10.07
  Group = -> [Ac_element001]
  conduct = 2
  density = 1
  expand = 3
  formula = Ac
  name = G4_Ac
  specific = 4
FEATURE [App::DocumentObjectGroupPython] Th_element001  label="Th_element : 1"  # scripted group (container) (typed FeaturePython)
  n = 1
  ref = Th_element
FEATURE [App::DocumentObjectGroupPython] G4_Th  # scripted group (container) (typed FeaturePython)
  Dunit = g/cm3
  Dvalue = 11.72
  Group = -> [Th_element001]
  conduct = 2
  density = 1
  expand = 3
  formula = Th
  name = G4_Th
  specific = 4
FEATURE [App::DocumentObjectGroupPython] Pa_element001  label="Pa_element : 1"  # scripted group (container) (typed FeaturePython)
  n = 1
  ref = Pa_element
FEATURE [App::DocumentObjectGroupPython] G4_Pa  # scripted group (container) (typed FeaturePython)
  Dunit = g/cm3
  Dvalue = 15.37
  Group = -> [Pa_element001]
  conduct = 2
  density = 1
  expand = 3
  formula = Pa
  name = G4_Pa
  specific = 4
FEATURE [App::DocumentObjectGroupPython] U_element004  label="U_element : 004"  # scripted group (container) (typed FeaturePython)
  n = 1
  ref = U_element
FEATURE [App::DocumentObjectGroupPython] G4_U  # scripted group (container) (typed FeaturePython)
  Dunit = g/cm3
  Dvalue = 18.95
  Group = -> [U_element004]
  conduct = 2
  density = 1
  expand = 3
  formula = U
  name = G4_U
  specific = 4
FEATURE [App::DocumentObjectGroupPython] Np_element001  label="Np_element : 1"  # scripted group (container) (typed FeaturePython)
  n = 1
  ref = Np_element
FEATURE [App::DocumentObjectGroupPython] G4_Np  # scripted group (container) (typed FeaturePython)
  Dunit = g/cm3
  Dvalue = 20.25
  Group = -> [Np_element001]
  conduct = 2
  density = 1
  expand = 3
  formula = Np
  name = G4_Np
  specific = 4
FEATURE [App::DocumentObjectGroupPython] Pu_element002  label="Pu_element : 002"  # scripted group (container) (typed FeaturePython)
  n = 1
  ref = Pu_element
FEATURE [App::DocumentObjectGroupPython] G4_Pu  # scripted group (container) (typed FeaturePython)
  Dunit = g/cm3
  Dvalue = 19.84
  Group = -> [Pu_element002]
  conduct = 2
  density = 1
  expand = 3
  formula = Pu
  name = G4_Pu
  specific = 4
FEATURE [App::DocumentObjectGroupPython] Am_element001  label="Am_element : 1"  # scripted group (container) (typed FeaturePython)
  n = 1
  ref = Am_element
FEATURE [App::DocumentObjectGroupPython] G4_Am  # scripted group (container) (typed FeaturePython)
  Dunit = g/cm3
  Dvalue = 13.67
  Group = -> [Am_element001]
  conduct = 2
  density = 1
  expand = 3
  formula = Am
  name = G4_Am
  specific = 4
FEATURE [App::DocumentObjectGroupPython] Cm_element001  label="Cm_element : 1"  # scripted group (container) (typed FeaturePython)
  n = 1
  ref = Cm_element
FEATURE [App::DocumentObjectGroupPython] G4_Cm  # scripted group (container) (typed FeaturePython)
  Dunit = g/cm3
  Dvalue = 13.51
  Group = -> [Cm_element001]
  conduct = 2
  density = 1
  expand = 3
  formula = Cm
  name = G4_Cm
  specific = 4
FEATURE [App::DocumentObjectGroupPython] Bk_element001  label="Bk_element : 1"  # scripted group (container) (typed FeaturePython)
  n = 1
  ref = Bk_element
FEATURE [App::DocumentObjectGroupPython] G4_Bk  # scripted group (container) (typed FeaturePython)
  Dunit = g/cm3
  Dvalue = 14
  Group = -> [Bk_element001]
  conduct = 2
  density = 1
  expand = 3
  formula = Bk
  name = G4_Bk
  specific = 4
FEATURE [App::DocumentObjectGroupPython] Cf_element001  label="Cf_element : 1"  # scripted group (container) (typed FeaturePython)
  n = 1
  ref = Cf_element
FEATURE [App::DocumentObjectGroupPython] G4_Cf  # scripted group (container) (typed FeaturePython)
  Dunit = g/cm3
  Dvalue = 10
  Group = -> [Cf_element001]
  conduct = 2
  density = 1
  expand = 3
  formula = Cf
  name = G4_Cf
  specific = 4
FEATURE [App::DocumentObjectGroupPython] Element  # scripted group (container) (typed FeaturePython)
  Group = -> [G4_H,G4_He,G4_Li,G4_Be,G4_B,G4_C,G4_N,G4_O,G4_F,G4_Ne,G4_Na,G4_Mg,G4_Al,G4_Si,G4_P,G4_S,G4_Cl,G4_Ar,G4_K,G4_Ca,G4_Sc,G4_Ti,G4_V,G4_Cr,G4_Mn,G4_Fe,G4_Co,G4_Ni,G4_Cu,G4_Zn,G4_Ga,G4_Ge,G4_As,G4_Se,G4_Br,G4_Kr,G4_Rb,G4_Sr,G4_Y,G4_Zr,G4_Nb,G4_Mo,G4_Tc,G4_Ru,G4_Rh,G4_Pd,G4_Ag,G4_Cd,G4_In,G4_Sn,G4_Sb,G4_Te,G4_I,G4_Xe,G4_Cs,G4_Ba,G4_La,G4_Ce,G4_Pr,G4_Nd,G4_Pm,G4_Sm,G4_Eu,G4_Gd,G4_Tb,G4_Dy,G4_Ho,G4_Er,+30 more]
FEATURE [App::DocumentObjectGroupPython] H_element114  label="H_element : 063"  # scripted group (container) (typed FeaturePython)
  n = 2
  ref = H_element
FEATURE [App::DocumentObjectGroupPython] G4_lH2  # scripted group (container) (typed FeaturePython)
  Dunit = g/cm3
  Dvalue = 0.0708
  Group = -> [H_element114]
  conduct = 2
  density = 1
  expand = 3
  formula = G4_lH2
  name = G4_lH2
  specific = 4
FEATURE [App::DocumentObjectGroupPython] N_element049  label="N_element : 022"  # scripted group (container) (typed FeaturePython)
  n = 2
  ref = N_element
FEATURE [App::DocumentObjectGroupPython] G4_lN2  # scripted group (container) (typed FeaturePython)
  Dunit = g/cm3
  Dvalue = 0.807
  Group = -> [N_element049]
  conduct = 2
  density = 1
  expand = 3
  formula = G4_lN2
  name = G4_lN2
  specific = 4
FEATURE [App::DocumentObjectGroupPython] O_element106  label="O_element : 060"  # scripted group (container) (typed FeaturePython)
  n = 2
  ref = O_element
FEATURE [App::DocumentObjectGroupPython] G4_lO2  # scripted group (container) (typed FeaturePython)
  Dunit = g/cm3
  Dvalue = 1.141
  Group = -> [O_element106]
  conduct = 2
  density = 1
  expand = 3
  formula = G4_lO2
  name = G4_lO2
  specific = 4
FEATURE [App::DocumentObjectGroupPython] Ar  label="Ar : 1"  # scripted group (container) (typed FeaturePython)
  n = 1
  ref = Ar
FEATURE [App::DocumentObjectGroupPython] G4_lAr  # scripted group (container) (typed FeaturePython)
  Dunit = g/cm3
  Dvalue = 1.396
  Group = -> [Ar]
  conduct = 2
  density = 1
  expand = 3
  formula = G4_lAr
  name = G4_lAr
  specific = 4
FEATURE [App::DocumentObjectGroupPython] Br  label="Br : 1"  # scripted group (container) (typed FeaturePython)
  n = 1
  ref = Br
FEATURE [App::DocumentObjectGroupPython] G4_lBr  # scripted group (container) (typed FeaturePython)
  Dunit = g/cm3
  Dvalue = 3.1028
  Group = -> [Br]
  conduct = 2
  density = 1
  expand = 3
  formula = G4_lBr
  name = G4_lBr
  specific = 4
FEATURE [App::DocumentObjectGroupPython] Kr  label="Kr : 1"  # scripted group (container) (typed FeaturePython)
  n = 1
  ref = Kr
FEATURE [App::DocumentObjectGroupPython] G4_lKr  # scripted group (container) (typed FeaturePython)
  Dunit = g/cm3
  Dvalue = 2.418
  Group = -> [Kr]
  conduct = 2
  density = 1
  expand = 3
  formula = G4_lKr
  name = G4_lKr
  specific = 4
FEATURE [App::DocumentObjectGroupPython] Xe  label="Xe : 1"  # scripted group (container) (typed FeaturePython)
  n = 1
  ref = Xe
FEATURE [App::DocumentObjectGroupPython] G4_lXe  # scripted group (container) (typed FeaturePython)
  Dunit = g/cm3
  Dvalue = 2.953
  Group = -> [Xe]
  conduct = 2
  density = 1
  expand = 3
  formula = G4_lXe
  name = G4_lXe
  specific = 4
FEATURE [App::DocumentObjectGroupPython] O_element107  label="O_element : 061"  # scripted group (container) (typed FeaturePython)
  n = 4
  ref = O_element
FEATURE [App::DocumentObjectGroupPython] Pb_element004  label="Pb_element : 002"  # scripted group (container) (typed FeaturePython)
  n = 1
  ref = Pb_element
FEATURE [App::DocumentObjectGroupPython] W_element005  label="W_element : 005"  # scripted group (container) (typed FeaturePython)
  n = 1
  ref = W_element
FEATURE [App::DocumentObjectGroupPython] G4_PbWO4  # scripted group (container) (typed FeaturePython)
  Dunit = g/cm3
  Dvalue = 8.28
  Group = -> [O_element107,Pb_element004,W_element005]
  conduct = 2
  density = 1
  expand = 3
  formula = G4_PbWO4
  name = G4_PbWO4
  specific = 4
FEATURE [App::DocumentObjectGroupPython] alactic  label="alactic : 1"  # scripted group (container) (typed FeaturePython)
  n = 1
  ref = alactic
FEATURE [App::DocumentObjectGroupPython] G4_Galactic  # scripted group (container) (typed FeaturePython)
  Dunit = g/cm3
  Dvalue = 0
  Group = -> [alactic]
  conduct = 2
  density = 1
  expand = 3
  formula = G4_Galactic
  name = G4_Galactic
  specific = 4
FEATURE [App::DocumentObjectGroupPython] RAPHITE_POROUS  label="RAPHITE_POROUS : 1"  # scripted group (container) (typed FeaturePython)
  n = 1
  ref = RAPHITE_POROUS
FEATURE [App::DocumentObjectGroupPython] G4_GRAPHITE_POROUS  # scripted group (container) (typed FeaturePython)
  Dunit = g/cm3
  Dvalue = 1.7
  Group = -> [RAPHITE_POROUS]
  conduct = 2
  density = 1
  expand = 3
  formula = G4_GRAPHITE_POROUS
  name = G4_GRAPHITE_POROUS
  specific = 4
FEATURE [App::DocumentObjectGroupPython] H_element115  label="H_element : 0.150"  # scripted group (container) (typed FeaturePython)
  n = 0.080538
FEATURE [App::DocumentObjectGroupPython] C_element125  label="C_element : 0.600"  # scripted group (container) (typed FeaturePython)
  n = 0.599848
FEATURE [App::DocumentObjectGroupPython] O_element108  label="O_element : 0.320"  # scripted group (container) (typed FeaturePython)
  n = 0.319614
FEATURE [App::DocumentObjectGroupPython] G4_LUCITE  # scripted group (container) (typed FeaturePython)
  Dunit = g/cm3
  Dvalue = 1.19
  Group = -> [H_element115,C_element125,O_element108]
  conduct = 2
  density = 1
  expand = 3
  formula = G4_LUCITE
  name = G4_LUCITE
  specific = 4
FEATURE [App::DocumentObjectGroupPython] Cu_element002  label="Cu_element : 62"  # scripted group (container) (typed FeaturePython)
  n = 62
  ref = Cu_element
FEATURE [App::DocumentObjectGroupPython] Zn_element002  label="Zn_element : 35"  # scripted group (container) (typed FeaturePython)
  n = 35
  ref = Zn_element
FEATURE [App::DocumentObjectGroupPython] Pb_element005  label="Pb_element : 3"  # scripted group (container) (typed FeaturePython)
  n = 3
  ref = Pb_element
FEATURE [App::DocumentObjectGroupPython] G4_BRASS  # scripted group (container) (typed FeaturePython)
  Dunit = g/cm3
  Dvalue = 8.52
  Group = -> [Cu_element002,Zn_element002,Pb_element005]
  conduct = 2
  density = 1
  expand = 3
  formula = G4_BRASS
  name = G4_BRASS
  specific = 4
FEATURE [App::DocumentObjectGroupPython] Cu_element003  label="Cu_element : 89"  # scripted group (container) (typed FeaturePython)
  n = 89
  ref = Cu_element
FEATURE [App::DocumentObjectGroupPython] Zn_element003  label="Zn_element : 9"  # scripted group (container) (typed FeaturePython)
  n = 9
  ref = Zn_element
FEATURE [App::DocumentObjectGroupPython] Pb_element006  label="Pb_element : 2"  # scripted group (container) (typed FeaturePython)
  n = 2
  ref = Pb_element
FEATURE [App::DocumentObjectGroupPython] G4_BRONZE  # scripted group (container) (typed FeaturePython)
  Dunit = g/cm3
  Dvalue = 8.82
  Group = -> [Cu_element003,Zn_element003,Pb_element006]
  conduct = 2
  density = 1
  expand = 3
  formula = G4_BRONZE
  name = G4_BRONZE
  specific = 4
FEATURE [App::DocumentObjectGroupPython] Fe_element008  label="Fe_element : 74"  # scripted group (container) (typed FeaturePython)
  n = 74
  ref = Fe_element
FEATURE [App::DocumentObjectGroupPython] Cr_element002  label="Cr_element : 18"  # scripted group (container) (typed FeaturePython)
  n = 18
  ref = Cr_element
FEATURE [App::DocumentObjectGroupPython] Ni_element002  label="Ni_element : 8"  # scripted group (container) (typed FeaturePython)
  n = 8
  ref = Ni_element
FEATURE [App::DocumentObjectGroupPython] G4_STAINLESS_STEEL  label="G4_STAINLESS-STEEL"  # scripted group (container) (typed FeaturePython)
  Dunit = g/cm3
  Dvalue = 8
  Group = -> [Fe_element008,Cr_element002,Ni_element002]
  conduct = 2
  density = 1
  expand = 3
  formula = G4_STAINLESS-STEEL
  name = G4_STAINLESS-STEEL
  specific = 4
FEATURE [App::DocumentObjectGroupPython] H_element116  label="H_element : 064"  # scripted group (container) (typed FeaturePython)
  n = 18
  ref = H_element
FEATURE [App::DocumentObjectGroupPython] C_element126  label="C_element : 071"  # scripted group (container) (typed FeaturePython)
  n = 12
  ref = C_element
FEATURE [App::DocumentObjectGroupPython] O_element109  label="O_element : 062"  # scripted group (container) (typed FeaturePython)
  n = 7
  ref = O_element
FEATURE [App::DocumentObjectGroupPython] G4_CR39  # scripted group (container) (typed FeaturePython)
  Dunit = g/cm3
  Dvalue = 1.32
  Group = -> [H_element116,C_element126,O_element109]
  conduct = 2
  density = 1
  expand = 3
  formula = G4_CR39
  name = G4_CR39
  specific = 4
FEATURE [App::DocumentObjectGroupPython] H_element117  label="H_element : 38"  # scripted group (container) (typed FeaturePython)
  n = 38
  ref = H_element
FEATURE [App::DocumentObjectGroupPython] C_element127  label="C_element : 072"  # scripted group (container) (typed FeaturePython)
  n = 18
  ref = C_element
FEATURE [App::DocumentObjectGroupPython] O_element110  label="O_element : 063"  # scripted group (container) (typed FeaturePython)
  n = 1
  ref = O_element
FEATURE [App::DocumentObjectGroupPython] G4_OCTADECANOL  # scripted group (container) (typed FeaturePython)
  Dunit = g/cm3
  Dvalue = 0.812
  Group = -> [H_element117,C_element127,O_element110]
  conduct = 2
  density = 1
  expand = 3
  formula = G4_OCTADECANOL
  name = G4_OCTADECANOL
  specific = 4
FEATURE [App::DocumentObjectGroupPython] HEP  # scripted group (container) (typed FeaturePython)
  Group = -> [G4_lH2,G4_lN2,G4_lO2,G4_lAr,G4_lBr,G4_lKr,G4_lXe,G4_PbWO4,G4_Galactic,G4_GRAPHITE_POROUS,G4_LUCITE,G4_BRASS,G4_BRONZE,G4_STAINLESS_STEEL,G4_CR39,G4_OCTADECANOL]
FEATURE [App::DocumentObjectGroupPython] C_element128  label="C_element : 073"  # scripted group (container) (typed FeaturePython)
  n = 14
  ref = C_element
FEATURE [App::DocumentObjectGroupPython] H_element118  label="H_element : 065"  # scripted group (container) (typed FeaturePython)
  n = 10
  ref = H_element
FEATURE [App::DocumentObjectGroupPython] O_element111  label="O_element : 064"  # scripted group (container) (typed FeaturePython)
  n = 2
  ref = O_element
FEATURE [App::DocumentObjectGroupPython] N_element050  label="N_element : 023"  # scripted group (container) (typed FeaturePython)
  n = 2
  ref = N_element
FEATURE [App::DocumentObjectGroupPython] G4_KEVLAR  # scripted group (container) (typed FeaturePython)
  Dunit = g/cm3
  Dvalue = 1.44
  Group = -> [C_element128,H_element118,O_element111,N_element050]
  conduct = 2
  density = 1
  expand = 3
  formula = G4_KEVLAR
  name = G4_KEVLAR
  specific = 4
FEATURE [App::DocumentObjectGroupPython] C_element129  label="C_element : 074"  # scripted group (container) (typed FeaturePython)
  n = 10
  ref = C_element
FEATURE [App::DocumentObjectGroupPython] H_element119  label="H_element : 066"  # scripted group (container) (typed FeaturePython)
  n = 8
  ref = H_element
FEATURE [App::DocumentObjectGroupPython] O_element112  label="O_element : 065"  # scripted group (container) (typed FeaturePython)
  n = 4
  ref = O_element
FEATURE [App::DocumentObjectGroupPython] G4_DACRON  # scripted group (container) (typed FeaturePython)
  Dunit = g/cm3
  Dvalue = 1.4
  Group = -> [C_element129,H_element119,O_element112]
  conduct = 2
  density = 1
  expand = 3
  formula = G4_DACRON
  name = G4_DACRON
  specific = 4
FEATURE [App::DocumentObjectGroupPython] C_element130  label="C_element : 075"  # scripted group (container) (typed FeaturePython)
  n = 4
  ref = C_element
FEATURE [App::DocumentObjectGroupPython] H_element120  label="H_element : 067"  # scripted group (container) (typed FeaturePython)
  n = 5
  ref = H_element
FEATURE [App::DocumentObjectGroupPython] Cl_element030  label="Cl_element : 016"  # scripted group (container) (typed FeaturePython)
  n = 1
  ref = Cl_element
FEATURE [App::DocumentObjectGroupPython] G4_NEOPRENE  # scripted group (container) (typed FeaturePython)
  Dunit = g/cm3
  Dvalue = 1.23
  Group = -> [C_element130,H_element120,Cl_element030]
  conduct = 2
  density = 1
  expand = 3
  formula = G4_NEOPRENE
  name = G4_NEOPRENE
  specific = 4
FEATURE [App::DocumentObjectGroupPython] Space  # scripted group (container) (typed FeaturePython)
  Group = -> [G4_KEVLAR,G4_DACRON,G4_NEOPRENE]
FEATURE [App::DocumentObjectGroupPython] H_element121  label="H_element : 068"  # scripted group (container) (typed FeaturePython)
  n = 5
  ref = H_element
FEATURE [App::DocumentObjectGroupPython] C_element131  label="C_element : 076"  # scripted group (container) (typed FeaturePython)
  n = 4
  ref = C_element
FEATURE [App::DocumentObjectGroupPython] N_element051  label="N_element : 3"  # scripted group (container) (typed FeaturePython)
  n = 3
  ref = N_element
FEATURE [App::DocumentObjectGroupPython] O_element113  label="O_element : 066"  # scripted group (container) (typed FeaturePython)
  n = 1
  ref = O_element
FEATURE [App::DocumentObjectGroupPython] G4_CYTOSINE  # scripted group (container) (typed FeaturePython)
  Dunit = g/cm3
  Dvalue = 1.55
  Group = -> [H_element121,C_element131,N_element051,O_element113]
  conduct = 2
  density = 1
  expand = 3
  formula = G4_CYTOSINE
  name = G4_CYTOSINE
  specific = 4
FEATURE [App::DocumentObjectGroupPython] H_element122  label="H_element : 069"  # scripted group (container) (typed FeaturePython)
  n = 6
  ref = H_element
FEATURE [App::DocumentObjectGroupPython] C_element132  label="C_element : 077"  # scripted group (container) (typed FeaturePython)
  n = 5
  ref = C_element
FEATURE [App::DocumentObjectGroupPython] N_element052  label="N_element : 024"  # scripted group (container) (typed FeaturePython)
  n = 2
  ref = N_element
FEATURE [App::DocumentObjectGroupPython] O_element114  label="O_element : 067"  # scripted group (container) (typed FeaturePython)
  n = 2
  ref = O_element
FEATURE [App::DocumentObjectGroupPython] G4_THYMINE  # scripted group (container) (typed FeaturePython)
  Dunit = g/cm3
  Dvalue = 1.23
  Group = -> [H_element122,C_element132,N_element052,O_element114]
  conduct = 2
  density = 1
  expand = 3
  formula = G4_THYMINE
  name = G4_THYMINE
  specific = 4
FEATURE [App::DocumentObjectGroupPython] H_element123  label="H_element : 070"  # scripted group (container) (typed FeaturePython)
  n = 4
  ref = H_element
FEATURE [App::DocumentObjectGroupPython] C_element133  label="C_element : 078"  # scripted group (container) (typed FeaturePython)
  n = 4
  ref = C_element
FEATURE [App::DocumentObjectGroupPython] N_element053  label="N_element : 025"  # scripted group (container) (typed FeaturePython)
  n = 2
  ref = N_element
FEATURE [App::DocumentObjectGroupPython] O_element115  label="O_element : 068"  # scripted group (container) (typed FeaturePython)
  n = 2
  ref = O_element
FEATURE [App::DocumentObjectGroupPython] G4_URACIL  # scripted group (container) (typed FeaturePython)
  Dunit = g/cm3
  Dvalue = 1.32
  Group = -> [H_element123,C_element133,N_element053,O_element115]
  conduct = 2
  density = 1
  expand = 3
  formula = G4_URACIL
  name = G4_URACIL
  specific = 4
FEATURE [App::DocumentObjectGroupPython] H_element124  label="H_element : 071"  # scripted group (container) (typed FeaturePython)
  n = 4
  ref = H_element
FEATURE [App::DocumentObjectGroupPython] C_element134  label="C_element : 079"  # scripted group (container) (typed FeaturePython)
  n = 5
  ref = C_element
FEATURE [App::DocumentObjectGroupPython] N_element054  label="N_element : 026"  # scripted group (container) (typed FeaturePython)
  n = 5
  ref = N_element
FEATURE [App::DocumentObjectGroupPython] G4_DNA_ADENINE  # scripted group (container) (typed FeaturePython)
  Dunit = g/cm3
  Dvalue = 1
  Group = -> [H_element124,C_element134,N_element054]
  conduct = 2
  density = 1
  expand = 3
  formula = G4_DNA_ADENINE
  name = G4_DNA_ADENINE
  specific = 4
FEATURE [App::DocumentObjectGroupPython] H_element125  label="H_element : 072"  # scripted group (container) (typed FeaturePython)
  n = 4
  ref = H_element
FEATURE [App::DocumentObjectGroupPython] C_element135  label="C_element : 080"  # scripted group (container) (typed FeaturePython)
  n = 5
  ref = C_element
FEATURE [App::DocumentObjectGroupPython] N_element055  label="N_element : 027"  # scripted group (container) (typed FeaturePython)
  n = 5
  ref = N_element
FEATURE [App::DocumentObjectGroupPython] O_element116  label="O_element : 069"  # scripted group (container) (typed FeaturePython)
  n = 1
  ref = O_element
FEATURE [App::DocumentObjectGroupPython] G4_DNA_GUANINE  # scripted group (container) (typed FeaturePython)
  Dunit = g/cm3
  Dvalue = 1
  Group = -> [H_element125,C_element135,N_element055,O_element116]
  conduct = 2
  density = 1
  expand = 3
  formula = G4_DNA_GUANINE
  name = G4_DNA_GUANINE
  specific = 4
FEATURE [App::DocumentObjectGroupPython] H_element126  label="H_element : 073"  # scripted group (container) (typed FeaturePython)
  n = 4
  ref = H_element
FEATURE [App::DocumentObjectGroupPython] C_element136  label="C_element : 081"  # scripted group (container) (typed FeaturePython)
  n = 4
  ref = C_element
FEATURE [App::DocumentObjectGroupPython] N_element056  label="N_element : 028"  # scripted group (container) (typed FeaturePython)
  n = 3
  ref = N_element
FEATURE [App::DocumentObjectGroupPython] O_element117  label="O_element : 070"  # scripted group (container) (typed FeaturePython)
  n = 1
  ref = O_element
FEATURE [App::DocumentObjectGroupPython] G4_DNA_CYTOSINE  # scripted group (container) (typed FeaturePython)
  Dunit = g/cm3
  Dvalue = 1
  Group = -> [H_element126,C_element136,N_element056,O_element117]
  conduct = 2
  density = 1
  expand = 3
  formula = G4_DNA_CYTOSINE
  name = G4_DNA_CYTOSINE
  specific = 4
FEATURE [App::DocumentObjectGroupPython] H_element127  label="H_element : 074"  # scripted group (container) (typed FeaturePython)
  n = 5
  ref = H_element
FEATURE [App::DocumentObjectGroupPython] C_element137  label="C_element : 082"  # scripted group (container) (typed FeaturePython)
  n = 5
  ref = C_element
FEATURE [App::DocumentObjectGroupPython] N_element057  label="N_element : 029"  # scripted group (container) (typed FeaturePython)
  n = 2
  ref = N_element
FEATURE [App::DocumentObjectGroupPython] O_element118  label="O_element : 071"  # scripted group (container) (typed FeaturePython)
  n = 2
  ref = O_element
FEATURE [App::DocumentObjectGroupPython] G4_DNA_THYMINE  # scripted group (container) (typed FeaturePython)
  Dunit = g/cm3
  Dvalue = 1
  Group = -> [H_element127,C_element137,N_element057,O_element118]
  conduct = 2
  density = 1
  expand = 3
  formula = G4_DNA_THYMINE
  name = G4_DNA_THYMINE
  specific = 4
FEATURE [App::DocumentObjectGroupPython] H_element128  label="H_element : 075"  # scripted group (container) (typed FeaturePython)
  n = 3
  ref = H_element
FEATURE [App::DocumentObjectGroupPython] C_element138  label="C_element : 083"  # scripted group (container) (typed FeaturePython)
  n = 4
  ref = C_element
FEATURE [App::DocumentObjectGroupPython] N_element058  label="N_element : 030"  # scripted group (container) (typed FeaturePython)
  n = 2
  ref = N_element
FEATURE [App::DocumentObjectGroupPython] O_element119  label="O_element : 072"  # scripted group (container) (typed FeaturePython)
  n = 2
  ref = O_element
FEATURE [App::DocumentObjectGroupPython] G4_DNA_URACIL  # scripted group (container) (typed FeaturePython)
  Dunit = g/cm3
  Dvalue = 1
  Group = -> [H_element128,C_element138,N_element058,O_element119]
  conduct = 2
  density = 1
  expand = 3
  formula = G4_DNA_URACIL
  name = G4_DNA_URACIL
  specific = 4
FEATURE [App::DocumentObjectGroupPython] H_element129  label="H_element : 076"  # scripted group (container) (typed FeaturePython)
  n = 10
  ref = H_element
FEATURE [App::DocumentObjectGroupPython] C_element139  label="C_element : 084"  # scripted group (container) (typed FeaturePython)
  n = 10
  ref = C_element
FEATURE [App::DocumentObjectGroupPython] N_element059  label="N_element : 031"  # scripted group (container) (typed FeaturePython)
  n = 5
  ref = N_element
FEATURE [App::DocumentObjectGroupPython] O_element120  label="O_element : 073"  # scripted group (container) (typed FeaturePython)
  n = 4
  ref = O_element
FEATURE [App::DocumentObjectGroupPython] G4_DNA_ADENOSINE  # scripted group (container) (typed FeaturePython)
  Dunit = g/cm3
  Dvalue = 1
  Group = -> [H_element129,C_element139,N_element059,O_element120]
  conduct = 2
  density = 1
  expand = 3
  formula = G4_DNA_ADENOSINE
  name = G4_DNA_ADENOSINE
  specific = 4
FEATURE [App::DocumentObjectGroupPython] H_element130  label="H_element : 077"  # scripted group (container) (typed FeaturePython)
  n = 10
  ref = H_element
FEATURE [App::DocumentObjectGroupPython] C_element140  label="C_element : 085"  # scripted group (container) (typed FeaturePython)
  n = 10
  ref = C_element
FEATURE [App::DocumentObjectGroupPython] N_element060  label="N_element : 032"  # scripted group (container) (typed FeaturePython)
  n = 5
  ref = N_element
FEATURE [App::DocumentObjectGroupPython] O_element121  label="O_element : 074"  # scripted group (container) (typed FeaturePython)
  n = 5
  ref = O_element
FEATURE [App::DocumentObjectGroupPython] G4_DNA_GUANOSINE  # scripted group (container) (typed FeaturePython)
  Dunit = g/cm3
  Dvalue = 1
  Group = -> [H_element130,C_element140,N_element060,O_element121]
  conduct = 2
  density = 1
  expand = 3
  formula = G4_DNA_GUANOSINE
  name = G4_DNA_GUANOSINE
  specific = 4
FEATURE [App::DocumentObjectGroupPython] H_element131  label="H_element : 078"  # scripted group (container) (typed FeaturePython)
  n = 10
  ref = H_element
FEATURE [App::DocumentObjectGroupPython] C_element141  label="C_element : 086"  # scripted group (container) (typed FeaturePython)
  n = 9
  ref = C_element
FEATURE [App::DocumentObjectGroupPython] N_element061  label="N_element : 033"  # scripted group (container) (typed FeaturePython)
  n = 3
  ref = N_element
FEATURE [App::DocumentObjectGroupPython] O_element122  label="O_element : 075"  # scripted group (container) (typed FeaturePython)
  n = 5
  ref = O_element
FEATURE [App::DocumentObjectGroupPython] G4_DNA_CYTIDINE  # scripted group (container) (typed FeaturePython)
  Dunit = g/cm3
  Dvalue = 1
  Group = -> [H_element131,C_element141,N_element061,O_element122]
  conduct = 2
  density = 1
  expand = 3
  formula = G4_DNA_CYTIDINE
  name = G4_DNA_CYTIDINE
  specific = 4
FEATURE [App::DocumentObjectGroupPython] H_element132  label="H_element : 079"  # scripted group (container) (typed FeaturePython)
  n = 9
  ref = H_element
FEATURE [App::DocumentObjectGroupPython] C_element142  label="C_element : 087"  # scripted group (container) (typed FeaturePython)
  n = 9
  ref = C_element
FEATURE [App::DocumentObjectGroupPython] N_element062  label="N_element : 034"  # scripted group (container) (typed FeaturePython)
  n = 2
  ref = N_element
FEATURE [App::DocumentObjectGroupPython] O_element123  label="O_element : 076"  # scripted group (container) (typed FeaturePython)
  n = 6
  ref = O_element
FEATURE [App::DocumentObjectGroupPython] G4_DNA_URIDINE  # scripted group (container) (typed FeaturePython)
  Dunit = g/cm3
  Dvalue = 1
  Group = -> [H_element132,C_element142,N_element062,O_element123]
  conduct = 2
  density = 1
  expand = 3
  formula = G4_DNA_URIDINE
  name = G4_DNA_URIDINE
  specific = 4
FEATURE [App::DocumentObjectGroupPython] H_element133  label="H_element : 080"  # scripted group (container) (typed FeaturePython)
  n = 11
  ref = H_element
FEATURE [App::DocumentObjectGroupPython] C_element143  label="C_element : 088"  # scripted group (container) (typed FeaturePython)
  n = 10
  ref = C_element
FEATURE [App::DocumentObjectGroupPython] N_element063  label="N_element : 035"  # scripted group (container) (typed FeaturePython)
  n = 2
  ref = N_element
FEATURE [App::DocumentObjectGroupPython] O_element124  label="O_element : 077"  # scripted group (container) (typed FeaturePython)
  n = 6
  ref = O_element
FEATURE [App::DocumentObjectGroupPython] G4_DNA_METHYLURIDINE  # scripted group (container) (typed FeaturePython)
  Dunit = g/cm3
  Dvalue = 1
  Group = -> [H_element133,C_element143,N_element063,O_element124]
  conduct = 2
  density = 1
  expand = 3
  formula = G4_DNA_METHYLURIDINE
  name = G4_DNA_METHYLURIDINE
  specific = 4
FEATURE [App::DocumentObjectGroupPython] P_element014  label="P_element : 003"  # scripted group (container) (typed FeaturePython)
  n = 1
  ref = P_element
FEATURE [App::DocumentObjectGroupPython] O_element125  label="O_element : 078"  # scripted group (container) (typed FeaturePython)
  n = 3
  ref = O_element
FEATURE [App::DocumentObjectGroupPython] G4_DNA_MONOPHOSPHATE  # scripted group (container) (typed FeaturePython)
  Dunit = g/cm3
  Dvalue = 1
  Group = -> [P_element014,O_element125]
  conduct = 2
  density = 1
  expand = 3
  formula = G4_DNA_MONOPHOSPHATE
  name = G4_DNA_MONOPHOSPHATE
  specific = 4
FEATURE [App::DocumentObjectGroupPython] H_element134  label="H_element : 081"  # scripted group (container) (typed FeaturePython)
  n = 10
  ref = H_element
FEATURE [App::DocumentObjectGroupPython] C_element144  label="C_element : 089"  # scripted group (container) (typed FeaturePython)
  n = 10
  ref = C_element
FEATURE [App::DocumentObjectGroupPython] N_element064  label="N_element : 036"  # scripted group (container) (typed FeaturePython)
  n = 5
  ref = N_element
FEATURE [App::DocumentObjectGroupPython] O_element126  label="O_element : 079"  # scripted group (container) (typed FeaturePython)
  n = 7
  ref = O_element
FEATURE [App::DocumentObjectGroupPython] P_element015  label="P_element : 004"  # scripted group (container) (typed FeaturePython)
  n = 1
  ref = P_element
FEATURE [App::DocumentObjectGroupPython] G4_DNA_A  # scripted group (container) (typed FeaturePython)
  Dunit = g/cm3
  Dvalue = 1
  Group = -> [H_element134,C_element144,N_element064,O_element126,P_element015]
  conduct = 2
  density = 1
  expand = 3
  formula = G4_DNA_A
  name = G4_DNA_A
  specific = 4
FEATURE [App::DocumentObjectGroupPython] H_element135  label="H_element : 082"  # scripted group (container) (typed FeaturePython)
  n = 10
  ref = H_element
FEATURE [App::DocumentObjectGroupPython] C_element145  label="C_element : 090"  # scripted group (container) (typed FeaturePython)
  n = 10
  ref = C_element
FEATURE [App::DocumentObjectGroupPython] N_element065  label="N_element : 037"  # scripted group (container) (typed FeaturePython)
  n = 5
  ref = N_element
FEATURE [App::DocumentObjectGroupPython] O_element127  label="O_element : 8"  # scripted group (container) (typed FeaturePython)
  n = 8
  ref = O_element
FEATURE [App::DocumentObjectGroupPython] P_element016  label="P_element : 005"  # scripted group (container) (typed FeaturePython)
  n = 1
  ref = P_element
FEATURE [App::DocumentObjectGroupPython] G4_DNA_G  # scripted group (container) (typed FeaturePython)
  Dunit = g/cm3
  Dvalue = 1
  Group = -> [H_element135,C_element145,N_element065,O_element127,P_element016]
  conduct = 2
  density = 1
  expand = 3
  formula = G4_DNA_G
  name = G4_DNA_G
  specific = 4
FEATURE [App::DocumentObjectGroupPython] H_element136  label="H_element : 083"  # scripted group (container) (typed FeaturePython)
  n = 10
  ref = H_element
FEATURE [App::DocumentObjectGroupPython] C_element146  label="C_element : 091"  # scripted group (container) (typed FeaturePython)
  n = 9
  ref = C_element
FEATURE [App::DocumentObjectGroupPython] N_element066  label="N_element : 038"  # scripted group (container) (typed FeaturePython)
  n = 3
  ref = N_element
FEATURE [App::DocumentObjectGroupPython] O_element128  label="O_element : 080"  # scripted group (container) (typed FeaturePython)
  n = 8
  ref = O_element
FEATURE [App::DocumentObjectGroupPython] P_element017  label="P_element : 006"  # scripted group (container) (typed FeaturePython)
  n = 1
  ref = P_element
FEATURE [App::DocumentObjectGroupPython] G4_DNA_C  # scripted group (container) (typed FeaturePython)
  Dunit = g/cm3
  Dvalue = 1
  Group = -> [H_element136,C_element146,N_element066,O_element128,P_element017]
  conduct = 2
  density = 1
  expand = 3
  formula = G4_DNA_C
  name = G4_DNA_C
  specific = 4
FEATURE [App::DocumentObjectGroupPython] H_element137  label="H_element : 084"  # scripted group (container) (typed FeaturePython)
  n = 9
  ref = H_element
FEATURE [App::DocumentObjectGroupPython] C_element147  label="C_element : 092"  # scripted group (container) (typed FeaturePython)
  n = 9
  ref = C_element
FEATURE [App::DocumentObjectGroupPython] N_element067  label="N_element : 039"  # scripted group (container) (typed FeaturePython)
  n = 2
  ref = N_element
FEATURE [App::DocumentObjectGroupPython] O_element129  label="O_element : 9"  # scripted group (container) (typed FeaturePython)
  n = 9
  ref = O_element
FEATURE [App::DocumentObjectGroupPython] P_element018  label="P_element : 007"  # scripted group (container) (typed FeaturePython)
  n = 1
  ref = P_element
FEATURE [App::DocumentObjectGroupPython] G4_DNA_U  # scripted group (container) (typed FeaturePython)
  Dunit = g/cm3
  Dvalue = 1
  Group = -> [H_element137,C_element147,N_element067,O_element129,P_element018]
  conduct = 2
  density = 1
  expand = 3
  formula = G4_DNA_U
  name = G4_DNA_U
  specific = 4
FEATURE [App::DocumentObjectGroupPython] H_element138  label="H_element : 085"  # scripted group (container) (typed FeaturePython)
  n = 11
  ref = H_element
FEATURE [App::DocumentObjectGroupPython] C_element148  label="C_element : 093"  # scripted group (container) (typed FeaturePython)
  n = 10
  ref = C_element
FEATURE [App::DocumentObjectGroupPython] N_element068  label="N_element : 040"  # scripted group (container) (typed FeaturePython)
  n = 2
  ref = N_element
FEATURE [App::DocumentObjectGroupPython] O_element130  label="O_element : 081"  # scripted group (container) (typed FeaturePython)
  n = 9
  ref = O_element
FEATURE [App::DocumentObjectGroupPython] P_element019  label="P_element : 008"  # scripted group (container) (typed FeaturePython)
  n = 1
  ref = P_element
FEATURE [App::DocumentObjectGroupPython] G4_DNA_MU  # scripted group (container) (typed FeaturePython)
  Dunit = g/cm3
  Dvalue = 1
  Group = -> [H_element138,C_element148,N_element068,O_element130,P_element019]
  conduct = 2
  density = 1
  expand = 3
  formula = G4_DNA_MU
  name = G4_DNA_MU
  specific = 4
FEATURE [App::DocumentObjectGroupPython] BioChemical  # scripted group (container) (typed FeaturePython)
  Group = -> [G4_CYTOSINE,G4_THYMINE,G4_URACIL,G4_DNA_ADENINE,G4_DNA_GUANINE,G4_DNA_CYTOSINE,G4_DNA_THYMINE,G4_DNA_URACIL,G4_DNA_ADENOSINE,G4_DNA_GUANOSINE,G4_DNA_CYTIDINE,G4_DNA_URIDINE,G4_DNA_METHYLURIDINE,G4_DNA_MONOPHOSPHATE,G4_DNA_A,G4_DNA_G,G4_DNA_C,G4_DNA_U,G4_DNA_MU]
FEATURE [App::DocumentObjectGroupPython] G4Materials  # scripted group (container) (typed FeaturePython)
  Group = -> [NIST,Element,HEP,Space,BioChemical]
  version = 1
FEATURE [App::DocumentObjectGroupPython] Geant4  # scripted group (container) (typed FeaturePython)
  Group = -> [G4Isotopes,G4Elements,G4Materials]
FEATURE [Part::FeaturePython] GDMLBox_WorldBox  # WARN: FeaturePython — macro-defined, semantics opaque (R4)
  lunit = 2
  material = 8
  x = 114.01
  y = 147.706
  z = 147.706
FEATURE [App::DocumentObjectGroupPython] G4_Pyrex_Glass001  label="G4_Pyrex_Glass : 1.000"  # scripted group (container) (typed FeaturePython)
  n = 1
FEATURE [App::DocumentObjectGroupPython] Glass  # scripted group (container) (typed FeaturePython)
  Dunit = g/cm3
  Dvalue = 1.032
  Group = -> [G4_Pyrex_Glass001]
  RINDEX = RINDEXLAR
  conduct = 2
  density = 1
  expand = 3
  name = Glass
  specific = 4
FEATURE [App::DocumentObjectGroupPython] G4_CESIUM_IODIDE  label="G4_CESIUM_IODIDE : 1.000"  # scripted group (container) (typed FeaturePython)
  n = 1
FEATURE [App::DocumentObjectGroupPython] LYSO  # scripted group (container) (typed FeaturePython)
  ABSLENGTH = ABSLENGTHLAR
  Dunit = g/cm3
  Dvalue = 7.1
  FASTCOMPONENT = SCINTLAR
  FASTTIMECONSTANT = FTC
  Group = -> [G4_CESIUM_IODIDE]
  RAYLEIGH = RAYLEIGHLAR
  REEMISSIONPROB = SCINTLAR
  RESOLUTIONSCALE = RS
  RINDEX = RINDEXLAR
  SCINTILLATIONYIELD = SY
  SLOWCOMPONENT = SCINTLAR
  SLOWTIMECONSTANT = STC
  YIELDRATIO = YR
  conduct = 2
  density = 1
  expand = 3
  name = LYSO
  specific = 4
FEATURE [App::DocumentObjectGroupPython] Materials  # scripted group (container) (typed FeaturePython)
  Group = -> [Air,Geant4,Glass,LYSO]
FEATURE [Part::FeaturePython] GDMLSphere_Sphere  # WARN: FeaturePython — macro-defined, semantics opaque (R4)
  aunit = 1
  deltaphi = 360
  deltatheta = 180
  lunit = 2
  material = 164
  rmax = 5
  rmin = 0
  startphi = 0
  starttheta = 0
FEATURE [App::Part] LV_Sphere
  Group = -> [GDMLSphere_Sphere]
  Origin = -> Origin004
FEATURE [App::FeaturePython] ScintWrap1  # WARN: FeaturePython — macro-defined, semantics opaque (R4)
  PV1 = Part001
  PV2 = LV_Sphere
  Surface = ScintWrap
FEATURE [Part::FeaturePython] GDMLBox_Box004  # WARN: FeaturePython — macro-defined, semantics opaque (R4)
  CopyNumber = 1
  Placement = pos=(0,0,37.85) rot=(0,0,1;0rad)
  lunit = 2
  material = 1
  x = 27.8
  y = 27.8
  z = 8
FEATURE [App::Link] Link_GDMLBox_Box004
  CopyNumber = 2
  LinkPlacement = pos=(26.764,0,26.764) rot=(0,1,0;0.785398rad)
  LinkedObject = -> GDMLBox_Box004
  Placement = pos=(26.764,0,26.764) rot=(0,1,0;0.785398rad)
FEATURE [App::Link] Link_GDMLBox_Box004001
  CopyNumber = 3
  LinkPlacement = pos=(37.85,0,7.1e-15) rot=(0,1,0;1.5708rad)
  LinkedObject = -> GDMLBox_Box004
  Placement = pos=(37.85,0,7.1e-15) rot=(0,1,0;1.5708rad)
FEATURE [App::Link] Link_GDMLBox_Box004002
  CopyNumber = 4
  LinkPlacement = pos=(26.764,0,-26.764) rot=(0,1,0;2.35619rad)
  LinkedObject = -> GDMLBox_Box004
  Placement = pos=(26.764,0,-26.764) rot=(0,1,0;2.35619rad)
FEATURE [App::Link] Link_GDMLBox_Box004003
  CopyNumber = 5
  LinkPlacement = pos=(4.6e-15,0,-37.85) rot=(0,1,0;3.14159rad)
  LinkedObject = -> GDMLBox_Box004
  Placement = pos=(4.6e-15,0,-37.85) rot=(0,1,0;3.14159rad)
FEATURE [App::Link] Link_GDMLBox_Box004004
  CopyNumber = 6
  LinkPlacement = pos=(-26.764,0,-26.764) rot=(0,1,0;3.92699rad)
  LinkedObject = -> GDMLBox_Box004
  Placement = pos=(-26.764,0,-26.764) rot=(0,1,0;3.92699rad)
FEATURE [App::Link] Link_GDMLBox_Box004005
  CopyNumber = 7
  LinkPlacement = pos=(-37.85,0,-7.1e-15) rot=(0,1,0;4.71239rad)
  LinkedObject = -> GDMLBox_Box004
  Placement = pos=(-37.85,0,-7.1e-15) rot=(0,1,0;4.71239rad)
FEATURE [App::Link] Link_GDMLBox_Box004006
  CopyNumber = 8
  LinkPlacement = pos=(-26.764,0,26.764) rot=(0,1,0;5.49779rad)
  LinkedObject = -> GDMLBox_Box004
  Placement = pos=(-26.764,0,26.764) rot=(0,1,0;5.49779rad)
FEATURE [App::Part] Array002001
  Group = -> [GDMLBox_Box004,Link_GDMLBox_Box004,Link_GDMLBox_Box004001,Link_GDMLBox_Box004002,Link_GDMLBox_Box004003,Link_GDMLBox_Box004004,Link_GDMLBox_Box004005,Link_GDMLBox_Box004006]
  Origin = -> Origin005
FEATURE [App::Part] Part001
  Group = -> [Array002001]
  Origin = -> Origin002
  SkinSurface = 0
FEATURE [App::Link] Link_Child_Array
  CopyNumber = 10
  LinkPlacement = pos=(26.764,0,26.764) rot=(0,1,0;0.785398rad)
  LinkedObject = -> Child_Array
  Placement = pos=(26.764,0,26.764) rot=(0,1,0;0.785398rad)
FEATURE [App::Link] Link_Child_Array001
  CopyNumber = 11
  LinkPlacement = pos=(37.85,0,7.1e-15) rot=(0,1,0;1.5708rad)
  LinkedObject = -> Child_Array
  Placement = pos=(37.85,0,7.1e-15) rot=(0,1,0;1.5708rad)
FEATURE [App::Link] Link_Child_Array002
  CopyNumber = 12
  LinkPlacement = pos=(26.764,0,-26.764) rot=(0,1,0;2.35619rad)
  LinkedObject = -> Child_Array
  Placement = pos=(26.764,0,-26.764) rot=(0,1,0;2.35619rad)
FEATURE [App::Link] Link_Child_Array003
  CopyNumber = 13
  LinkPlacement = pos=(4.6e-15,0,-37.85) rot=(0,1,0;3.14159rad)
  LinkedObject = -> Child_Array
  Placement = pos=(4.6e-15,0,-37.85) rot=(0,1,0;3.14159rad)
FEATURE [App::Link] Link_Child_Array004
  CopyNumber = 14
  LinkPlacement = pos=(-26.764,0,-26.764) rot=(0,1,0;3.92699rad)
  LinkedObject = -> Child_Array
  Placement = pos=(-26.764,0,-26.764) rot=(0,1,0;3.92699rad)
FEATURE [App::Link] Link_Child_Array005
  CopyNumber = 15
  LinkPlacement = pos=(-37.85,0,-7.1e-15) rot=(0,1,0;4.71239rad)
  LinkedObject = -> Child_Array
  Placement = pos=(-37.85,0,-7.1e-15) rot=(0,1,0;4.71239rad)
FEATURE [App::Link] Link_Child_Array006
  CopyNumber = 16
  LinkPlacement = pos=(-26.764,0,26.764) rot=(0,1,0;5.49779rad)
  LinkedObject = -> Child_Array
  Placement = pos=(-26.764,0,26.764) rot=(0,1,0;5.49779rad)
FEATURE [Part::FeaturePython] GDMLBox_Box005  # WARN: FeaturePython — macro-defined, semantics opaque (R4)
  CopyNumber = 17
  Placement = pos=(-11.99,-11.99,5) rot=(0,0,1;0rad)
  lunit = 2
  material = 0
  x = 3.22
  y = 3.22
  z = 2
FEATURE [App::Link] Link_GDMLBox_Box005
  CopyNumber = 18
  LinkPlacement = pos=(-11.99,-8.59,5) rot=(0,0,1;0rad)
  LinkedObject = -> GDMLBox_Box005
  Placement = pos=(-11.99,-8.59,5) rot=(0,0,1;0rad)
FEATURE [App::Link] Link_GDMLBox_Box005001
  CopyNumber = 19
  LinkPlacement = pos=(-11.99,-5.19,5) rot=(0,0,1;0rad)
  LinkedObject = -> GDMLBox_Box005
  Placement = pos=(-11.99,-5.19,5) rot=(0,0,1;0rad)
FEATURE [App::Link] Link_GDMLBox_Box005002
  CopyNumber = 20
  LinkPlacement = pos=(-11.99,-1.79,5) rot=(0,0,1;0rad)
  LinkedObject = -> GDMLBox_Box005
  Placement = pos=(-11.99,-1.79,5) rot=(0,0,1;0rad)
FEATURE [App::Link] Link_GDMLBox_Box005003
  CopyNumber = 21
  LinkPlacement = pos=(-11.99,1.61,5) rot=(0,0,1;0rad)
  LinkedObject = -> GDMLBox_Box005
  Placement = pos=(-11.99,1.61,5) rot=(0,0,1;0rad)
FEATURE [App::Link] Link_GDMLBox_Box005004
  CopyNumber = 22
  LinkPlacement = pos=(-11.99,5.01,5) rot=(0,0,1;0rad)
  LinkedObject = -> GDMLBox_Box005
  Placement = pos=(-11.99,5.01,5) rot=(0,0,1;0rad)
FEATURE [App::Link] Link_GDMLBox_Box005005
  CopyNumber = 23
  LinkPlacement = pos=(-11.99,8.41,5) rot=(0,0,1;0rad)
  LinkedObject = -> GDMLBox_Box005
  Placement = pos=(-11.99,8.41,5) rot=(0,0,1;0rad)
FEATURE [App::Link] Link_GDMLBox_Box005006
  CopyNumber = 24
  LinkPlacement = pos=(-11.99,11.81,5) rot=(0,0,1;0rad)
  LinkedObject = -> GDMLBox_Box005
  Placement = pos=(-11.99,11.81,5) rot=(0,0,1;0rad)
FEATURE [App::Link] Link_GDMLBox_Box005007
  CopyNumber = 25
  LinkPlacement = pos=(-8.59,-11.99,5) rot=(0,0,1;0rad)
  LinkedObject = -> GDMLBox_Box005
  Placement = pos=(-8.59,-11.99,5) rot=(0,0,1;0rad)
FEATURE [App::Link] Link_GDMLBox_Box005008
  CopyNumber = 26
  LinkPlacement = pos=(-8.59,-8.59,5) rot=(0,0,1;0rad)
  LinkedObject = -> GDMLBox_Box005
  Placement = pos=(-8.59,-8.59,5) rot=(0,0,1;0rad)
FEATURE [App::Link] Link_GDMLBox_Box005009
  CopyNumber = 27
  LinkPlacement = pos=(-8.59,-5.19,5) rot=(0,0,1;0rad)
  LinkedObject = -> GDMLBox_Box005
  Placement = pos=(-8.59,-5.19,5) rot=(0,0,1;0rad)
FEATURE [App::Link] Link_GDMLBox_Box005010
  CopyNumber = 28
  LinkPlacement = pos=(-8.59,-1.79,5) rot=(0,0,1;0rad)
  LinkedObject = -> GDMLBox_Box005
  Placement = pos=(-8.59,-1.79,5) rot=(0,0,1;0rad)
FEATURE [App::Link] Link_GDMLBox_Box005011
  CopyNumber = 29
  LinkPlacement = pos=(-8.59,1.61,5) rot=(0,0,1;0rad)
  LinkedObject = -> GDMLBox_Box005
  Placement = pos=(-8.59,1.61,5) rot=(0,0,1;0rad)
FEATURE [App::Link] Link_GDMLBox_Box005012
  CopyNumber = 30
  LinkPlacement = pos=(-8.59,5.01,5) rot=(0,0,1;0rad)
  LinkedObject = -> GDMLBox_Box005
  Placement = pos=(-8.59,5.01,5) rot=(0,0,1;0rad)
FEATURE [App::Link] Link_GDMLBox_Box005013
  CopyNumber = 31
  LinkPlacement = pos=(-8.59,8.41,5) rot=(0,0,1;0rad)
  LinkedObject = -> GDMLBox_Box005
  Placement = pos=(-8.59,8.41,5) rot=(0,0,1;0rad)
FEATURE [App::Link] Link_GDMLBox_Box005014
  CopyNumber = 32
  LinkPlacement = pos=(-8.59,11.81,5) rot=(0,0,1;0rad)
  LinkedObject = -> GDMLBox_Box005
  Placement = pos=(-8.59,11.81,5) rot=(0,0,1;0rad)
FEATURE [App::Link] Link_GDMLBox_Box005015
  CopyNumber = 33
  LinkPlacement = pos=(-5.19,-11.99,5) rot=(0,0,1;0rad)
  LinkedObject = -> GDMLBox_Box005
  Placement = pos=(-5.19,-11.99,5) rot=(0,0,1;0rad)
FEATURE [App::Link] Link_GDMLBox_Box005016
  CopyNumber = 34
  LinkPlacement = pos=(-5.19,-8.59,5) rot=(0,0,1;0rad)
  LinkedObject = -> GDMLBox_Box005
  Placement = pos=(-5.19,-8.59,5) rot=(0,0,1;0rad)
FEATURE [App::Link] Link_GDMLBox_Box005017
  CopyNumber = 35
  LinkPlacement = pos=(-5.19,-5.19,5) rot=(0,0,1;0rad)
  LinkedObject = -> GDMLBox_Box005
  Placement = pos=(-5.19,-5.19,5) rot=(0,0,1;0rad)
FEATURE [App::Link] Link_GDMLBox_Box005018
  CopyNumber = 36
  LinkPlacement = pos=(-5.19,-1.79,5) rot=(0,0,1;0rad)
  LinkedObject = -> GDMLBox_Box005
  Placement = pos=(-5.19,-1.79,5) rot=(0,0,1;0rad)
FEATURE [App::Link] Link_GDMLBox_Box005019
  CopyNumber = 37
  LinkPlacement = pos=(-5.19,1.61,5) rot=(0,0,1;0rad)
  LinkedObject = -> GDMLBox_Box005
  Placement = pos=(-5.19,1.61,5) rot=(0,0,1;0rad)
FEATURE [App::Link] Link_GDMLBox_Box005020
  CopyNumber = 38
  LinkPlacement = pos=(-5.19,5.01,5) rot=(0,0,1;0rad)
  LinkedObject = -> GDMLBox_Box005
  Placement = pos=(-5.19,5.01,5) rot=(0,0,1;0rad)
FEATURE [App::Link] Link_GDMLBox_Box005021
  CopyNumber = 39
  LinkPlacement = pos=(-5.19,8.41,5) rot=(0,0,1;0rad)
  LinkedObject = -> GDMLBox_Box005
  Placement = pos=(-5.19,8.41,5) rot=(0,0,1;0rad)
FEATURE [App::Link] Link_GDMLBox_Box005022
  CopyNumber = 40
  LinkPlacement = pos=(-5.19,11.81,5) rot=(0,0,1;0rad)
  LinkedObject = -> GDMLBox_Box005
  Placement = pos=(-5.19,11.81,5) rot=(0,0,1;0rad)
FEATURE [App::Link] Link_GDMLBox_Box005023
  CopyNumber = 41
  LinkPlacement = pos=(-1.79,-11.99,5) rot=(0,0,1;0rad)
  LinkedObject = -> GDMLBox_Box005
  Placement = pos=(-1.79,-11.99,5) rot=(0,0,1;0rad)
FEATURE [App::Link] Link_GDMLBox_Box005024
  CopyNumber = 42
  LinkPlacement = pos=(-1.79,-8.59,5) rot=(0,0,1;0rad)
  LinkedObject = -> GDMLBox_Box005
  Placement = pos=(-1.79,-8.59,5) rot=(0,0,1;0rad)
FEATURE [App::Link] Link_GDMLBox_Box005025
  CopyNumber = 43
  LinkPlacement = pos=(-1.79,-5.19,5) rot=(0,0,1;0rad)
  LinkedObject = -> GDMLBox_Box005
  Placement = pos=(-1.79,-5.19,5) rot=(0,0,1;0rad)
FEATURE [App::Link] Link_GDMLBox_Box005026
  CopyNumber = 44
  LinkPlacement = pos=(-1.79,-1.79,5) rot=(0,0,1;0rad)
  LinkedObject = -> GDMLBox_Box005
  Placement = pos=(-1.79,-1.79,5) rot=(0,0,1;0rad)
FEATURE [App::Link] Link_GDMLBox_Box005027
  CopyNumber = 45
  LinkPlacement = pos=(-1.79,1.61,5) rot=(0,0,1;0rad)
  LinkedObject = -> GDMLBox_Box005
  Placement = pos=(-1.79,1.61,5) rot=(0,0,1;0rad)
FEATURE [App::Link] Link_GDMLBox_Box005028
  CopyNumber = 46
  LinkPlacement = pos=(-1.79,5.01,5) rot=(0,0,1;0rad)
  LinkedObject = -> GDMLBox_Box005
  Placement = pos=(-1.79,5.01,5) rot=(0,0,1;0rad)
FEATURE [App::Link] Link_GDMLBox_Box005029
  CopyNumber = 47
  LinkPlacement = pos=(-1.79,8.41,5) rot=(0,0,1;0rad)
  LinkedObject = -> GDMLBox_Box005
  Placement = pos=(-1.79,8.41,5) rot=(0,0,1;0rad)
FEATURE [App::Link] Link_GDMLBox_Box005030
  CopyNumber = 48
  LinkPlacement = pos=(-1.79,11.81,5) rot=(0,0,1;0rad)
  LinkedObject = -> GDMLBox_Box005
  Placement = pos=(-1.79,11.81,5) rot=(0,0,1;0rad)
FEATURE [App::Link] Link_GDMLBox_Box005031
  CopyNumber = 49
  LinkPlacement = pos=(1.61,-11.99,5) rot=(0,0,1;0rad)
  LinkedObject = -> GDMLBox_Box005
  Placement = pos=(1.61,-11.99,5) rot=(0,0,1;0rad)
FEATURE [App::Link] Link_GDMLBox_Box005032
  CopyNumber = 50
  LinkPlacement = pos=(1.61,-8.59,5) rot=(0,0,1;0rad)
  LinkedObject = -> GDMLBox_Box005
  Placement = pos=(1.61,-8.59,5) rot=(0,0,1;0rad)
FEATURE [App::Link] Link_GDMLBox_Box005033
  CopyNumber = 51
  LinkPlacement = pos=(1.61,-5.19,5) rot=(0,0,1;0rad)
  LinkedObject = -> GDMLBox_Box005
  Placement = pos=(1.61,-5.19,5) rot=(0,0,1;0rad)
FEATURE [App::Link] Link_GDMLBox_Box005034
  CopyNumber = 52
  LinkPlacement = pos=(1.61,-1.79,5) rot=(0,0,1;0rad)
  LinkedObject = -> GDMLBox_Box005
  Placement = pos=(1.61,-1.79,5) rot=(0,0,1;0rad)
FEATURE [App::Link] Link_GDMLBox_Box005035
  CopyNumber = 53
  LinkPlacement = pos=(1.61,1.61,5) rot=(0,0,1;0rad)
  LinkedObject = -> GDMLBox_Box005
  Placement = pos=(1.61,1.61,5) rot=(0,0,1;0rad)
FEATURE [App::Link] Link_GDMLBox_Box005036
  CopyNumber = 54
  LinkPlacement = pos=(1.61,5.01,5) rot=(0,0,1;0rad)
  LinkedObject = -> GDMLBox_Box005
  Placement = pos=(1.61,5.01,5) rot=(0,0,1;0rad)
FEATURE [App::Link] Link_GDMLBox_Box005037
  CopyNumber = 55
  LinkPlacement = pos=(1.61,8.41,5) rot=(0,0,1;0rad)
  LinkedObject = -> GDMLBox_Box005
  Placement = pos=(1.61,8.41,5) rot=(0,0,1;0rad)
FEATURE [App::Link] Link_GDMLBox_Box005038
  CopyNumber = 56
  LinkPlacement = pos=(1.61,11.81,5) rot=(0,0,1;0rad)
  LinkedObject = -> GDMLBox_Box005
  Placement = pos=(1.61,11.81,5) rot=(0,0,1;0rad)
FEATURE [App::Link] Link_GDMLBox_Box005039
  CopyNumber = 57
  LinkPlacement = pos=(5.01,-11.99,5) rot=(0,0,1;0rad)
  LinkedObject = -> GDMLBox_Box005
  Placement = pos=(5.01,-11.99,5) rot=(0,0,1;0rad)
FEATURE [App::Link] Link_GDMLBox_Box005040
  CopyNumber = 58
  LinkPlacement = pos=(5.01,-8.59,5) rot=(0,0,1;0rad)
  LinkedObject = -> GDMLBox_Box005
  Placement = pos=(5.01,-8.59,5) rot=(0,0,1;0rad)
FEATURE [App::Link] Link_GDMLBox_Box005041
  CopyNumber = 59
  LinkPlacement = pos=(5.01,-5.19,5) rot=(0,0,1;0rad)
  LinkedObject = -> GDMLBox_Box005
  Placement = pos=(5.01,-5.19,5) rot=(0,0,1;0rad)
FEATURE [App::Link] Link_GDMLBox_Box005042
  CopyNumber = 60
  LinkPlacement = pos=(5.01,-1.79,5) rot=(0,0,1;0rad)
  LinkedObject = -> GDMLBox_Box005
  Placement = pos=(5.01,-1.79,5) rot=(0,0,1;0rad)
FEATURE [App::Link] Link_GDMLBox_Box005043
  CopyNumber = 61
  LinkPlacement = pos=(5.01,1.61,5) rot=(0,0,1;0rad)
  LinkedObject = -> GDMLBox_Box005
  Placement = pos=(5.01,1.61,5) rot=(0,0,1;0rad)
FEATURE [App::Link] Link_GDMLBox_Box005044
  CopyNumber = 62
  LinkPlacement = pos=(5.01,5.01,5) rot=(0,0,1;0rad)
  LinkedObject = -> GDMLBox_Box005
  Placement = pos=(5.01,5.01,5) rot=(0,0,1;0rad)
FEATURE [App::Link] Link_GDMLBox_Box005045
  CopyNumber = 63
  LinkPlacement = pos=(5.01,8.41,5) rot=(0,0,1;0rad)
  LinkedObject = -> GDMLBox_Box005
  Placement = pos=(5.01,8.41,5) rot=(0,0,1;0rad)
FEATURE [App::Link] Link_GDMLBox_Box005046
  CopyNumber = 64
  LinkPlacement = pos=(5.01,11.81,5) rot=(0,0,1;0rad)
  LinkedObject = -> GDMLBox_Box005
  Placement = pos=(5.01,11.81,5) rot=(0,0,1;0rad)
FEATURE [App::Link] Link_GDMLBox_Box005047
  CopyNumber = 65
  LinkPlacement = pos=(8.41,-11.99,5) rot=(0,0,1;0rad)
  LinkedObject = -> GDMLBox_Box005
  Placement = pos=(8.41,-11.99,5) rot=(0,0,1;0rad)
FEATURE [App::Link] Link_GDMLBox_Box005048
  CopyNumber = 66
  LinkPlacement = pos=(8.41,-8.59,5) rot=(0,0,1;0rad)
  LinkedObject = -> GDMLBox_Box005
  Placement = pos=(8.41,-8.59,5) rot=(0,0,1;0rad)
FEATURE [App::Link] Link_GDMLBox_Box005049
  CopyNumber = 67
  LinkPlacement = pos=(8.41,-5.19,5) rot=(0,0,1;0rad)
  LinkedObject = -> GDMLBox_Box005
  Placement = pos=(8.41,-5.19,5) rot=(0,0,1;0rad)
FEATURE [App::Link] Link_GDMLBox_Box005050
  CopyNumber = 68
  LinkPlacement = pos=(8.41,-1.79,5) rot=(0,0,1;0rad)
  LinkedObject = -> GDMLBox_Box005
  Placement = pos=(8.41,-1.79,5) rot=(0,0,1;0rad)
FEATURE [App::Link] Link_GDMLBox_Box005051
  CopyNumber = 69
  LinkPlacement = pos=(8.41,1.61,5) rot=(0,0,1;0rad)
  LinkedObject = -> GDMLBox_Box005
  Placement = pos=(8.41,1.61,5) rot=(0,0,1;0rad)
FEATURE [App::Link] Link_GDMLBox_Box005052
  CopyNumber = 70
  LinkPlacement = pos=(8.41,5.01,5) rot=(0,0,1;0rad)
  LinkedObject = -> GDMLBox_Box005
  Placement = pos=(8.41,5.01,5) rot=(0,0,1;0rad)
FEATURE [App::Link] Link_GDMLBox_Box005053
  CopyNumber = 71
  LinkPlacement = pos=(8.41,8.41,5) rot=(0,0,1;0rad)
  LinkedObject = -> GDMLBox_Box005
  Placement = pos=(8.41,8.41,5) rot=(0,0,1;0rad)
FEATURE [App::Link] Link_GDMLBox_Box005054
  CopyNumber = 72
  LinkPlacement = pos=(8.41,11.81,5) rot=(0,0,1;0rad)
  LinkedObject = -> GDMLBox_Box005
  Placement = pos=(8.41,11.81,5) rot=(0,0,1;0rad)
FEATURE [App::Link] Link_GDMLBox_Box005055
  CopyNumber = 73
  LinkPlacement = pos=(11.81,-11.99,5) rot=(0,0,1;0rad)
  LinkedObject = -> GDMLBox_Box005
  Placement = pos=(11.81,-11.99,5) rot=(0,0,1;0rad)
FEATURE [App::Link] Link_GDMLBox_Box005056
  CopyNumber = 74
  LinkPlacement = pos=(11.81,-8.59,5) rot=(0,0,1;0rad)
  LinkedObject = -> GDMLBox_Box005
  Placement = pos=(11.81,-8.59,5) rot=(0,0,1;0rad)
FEATURE [App::Link] Link_GDMLBox_Box005057
  CopyNumber = 75
  LinkPlacement = pos=(11.81,-5.19,5) rot=(0,0,1;0rad)
  LinkedObject = -> GDMLBox_Box005
  Placement = pos=(11.81,-5.19,5) rot=(0,0,1;0rad)
FEATURE [App::Link] Link_GDMLBox_Box005058
  CopyNumber = 76
  LinkPlacement = pos=(11.81,-1.79,5) rot=(0,0,1;0rad)
  LinkedObject = -> GDMLBox_Box005
  Placement = pos=(11.81,-1.79,5) rot=(0,0,1;0rad)
FEATURE [App::Link] Link_GDMLBox_Box005059
  CopyNumber = 77
  LinkPlacement = pos=(11.81,1.61,5) rot=(0,0,1;0rad)
  LinkedObject = -> GDMLBox_Box005
  Placement = pos=(11.81,1.61,5) rot=(0,0,1;0rad)
FEATURE [App::Link] Link_GDMLBox_Box005060
  CopyNumber = 78
  LinkPlacement = pos=(11.81,5.01,5) rot=(0,0,1;0rad)
  LinkedObject = -> GDMLBox_Box005
  Placement = pos=(11.81,5.01,5) rot=(0,0,1;0rad)
FEATURE [App::Link] Link_GDMLBox_Box005061
  CopyNumber = 79
  LinkPlacement = pos=(11.81,8.41,5) rot=(0,0,1;0rad)
  LinkedObject = -> GDMLBox_Box005
  Placement = pos=(11.81,8.41,5) rot=(0,0,1;0rad)
FEATURE [App::Link] Link_GDMLBox_Box005062
  CopyNumber = 80
  LinkPlacement = pos=(11.81,11.81,5) rot=(0,0,1;0rad)
  LinkedObject = -> GDMLBox_Box005
  Placement = pos=(11.81,11.81,5) rot=(0,0,1;0rad)
FEATURE [App::Part] Child_Array  label="Child_Array001"
  CopyNumber = 9
  Group = -> [GDMLBox_Box005,Link_GDMLBox_Box005,Link_GDMLBox_Box005001,Link_GDMLBox_Box005002,Link_GDMLBox_Box005003,Link_GDMLBox_Box005004,Link_GDMLBox_Box005005,Link_GDMLBox_Box005006,Link_GDMLBox_Box005007,Link_GDMLBox_Box005008,Link_GDMLBox_Box005009,Link_GDMLBox_Box005010,Link_GDMLBox_Box005011,Link_GDMLBox_Box005012,Link_GDMLBox_Box005013,Link_GDMLBox_Box005014,Link_GDMLBox_Box005015,+47 more]
  Origin = -> Origin007
  Placement = pos=(0,0,37.85) rot=(0,0,1;0rad)
FEATURE [App::Part] Parent_Array  label="Parent_Array001"
  Group = -> [Child_Array,Link_Child_Array,Link_Child_Array001,Link_Child_Array002,Link_Child_Array003,Link_Child_Array004,Link_Child_Array005,Link_Child_Array006]
  Origin = -> Origin006
FEATURE [App::Part] Part
  Group = -> [Parent_Array]
  Origin = -> Origin003
FEATURE [App::Part] worldVOL
  Group = -> [GDMLBox_WorldBox,Part001,Part,LV_Sphere]
  Origin = -> Origin
